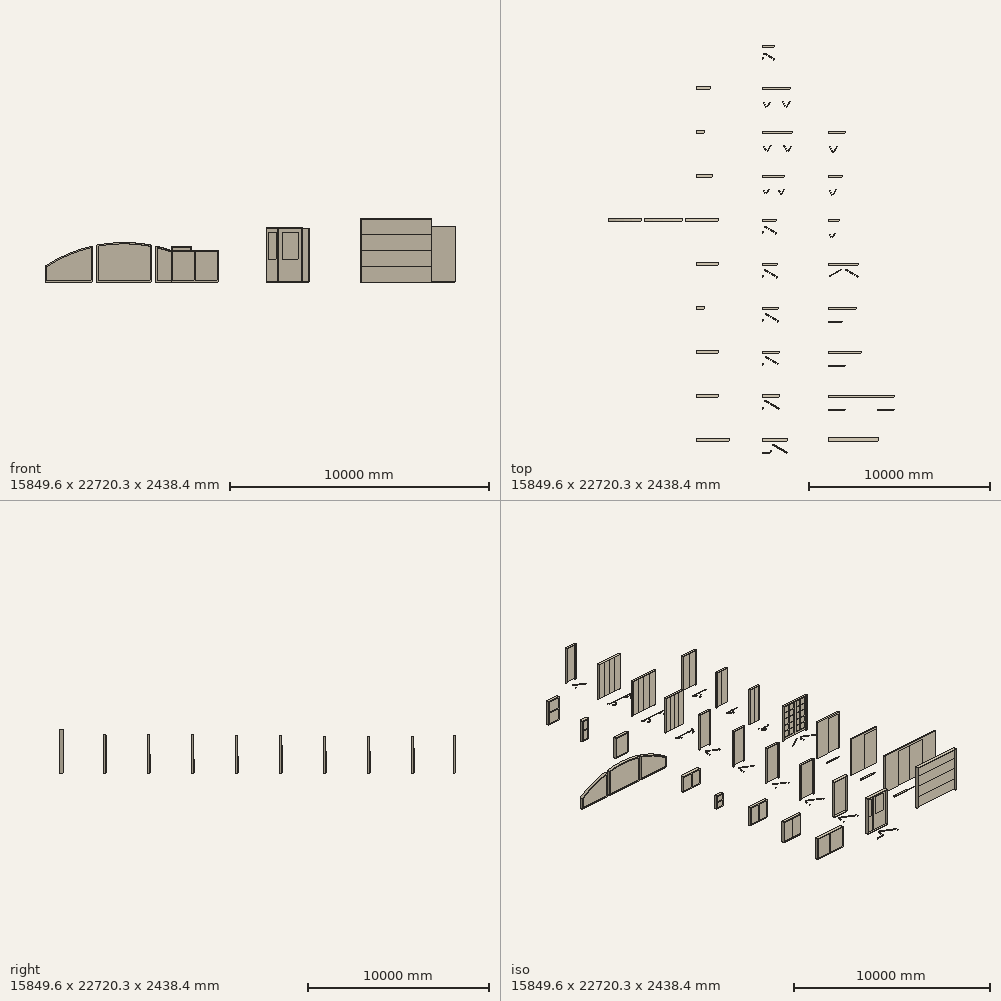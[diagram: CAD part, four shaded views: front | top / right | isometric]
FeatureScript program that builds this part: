
annotation { "Feature Type Name" : "Feature", "Feature Type Description" : "" }
export const myFeature = defineFeature(function(context is Context, id is Id, definition is map)
    precondition{}
    {
        {
            var Q0;
            Q0=qCreatedBy(makeId("Front.planeOp"),FACE);
            var sketch = newSketch(context, id + "F0", { "sketchPlane" : qUnion([Q0])});
            skLineSegment(sketch, "E0.bottom", {"start": v(0, 0) * mm, "end": v(1828.8, 0) * mm});
            skLineSegment(sketch, "E0.top", {"start": v(0, 1219.2) * mm, "end": v(1828.8, 1219.2) * mm});
            skLineSegment(sketch, "E0.left", {"start": v(0, 0) * mm, "end": v(0, 1219.2) * mm});
            skLineSegment(sketch, "E0.right", {"start": v(1828.8, 0) * mm, "end": v(1828.8, 1219.2) * mm});
            skSolve(sketch);
        }
        {
            var Q0;
            Q0=qSketchRegion(id+"F0",true);
            extrude(context, id + "F1", {"entities" : qUnion([Q0]), "oppositeDirection" : true, "depth" : 50.8 * mm});
        }
        {
            var Q0;
            Q0=makeQuery(id+"F1.opExtrude","CAP_FACE",FACE,{"disambiguationData":[OSD([sQuery(id+"F0.wireOp",EDGE,"E0.bottom"),sQuery(id+"F0.wireOp",EDGE,"E0.top"),sQuery(id+"F0.wireOp",EDGE,"E0.left"),sQuery(id+"F0.wireOp",EDGE,"E0.right")])],"isStart":false});
            var sketch = newSketch(context, id + "F2", { "sketchPlane" : qUnion([Q0])});
            skLineSegment(sketch, "E1.bottom", {"start": v(-1778, 1168.4) * mm, "end": v(-939.8, 1168.4) * mm});
            skLineSegment(sketch, "E1.top", {"start": v(-1778, 50.8) * mm, "end": v(-939.8, 50.8) * mm});
            skLineSegment(sketch, "E1.left", {"start": v(-1778, 1168.4) * mm, "end": v(-1778, 50.8) * mm});
            skLineSegment(sketch, "E1.right", {"start": v(-939.8, 1168.4) * mm, "end": v(-939.8, 50.8) * mm});
            skLineSegment(sketch, "E2.bottom", {"start": v(-889, 1168.4) * mm, "end": v(-50.8, 1168.4) * mm});
            skLineSegment(sketch, "E2.top", {"start": v(-889, 50.8) * mm, "end": v(-50.8, 50.8) * mm});
            skLineSegment(sketch, "E2.left", {"start": v(-889, 1168.4) * mm, "end": v(-889, 50.8) * mm});
            skLineSegment(sketch, "E2.right", {"start": v(-50.8, 1168.4) * mm, "end": v(-50.8, 50.8) * mm});
            skSolve(sketch);
        }
        {
            var Q0;
            Q0=qSketchRegion(id+"F2",true);
            extrude(context, id + "F3", {"entities" : qUnion([Q0]), "operationType" : NewBodyOperationType.REMOVE, "oppositeDirection" : true, "depth" : 12.7 * mm});
        }
        {
            var Q0;
            Q0=makeQuery(id+"F1.opExtrude","CAP_FACE",FACE,{"disambiguationData":[OSD([sQuery(id+"F0.wireOp",EDGE,"E0.bottom"),sQuery(id+"F0.wireOp",EDGE,"E0.top"),sQuery(id+"F0.wireOp",EDGE,"E0.left"),sQuery(id+"F0.wireOp",EDGE,"E0.right")])],"isStart":true});
            var sketch = newSketch(context, id + "F4", { "sketchPlane" : qUnion([Q0])});
            skLineSegment(sketch, "E3.0.0", {"start": v(1778, 1168.4) * mm, "end": v(1778, 50.8) * mm});
            skLineSegment(sketch, "E3.0.1", {"start": v(1778, 50.8) * mm, "end": v(939.8, 50.8) * mm});
            skLineSegment(sketch, "E3.0.2", {"start": v(939.8, 50.8) * mm, "end": v(939.8, 1168.4) * mm});
            skLineSegment(sketch, "E3.0.3", {"start": v(939.8, 1168.4) * mm, "end": v(1778, 1168.4) * mm});
            skLineSegment(sketch, "E4.0.0", {"start": v(889, 1168.4) * mm, "end": v(889, 50.8) * mm});
            skLineSegment(sketch, "E4.0.1", {"start": v(889, 50.8) * mm, "end": v(50.8, 50.8) * mm});
            skLineSegment(sketch, "E4.0.2", {"start": v(50.8, 50.8) * mm, "end": v(50.8, 1168.4) * mm});
            skLineSegment(sketch, "E4.0.3", {"start": v(50.8, 1168.4) * mm, "end": v(889, 1168.4) * mm});
            skSolve(sketch);
        }
        {
            var Q0;
            Q0=qSketchRegion(id+"F4",true);
            extrude(context, id + "F5", {"entities" : qUnion([Q0]), "operationType" : NewBodyOperationType.REMOVE, "oppositeDirection" : true, "depth" : 12.7 * mm});
        }
        {
            var Q0;
            Q0=makeQuery(id+"F1.opExtrude","CAP_FACE",FACE,{"disambiguationData":[OSD([sQuery(id+"F0.wireOp",EDGE,"E0.bottom"),sQuery(id+"F0.wireOp",EDGE,"E0.top"),sQuery(id+"F0.wireOp",EDGE,"E0.left"),sQuery(id+"F0.wireOp",EDGE,"E0.right")])],"isStart":false});
            var sketch = newSketch(context, id + "F6", { "sketchPlane" : qUnion([Q0])});
            skLineSegment(sketch, "E5.bottom", {"start": v(-1809.75, 1200.15) * mm, "end": v(-19.05, 1200.15) * mm});
            skLineSegment(sketch, "E5.top", {"start": v(-1809.75, 19.05) * mm, "end": v(-19.05, 19.05) * mm});
            skLineSegment(sketch, "E5.left", {"start": v(-1809.75, 1200.15) * mm, "end": v(-1809.75, 19.05) * mm});
            skLineSegment(sketch, "E5.right", {"start": v(-19.05, 1200.15) * mm, "end": v(-19.05, 19.05) * mm});
            skSolve(sketch);
        }
        {
            var Q0;
            Q0=makeQuery(id+"F6.imprint","IMPRINT",FACE,{"disambiguationData":[TD([[makeQuery(id+"F6.imprint","IMPRINT",EDGE,{"derivedFrom":sQuery(id+"F6.wireOp",EDGE,"E5.bottom")}),1.0]])]});
            extrude(context, id + "F7", {"entities" : qUnion([Q0]), "operationType" : NewBodyOperationType.ADD, "depth" : 114.3 * mm});
        }
        {
            var Q0;
            Q0=qCreatedBy(makeId("Front.planeOp"),FACE);
            cPlane(context, id + "F8", {"entities" : qUnion([Q0]), "cplaneType" : CPlaneType.OFFSET, "offset" : 2438.4 * mm, "oppositeDirection" : true, "width" : 152.4 * mm, "height" : 152.4 * mm});
        }
        {
            var Q0;
            Q0=qCreatedBy(id+"F8.planeOp",FACE);
            var sketch = newSketch(context, id + "F9", { "sketchPlane" : qUnion([Q0])});
            skLineSegment(sketch, "E6.bottom", {"start": v(0, 0) * mm, "end": v(1219.2, 0) * mm});
            skLineSegment(sketch, "E6.top", {"start": v(0, 1219.2) * mm, "end": v(1219.2, 1219.2) * mm});
            skLineSegment(sketch, "E6.left", {"start": v(0, 0) * mm, "end": v(0, 1219.2) * mm});
            skLineSegment(sketch, "E6.right", {"start": v(1219.2, 0) * mm, "end": v(1219.2, 1219.2) * mm});
            skSolve(sketch);
        }
        {
            var Q0;
            Q0=qSketchRegion(id+"F9",true);
            extrude(context, id + "F10", {"entities" : qUnion([Q0]), "oppositeDirection" : true, "depth" : 50.8 * mm});
        }
        {
            var Q0;
            Q0=makeQuery(id+"F10.opExtrude","CAP_FACE",FACE,{"disambiguationData":[OSD([sQuery(id+"F9.wireOp",EDGE,"E6.bottom"),sQuery(id+"F9.wireOp",EDGE,"E6.top"),sQuery(id+"F9.wireOp",EDGE,"E6.left"),sQuery(id+"F9.wireOp",EDGE,"E6.right")])],"isStart":true});
            var sketch = newSketch(context, id + "F11", { "sketchPlane" : qUnion([Q0])});
            skLineSegment(sketch, "E7.bottom", {"start": v(50.8, 1168.4) * mm, "end": v(584.2, 1168.4) * mm});
            skLineSegment(sketch, "E7.top", {"start": v(50.8, 50.8) * mm, "end": v(584.2, 50.8) * mm});
            skLineSegment(sketch, "E7.left", {"start": v(50.8, 1168.4) * mm, "end": v(50.8, 50.8) * mm});
            skLineSegment(sketch, "E7.right", {"start": v(584.2, 1168.4) * mm, "end": v(584.2, 50.8) * mm});
            skLineSegment(sketch, "E8.bottom", {"start": v(635, 1168.4) * mm, "end": v(1168.4, 1168.4) * mm});
            skLineSegment(sketch, "E8.top", {"start": v(635, 50.8) * mm, "end": v(1168.4, 50.8) * mm});
            skLineSegment(sketch, "E8.left", {"start": v(635, 1168.4) * mm, "end": v(635, 50.8) * mm});
            skLineSegment(sketch, "E8.right", {"start": v(1168.4, 1168.4) * mm, "end": v(1168.4, 50.8) * mm});
            skSolve(sketch);
        }
        {
            var Q0;
            Q0=qSketchRegion(id+"F11",true);
            extrude(context, id + "F12", {"entities" : qUnion([Q0]), "operationType" : NewBodyOperationType.REMOVE, "oppositeDirection" : true, "depth" : 12.7 * mm});
        }
        {
            var Q0;
            Q0=makeQuery(id+"F10.opExtrude","CAP_FACE",FACE,{"disambiguationData":[OSD([sQuery(id+"F9.wireOp",EDGE,"E6.bottom"),sQuery(id+"F9.wireOp",EDGE,"E6.top"),sQuery(id+"F9.wireOp",EDGE,"E6.left"),sQuery(id+"F9.wireOp",EDGE,"E6.right")])],"isStart":false});
            var sketch = newSketch(context, id + "F13", { "sketchPlane" : qUnion([Q0])});
            skLineSegment(sketch, "E9.0.0", {"start": v(-50.8, 1168.4) * mm, "end": v(-50.8, 50.8) * mm});
            skLineSegment(sketch, "E9.0.1", {"start": v(-50.8, 50.8) * mm, "end": v(-584.2, 50.8) * mm});
            skLineSegment(sketch, "E9.0.2", {"start": v(-584.2, 50.8) * mm, "end": v(-584.2, 1168.4) * mm});
            skLineSegment(sketch, "E9.0.3", {"start": v(-584.2, 1168.4) * mm, "end": v(-50.8, 1168.4) * mm});
            skLineSegment(sketch, "E10.0.0", {"start": v(-635, 1168.4) * mm, "end": v(-635, 50.8) * mm});
            skLineSegment(sketch, "E10.0.1", {"start": v(-635, 50.8) * mm, "end": v(-1168.4, 50.8) * mm});
            skLineSegment(sketch, "E10.0.2", {"start": v(-1168.4, 50.8) * mm, "end": v(-1168.4, 1168.4) * mm});
            skLineSegment(sketch, "E10.0.3", {"start": v(-1168.4, 1168.4) * mm, "end": v(-635, 1168.4) * mm});
            skSolve(sketch);
        }
        {
            var Q0;
            Q0=qSketchRegion(id+"F13",true);
            extrude(context, id + "F14", {"entities" : qUnion([Q0]), "operationType" : NewBodyOperationType.REMOVE, "oppositeDirection" : true, "depth" : 12.7 * mm});
        }
        {
            var Q0;
            Q0=makeQuery(id+"F10.opExtrude","CAP_FACE",FACE,{"disambiguationData":[OSD([sQuery(id+"F9.wireOp",EDGE,"E6.bottom"),sQuery(id+"F9.wireOp",EDGE,"E6.top"),sQuery(id+"F9.wireOp",EDGE,"E6.left"),sQuery(id+"F9.wireOp",EDGE,"E6.right")])],"isStart":false});
            var sketch = newSketch(context, id + "F15", { "sketchPlane" : qUnion([Q0])});
            skLineSegment(sketch, "E11.bottom", {"start": v(-1200.15, 1200.15) * mm, "end": v(-19.05, 1200.15) * mm});
            skLineSegment(sketch, "E11.top", {"start": v(-1200.15, 19.05) * mm, "end": v(-19.05, 19.05) * mm});
            skLineSegment(sketch, "E11.left", {"start": v(-1200.15, 1200.15) * mm, "end": v(-1200.15, 19.05) * mm});
            skLineSegment(sketch, "E11.right", {"start": v(-19.05, 1200.15) * mm, "end": v(-19.05, 19.05) * mm});
            skSolve(sketch);
        }
        {
            var Q0;
            Q0=makeQuery(id+"F15.imprint","IMPRINT",FACE,{"disambiguationData":[TD([[makeQuery(id+"F15.imprint","IMPRINT",EDGE,{"derivedFrom":sQuery(id+"F15.wireOp",EDGE,"E11.bottom")}),1.0]])]});
            extrude(context, id + "F16", {"entities" : qUnion([Q0]), "operationType" : NewBodyOperationType.ADD, "depth" : 114.3 * mm});
        }
        {
            var Q0;
            Q0=qCreatedBy(id+"F8.planeOp",FACE);
            cPlane(context, id + "F17", {"entities" : qUnion([Q0]), "cplaneType" : CPlaneType.OFFSET, "offset" : 2438.4 * mm, "oppositeDirection" : true, "width" : 152.4 * mm, "height" : 152.4 * mm});
        }
        {
            var Q0;
            Q0=qCreatedBy(id+"F17.planeOp",FACE);
            var sketch = newSketch(context, id + "F18", { "sketchPlane" : qUnion([Q0])});
            skLineSegment(sketch, "E12.bottom", {"start": v(0, 0) * mm, "end": v(1219.2, 0) * mm});
            skLineSegment(sketch, "E12.top", {"start": v(0, 1066.8) * mm, "end": v(1219.2, 1066.8) * mm});
            skLineSegment(sketch, "E12.left", {"start": v(0, 0) * mm, "end": v(0, 1066.8) * mm});
            skLineSegment(sketch, "E12.right", {"start": v(1219.2, 0) * mm, "end": v(1219.2, 1066.8) * mm});
            skSolve(sketch);
        }
        {
            var Q0;
            Q0=qSketchRegion(id+"F18",true);
            extrude(context, id + "F19", {"entities" : qUnion([Q0]), "oppositeDirection" : true, "depth" : 50.8 * mm});
        }
        {
            var Q0;
            Q0=makeQuery(id+"F19.opExtrude","CAP_FACE",FACE,{"disambiguationData":[OSD([sQuery(id+"F18.wireOp",EDGE,"E12.bottom"),sQuery(id+"F18.wireOp",EDGE,"E12.top"),sQuery(id+"F18.wireOp",EDGE,"E12.left"),sQuery(id+"F18.wireOp",EDGE,"E12.right")])],"isStart":true});
            var sketch = newSketch(context, id + "F20", { "sketchPlane" : qUnion([Q0])});
            skLineSegment(sketch, "E13.bottom", {"start": v(50.8, 1016) * mm, "end": v(584.2, 1016) * mm});
            skLineSegment(sketch, "E13.top", {"start": v(50.8, 50.8) * mm, "end": v(584.2, 50.8) * mm});
            skLineSegment(sketch, "E13.left", {"start": v(50.8, 1016) * mm, "end": v(50.8, 50.8) * mm});
            skLineSegment(sketch, "E13.right", {"start": v(584.2, 1016) * mm, "end": v(584.2, 50.8) * mm});
            skLineSegment(sketch, "E14.bottom", {"start": v(635, 1016) * mm, "end": v(1168.4, 1016) * mm});
            skLineSegment(sketch, "E14.top", {"start": v(635, 50.8) * mm, "end": v(1168.4, 50.8) * mm});
            skLineSegment(sketch, "E14.left", {"start": v(635, 1016) * mm, "end": v(635, 50.8) * mm});
            skLineSegment(sketch, "E14.right", {"start": v(1168.4, 1016) * mm, "end": v(1168.4, 50.8) * mm});
            skSolve(sketch);
        }
        {
            var Q0;
            Q0=qSketchRegion(id+"F20",true);
            extrude(context, id + "F21", {"entities" : qUnion([Q0]), "operationType" : NewBodyOperationType.REMOVE, "oppositeDirection" : true, "depth" : 12.7 * mm});
        }
        {
            var Q0;
            Q0=makeQuery(id+"F19.opExtrude","CAP_FACE",FACE,{"disambiguationData":[OSD([sQuery(id+"F18.wireOp",EDGE,"E12.bottom"),sQuery(id+"F18.wireOp",EDGE,"E12.top"),sQuery(id+"F18.wireOp",EDGE,"E12.left"),sQuery(id+"F18.wireOp",EDGE,"E12.right")])],"isStart":false});
            var sketch = newSketch(context, id + "F22", { "sketchPlane" : qUnion([Q0])});
            skLineSegment(sketch, "E15.0.0", {"start": v(-50.8, 1016) * mm, "end": v(-50.8, 50.8) * mm});
            skLineSegment(sketch, "E15.0.1", {"start": v(-50.8, 50.8) * mm, "end": v(-584.2, 50.8) * mm});
            skLineSegment(sketch, "E15.0.2", {"start": v(-584.2, 50.8) * mm, "end": v(-584.2, 1016) * mm});
            skLineSegment(sketch, "E15.0.3", {"start": v(-584.2, 1016) * mm, "end": v(-50.8, 1016) * mm});
            skLineSegment(sketch, "E16.0.0", {"start": v(-635, 1016) * mm, "end": v(-635, 50.8) * mm});
            skLineSegment(sketch, "E16.0.1", {"start": v(-635, 50.8) * mm, "end": v(-1168.4, 50.8) * mm});
            skLineSegment(sketch, "E16.0.2", {"start": v(-1168.4, 50.8) * mm, "end": v(-1168.4, 1016) * mm});
            skLineSegment(sketch, "E16.0.3", {"start": v(-1168.4, 1016) * mm, "end": v(-635, 1016) * mm});
            skSolve(sketch);
        }
        {
            var Q0;
            Q0=qSketchRegion(id+"F22",true);
            extrude(context, id + "F23", {"entities" : qUnion([Q0]), "operationType" : NewBodyOperationType.REMOVE, "oppositeDirection" : true, "depth" : 12.7 * mm});
        }
        {
            var Q0;
            Q0=makeQuery(id+"F19.opExtrude","CAP_FACE",FACE,{"disambiguationData":[OSD([sQuery(id+"F18.wireOp",EDGE,"E12.bottom"),sQuery(id+"F18.wireOp",EDGE,"E12.top"),sQuery(id+"F18.wireOp",EDGE,"E12.left"),sQuery(id+"F18.wireOp",EDGE,"E12.right")])],"isStart":false});
            var sketch = newSketch(context, id + "F24", { "sketchPlane" : qUnion([Q0])});
            skLineSegment(sketch, "E17.bottom", {"start": v(-1200.15, 1047.75) * mm, "end": v(-19.05, 1047.75) * mm});
            skLineSegment(sketch, "E17.top", {"start": v(-1200.15, 19.05) * mm, "end": v(-19.05, 19.05) * mm});
            skLineSegment(sketch, "E17.left", {"start": v(-1200.15, 1047.75) * mm, "end": v(-1200.15, 19.05) * mm});
            skLineSegment(sketch, "E17.right", {"start": v(-19.05, 1047.75) * mm, "end": v(-19.05, 19.05) * mm});
            skSolve(sketch);
        }
        {
            var Q0;
            Q0=makeQuery(id+"F24.imprint","IMPRINT",FACE,{"disambiguationData":[TD([[makeQuery(id+"F24.imprint","IMPRINT",EDGE,{"derivedFrom":sQuery(id+"F24.wireOp",EDGE,"E17.bottom")}),1.0]])]});
            extrude(context, id + "F25", {"entities" : qUnion([Q0]), "operationType" : NewBodyOperationType.ADD, "depth" : 114.3 * mm});
        }
        {
            var Q0;
            Q0=qCreatedBy(id+"F17.planeOp",FACE);
            cPlane(context, id + "F26", {"entities" : qUnion([Q0]), "cplaneType" : CPlaneType.OFFSET, "offset" : 2438.4 * mm, "oppositeDirection" : true, "width" : 152.4 * mm, "height" : 152.4 * mm});
        }
        {
            var Q0;
            Q0=qCreatedBy(id+"F26.planeOp",FACE);
            var sketch = newSketch(context, id + "F27", { "sketchPlane" : qUnion([Q0])});
            skLineSegment(sketch, "E18.bottom", {"start": v(0, 0) * mm, "end": v(457.2, 0) * mm});
            skLineSegment(sketch, "E18.top", {"start": v(0, 762) * mm, "end": v(457.2, 762) * mm});
            skLineSegment(sketch, "E18.left", {"start": v(0, 0) * mm, "end": v(0, 762) * mm});
            skLineSegment(sketch, "E18.right", {"start": v(457.2, 0) * mm, "end": v(457.2, 762) * mm});
            skSolve(sketch);
        }
        {
            var Q0;
            Q0=qSketchRegion(id+"F27",true);
            extrude(context, id + "F28", {"entities" : qUnion([Q0]), "oppositeDirection" : true, "depth" : 50.8 * mm});
        }
        {
            var Q0;
            Q0=makeQuery(id+"F28.opExtrude","CAP_FACE",FACE,{"disambiguationData":[OSD([sQuery(id+"F27.wireOp",EDGE,"E18.bottom"),sQuery(id+"F27.wireOp",EDGE,"E18.top"),sQuery(id+"F27.wireOp",EDGE,"E18.left"),sQuery(id+"F27.wireOp",EDGE,"E18.right")])],"isStart":true});
            var sketch = newSketch(context, id + "F29", { "sketchPlane" : qUnion([Q0])});
            skLineSegment(sketch, "E19.bottom", {"start": v(50.8, 711.2) * mm, "end": v(406.4, 711.2) * mm});
            skLineSegment(sketch, "E19.top", {"start": v(50.8, 406.4) * mm, "end": v(406.4, 406.4) * mm});
            skLineSegment(sketch, "E19.left", {"start": v(50.8, 711.2) * mm, "end": v(50.8, 406.4) * mm});
            skLineSegment(sketch, "E19.right", {"start": v(406.4, 711.2) * mm, "end": v(406.4, 406.4) * mm});
            skLineSegment(sketch, "E20.bottom", {"start": v(50.8, 355.6) * mm, "end": v(406.4, 355.6) * mm});
            skLineSegment(sketch, "E20.top", {"start": v(50.8, 50.8) * mm, "end": v(406.4, 50.8) * mm});
            skLineSegment(sketch, "E20.left", {"start": v(50.8, 355.6) * mm, "end": v(50.8, 50.8) * mm});
            skLineSegment(sketch, "E20.right", {"start": v(406.4, 355.6) * mm, "end": v(406.4, 50.8) * mm});
            skSolve(sketch);
        }
        {
            var Q0;
            Q0=qSketchRegion(id+"F29",true);
            extrude(context, id + "F30", {"entities" : qUnion([Q0]), "operationType" : NewBodyOperationType.REMOVE, "oppositeDirection" : true, "depth" : 12.7 * mm});
        }
        {
            var Q0;
            Q0=makeQuery(id+"F28.opExtrude","CAP_FACE",FACE,{"disambiguationData":[OSD([sQuery(id+"F27.wireOp",EDGE,"E18.bottom"),sQuery(id+"F27.wireOp",EDGE,"E18.top"),sQuery(id+"F27.wireOp",EDGE,"E18.left"),sQuery(id+"F27.wireOp",EDGE,"E18.right")])],"isStart":false});
            var sketch = newSketch(context, id + "F31", { "sketchPlane" : qUnion([Q0])});
            skLineSegment(sketch, "E21.0.0", {"start": v(-50.8, 711.2) * mm, "end": v(-50.8, 406.4) * mm});
            skLineSegment(sketch, "E21.0.1", {"start": v(-50.8, 406.4) * mm, "end": v(-406.4, 406.4) * mm});
            skLineSegment(sketch, "E21.0.2", {"start": v(-406.4, 406.4) * mm, "end": v(-406.4, 711.2) * mm});
            skLineSegment(sketch, "E21.0.3", {"start": v(-406.4, 711.2) * mm, "end": v(-50.8, 711.2) * mm});
            skLineSegment(sketch, "E22.0.0", {"start": v(-50.8, 355.6) * mm, "end": v(-50.8, 50.8) * mm});
            skLineSegment(sketch, "E22.0.1", {"start": v(-50.8, 50.8) * mm, "end": v(-406.4, 50.8) * mm});
            skLineSegment(sketch, "E22.0.2", {"start": v(-406.4, 50.8) * mm, "end": v(-406.4, 355.6) * mm});
            skLineSegment(sketch, "E22.0.3", {"start": v(-406.4, 355.6) * mm, "end": v(-50.8, 355.6) * mm});
            skSolve(sketch);
        }
        {
            var Q0;
            Q0=qSketchRegion(id+"F31",true);
            extrude(context, id + "F32", {"entities" : qUnion([Q0]), "operationType" : NewBodyOperationType.REMOVE, "oppositeDirection" : true, "depth" : 12.7 * mm});
        }
        {
            var Q0;
            Q0=makeQuery(id+"F28.opExtrude","CAP_FACE",FACE,{"disambiguationData":[OSD([sQuery(id+"F27.wireOp",EDGE,"E18.bottom"),sQuery(id+"F27.wireOp",EDGE,"E18.top"),sQuery(id+"F27.wireOp",EDGE,"E18.left"),sQuery(id+"F27.wireOp",EDGE,"E18.right")])],"isStart":false});
            var sketch = newSketch(context, id + "F33", { "sketchPlane" : qUnion([Q0])});
            skLineSegment(sketch, "E23.bottom", {"start": v(-438.15, 742.95) * mm, "end": v(-19.05, 742.95) * mm});
            skLineSegment(sketch, "E23.top", {"start": v(-438.15, 19.05) * mm, "end": v(-19.05, 19.05) * mm});
            skLineSegment(sketch, "E23.left", {"start": v(-438.15, 742.95) * mm, "end": v(-438.15, 19.05) * mm});
            skLineSegment(sketch, "E23.right", {"start": v(-19.05, 742.95) * mm, "end": v(-19.05, 19.05) * mm});
            skSolve(sketch);
        }
        {
            var Q0;
            Q0=makeQuery(id+"F33.imprint","IMPRINT",FACE,{"disambiguationData":[TD([[makeQuery(id+"F33.imprint","IMPRINT",EDGE,{"derivedFrom":sQuery(id+"F33.wireOp",EDGE,"E23.bottom")}),1.0]])]});
            extrude(context, id + "F34", {"entities" : qUnion([Q0]), "operationType" : NewBodyOperationType.ADD, "depth" : 114.3 * mm});
        }
        {
            var Q0;
            Q0=qCreatedBy(makeId("Front.planeOp"),FACE);
            var sketch = newSketch(context, id + "F35", { "sketchPlane" : qUnion([Q0])});
            skLineSegment(sketch, "E24.bottom", {"start": v(3657.6, 0) * mm, "end": v(5064.13, 0) * mm});
            skLineSegment(sketch, "E24.top", {"start": v(3657.6, 2095.5) * mm, "end": v(5064.13, 2095.5) * mm});
            skLineSegment(sketch, "E24.left", {"start": v(3657.6, 0) * mm, "end": v(3657.6, 2095.5) * mm});
            skLineSegment(sketch, "E24.right", {"start": v(5064.13, 0) * mm, "end": v(5064.13, 2095.5) * mm});
            skSolve(sketch);
        }
        {
            var Q0;
            Q0=qSketchRegion(id+"F35",true);
            extrude(context, id + "F36", {"entities" : qUnion([Q0]), "oppositeDirection" : true, "depth" : 165.1 * mm});
        }
        {
            var Q0;
            Q0=makeQuery(id+"F36.opExtrude","CAP_FACE",FACE,{"disambiguationData":[OSD([sQuery(id+"F35.wireOp",EDGE,"E24.bottom"),sQuery(id+"F35.wireOp",EDGE,"E24.top"),sQuery(id+"F35.wireOp",EDGE,"E24.left"),sQuery(id+"F35.wireOp",EDGE,"E24.right")])],"isStart":true});
            var sketch = newSketch(context, id + "F37", { "sketchPlane" : qUnion([Q0])});
            skLineSegment(sketch, "E25.bottom", {"start": v(3683, 2057.4) * mm, "end": v(5038.73, 2057.4) * mm});
            skLineSegment(sketch, "E25.top", {"start": v(3683, 25.4) * mm, "end": v(5038.73, 25.4) * mm});
            skLineSegment(sketch, "E25.left", {"start": v(3683, 2057.4) * mm, "end": v(3683, 25.4) * mm});
            skLineSegment(sketch, "E25.right", {"start": v(5038.73, 2057.4) * mm, "end": v(5038.73, 25.4) * mm});
            skSolve(sketch);
        }
        {
            var Q0;
            Q0=qSketchRegion(id+"F37",true);
            extrude(context, id + "F38", {"entities" : qUnion([Q0]), "operationType" : NewBodyOperationType.REMOVE, "oppositeDirection" : true, "depth" : 120.65 * mm});
        }
        {
            var Q0;
            Q0=makeQuery(id+"F38.boolean.opBoolean","COPY",FACE,{"derivedFrom":makeQuery(id+"F38.opExtrude","CAP_FACE",FACE,{"disambiguationData":[OSD([sQuery(id+"F37.wireOp",EDGE,"E25.bottom"),sQuery(id+"F37.wireOp",EDGE,"E25.top"),sQuery(id+"F37.wireOp",EDGE,"E25.left"),sQuery(id+"F37.wireOp",EDGE,"E25.right")])],"isStart":false})});
            var sketch = newSketch(context, id + "F39", { "sketchPlane" : qUnion([Q0])});
            skLineSegment(sketch, "E26.bottom", {"start": v(4086.23, 2057.4) * mm, "end": v(4124.33, 2057.4) * mm});
            skLineSegment(sketch, "E26.top", {"start": v(4086.23, 25.4) * mm, "end": v(4124.33, 25.4) * mm});
            skLineSegment(sketch, "E26.left", {"start": v(4086.23, 2057.4) * mm, "end": v(4086.23, 25.4) * mm});
            skLineSegment(sketch, "E26.right", {"start": v(4124.33, 2057.4) * mm, "end": v(4124.33, 25.4) * mm});
            skSolve(sketch);
        }
        {
            var Q0;
            Q0=qSketchRegion(id+"F39",true);
            extrude(context, id + "F40", {"entities" : qUnion([Q0]), "operationType" : NewBodyOperationType.ADD, "depth" : 19.05 * mm});
        }
        {
            var Q0;
            Q0=makeQuery(id+"F36.opExtrude","CAP_FACE",FACE,{"disambiguationData":[OSD([sQuery(id+"F35.wireOp",EDGE,"E24.bottom"),sQuery(id+"F35.wireOp",EDGE,"E24.top"),sQuery(id+"F35.wireOp",EDGE,"E24.left"),sQuery(id+"F35.wireOp",EDGE,"E24.right")])],"isStart":false});
            var sketch = newSketch(context, id + "F41", { "sketchPlane" : qUnion([Q0])});
            skLineSegment(sketch, "E27.0.0", {"start": v(-4086.23, 25.4) * mm, "end": v(-4086.23, 2057.4) * mm});
            skLineSegment(sketch, "E27.0.1", {"start": v(-4086.23, 2057.4) * mm, "end": v(-3683, 2057.4) * mm});
            skLineSegment(sketch, "E27.0.2", {"start": v(-3683, 2057.4) * mm, "end": v(-3683, 25.4) * mm});
            skLineSegment(sketch, "E27.0.3", {"start": v(-3683, 25.4) * mm, "end": v(-4086.23, 25.4) * mm});
            skLineSegment(sketch, "E28.0.0", {"start": v(-5038.73, 2057.4) * mm, "end": v(-4124.33, 2057.4) * mm});
            skLineSegment(sketch, "E28.0.1", {"start": v(-4124.33, 2057.4) * mm, "end": v(-4124.33, 25.4) * mm});
            skLineSegment(sketch, "E28.0.2", {"start": v(-4124.33, 25.4) * mm, "end": v(-5038.73, 25.4) * mm});
            skLineSegment(sketch, "E28.0.3", {"start": v(-5038.73, 25.4) * mm, "end": v(-5038.73, 2057.4) * mm});
            skSolve(sketch);
        }
        {
            var Q0;
            Q0=qSketchRegion(id+"F41",true);
            extrude(context, id + "F42", {"entities" : qUnion([Q0]), "operationType" : NewBodyOperationType.REMOVE, "oppositeDirection" : true, "depth" : 1.59 * mm});
        }
        {
            var Q0;
            {var subQ0=sQuery(id+"F37.wireOp",EDGE,"E25.bottom");var subQ1=sQuery(id+"F37.wireOp",EDGE,"E25.top");var subQ2=sQuery(id+"F37.wireOp",EDGE,"E25.right");Q0=makeQuery(id+"F40.boolean.opBoolean","SPLIT",FACE,{"disambiguationData":[TD([makeQuery(id+"F38.boolean.opBoolean","COPY",FACE,{"derivedFrom":makeQuery(id+"F38.opExtrude","SWEPT_FACE",FACE,{"disambiguationData":[OSD([subQ2])]})})])],"derivedFrom":makeQuery(id+"F38.boolean.opBoolean","COPY",FACE,{"derivedFrom":makeQuery(id+"F38.opExtrude","CAP_FACE",FACE,{"disambiguationData":[OSD([subQ0,subQ1,sQuery(id+"F37.wireOp",EDGE,"E25.left"),subQ2])],"isStart":false})})});}
            var sketch = newSketch(context, id + "F43", { "sketchPlane" : qUnion([Q0])});
            skLineSegment(sketch, "E29.bottom", {"start": v(4276.73, 1905) * mm, "end": v(4886.32, 1905) * mm});
            skLineSegment(sketch, "E29.top", {"start": v(4276.73, 889) * mm, "end": v(4886.32, 889) * mm});
            skLineSegment(sketch, "E29.left", {"start": v(4276.73, 1905) * mm, "end": v(4276.73, 889) * mm});
            skLineSegment(sketch, "E29.right", {"start": v(4886.32, 1905) * mm, "end": v(4886.32, 889) * mm});
            skLineSegment(sketch, "E30.bottom", {"start": v(3733.8, 1905) * mm, "end": v(4035.43, 1905) * mm});
            skLineSegment(sketch, "E30.top", {"start": v(3733.8, 889) * mm, "end": v(4035.43, 889) * mm});
            skLineSegment(sketch, "E30.left", {"start": v(3733.8, 1905) * mm, "end": v(3733.8, 889) * mm});
            skLineSegment(sketch, "E30.right", {"start": v(4035.43, 1905) * mm, "end": v(4035.43, 889) * mm});
            skSolve(sketch);
        }
        {
            var Q0;
            Q0=qSketchRegion(id+"F43",true);
            extrude(context, id + "F44", {"entities" : qUnion([Q0]), "operationType" : NewBodyOperationType.REMOVE, "oppositeDirection" : true, "depth" : 12.7 * mm});
        }
        {
            var Q0;
            Q0=makeQuery(id+"F42.boolean.opBoolean","COPY",FACE,{"derivedFrom":makeQuery(id+"F42.opExtrude","CAP_FACE",FACE,{"disambiguationData":[OSD([sQuery(id+"F41.wireOp",EDGE,"E28.0.0"),sQuery(id+"F41.wireOp",EDGE,"E28.0.1"),sQuery(id+"F41.wireOp",EDGE,"E28.0.2"),sQuery(id+"F41.wireOp",EDGE,"E28.0.3")])],"isStart":false})});
            var sketch = newSketch(context, id + "F45", { "sketchPlane" : qUnion([Q0])});
            skLineSegment(sketch, "E31.0.0", {"start": v(-3733.8, 1905) * mm, "end": v(-3733.8, 889) * mm});
            skLineSegment(sketch, "E31.0.1", {"start": v(-3733.8, 889) * mm, "end": v(-4035.43, 889) * mm});
            skLineSegment(sketch, "E31.0.2", {"start": v(-4035.43, 889) * mm, "end": v(-4035.43, 1905) * mm});
            skLineSegment(sketch, "E31.0.3", {"start": v(-4035.43, 1905) * mm, "end": v(-3733.8, 1905) * mm});
            skLineSegment(sketch, "E32.0.0", {"start": v(-4276.73, 1905) * mm, "end": v(-4276.73, 889) * mm});
            skLineSegment(sketch, "E32.0.1", {"start": v(-4276.73, 889) * mm, "end": v(-4886.32, 889) * mm});
            skLineSegment(sketch, "E32.0.2", {"start": v(-4886.32, 889) * mm, "end": v(-4886.32, 1905) * mm});
            skLineSegment(sketch, "E32.0.3", {"start": v(-4886.32, 1905) * mm, "end": v(-4276.73, 1905) * mm});
            skSolve(sketch);
        }
        {
            var Q0;
            Q0=qSketchRegion(id+"F45",true);
            extrude(context, id + "F46", {"entities" : qUnion([Q0]), "operationType" : NewBodyOperationType.REMOVE, "oppositeDirection" : true, "depth" : 12.7 * mm});
        }
        {
            var Q0;
            Q0=qCreatedBy(makeId("Top.planeOp"),FACE);
            var sketch = newSketch(context, id + "F47", { "sketchPlane" : qUnion([Q0])});
            skLineSegment(sketch, "E33", {"start": v(3657.6, -609.6) * mm, "end": v(3657.6, -774.7) * mm});
            skLineSegment(sketch, "E34", {"start": v(3657.6, -774.7) * mm, "end": v(3683, -774.7) * mm});
            skLineSegment(sketch, "E35", {"start": v(3683, -774.7) * mm, "end": v(3683, -654.05) * mm});
            skLineSegment(sketch, "E36", {"start": v(3683, -654.05) * mm, "end": v(4086.23, -654.05) * mm});
            skLineSegment(sketch, "E37", {"start": v(4086.23, -654.05) * mm, "end": v(4086.23, -673.1) * mm});
            skLineSegment(sketch, "E38", {"start": v(4086.23, -673.1) * mm, "end": v(4124.33, -673.1) * mm});
            skLineSegment(sketch, "E39", {"start": v(4124.33, -673.1) * mm, "end": v(4124.33, -654.05) * mm});
            skLineSegment(sketch, "E40", {"start": v(4124.33, -654.05) * mm, "end": v(4127.5, -654.05) * mm});
            skLineSegment(sketch, "E41", {"start": v(5038.73, -654.05) * mm, "end": v(5038.73, -774.7) * mm});
            skLineSegment(sketch, "E42", {"start": v(5038.73, -774.7) * mm, "end": v(5064.13, -774.7) * mm});
            skLineSegment(sketch, "E43", {"start": v(5064.13, -774.7) * mm, "end": v(5064.13, -609.6) * mm});
            skLineSegment(sketch, "E44", {"start": v(5064.13, -609.6) * mm, "end": v(5038.73, -609.6) * mm});
            skLineSegment(sketch, "E45", {"start": v(5038.73, -609.6) * mm, "end": v(4246.83, -152.4) * mm});
            skLineSegment(sketch, "E46", {"start": v(4246.83, -152.4) * mm, "end": v(4224.6, -190.9) * mm});
            skLineSegment(sketch, "E47", {"start": v(4224.6, -190.9) * mm, "end": v(4225.54, -191.44) * mm});
            skLineSegment(sketch, "E48", {"start": v(5016.5, -648.1) * mm, "end": v(5038.7, -609.64) * mm});
            skArc(sketch, "E49", {"start": v(4225.54, -191.44) * mm, "mid": v(4149.99, -394.48) * mm, "end": v(4124.33, -609.6) * mm});
            skArc(sketch, "E50.0", {"start": v(4228.3, -193.02) * mm, "mid": v(4153.06, -395.3) * mm, "end": v(4127.5, -609.6) * mm});
            skLineSegment(sketch, "E51.trimOffspring", {"start": v(4124.33, -609.6) * mm, "end": v(3657.6, -609.6) * mm});
            skLineSegment(sketch, "E52.trimOffspring", {"start": v(4228.3, -193.02) * mm, "end": v(5016.5, -648.1) * mm});
            skLineSegment(sketch, "E53", {"start": v(4127.5, -609.6) * mm, "end": v(4127.5, -654.05) * mm});
            skLineSegment(sketch, "E54", {"start": v(5038.7, -654.05) * mm, "end": v(5038.7, -609.64) * mm});
            skLineSegment(sketch, "E55.trimOffspring", {"start": v(5038.7, -654.05) * mm, "end": v(5038.73, -654.05) * mm});
            skSolve(sketch);
        }
        {
            var Q0;
            Q0=qSketchRegion(id+"F47",true);
            extrude(context, id + "F48", {"entities" : qUnion([Q0]), "depth" : 25.4 * mm});
        }
        {
            var Q0;
            Q0=qCreatedBy(id+"F8.planeOp",FACE);
            var sketch = newSketch(context, id + "F49", { "sketchPlane" : qUnion([Q0])});
            skLineSegment(sketch, "E56.bottom", {"start": v(3657.6, 0) * mm, "end": v(4622.8, 0) * mm});
            skLineSegment(sketch, "E56.top", {"start": v(3657.6, 2095.5) * mm, "end": v(4622.8, 2095.5) * mm});
            skLineSegment(sketch, "E56.left", {"start": v(3657.6, 0) * mm, "end": v(3657.6, 2095.5) * mm});
            skLineSegment(sketch, "E56.right", {"start": v(4622.8, 0) * mm, "end": v(4622.8, 2095.5) * mm});
            skSolve(sketch);
        }
        {
            var Q0;
            Q0=qSketchRegion(id+"F49",true);
            extrude(context, id + "F50", {"entities" : qUnion([Q0]), "oppositeDirection" : true, "depth" : 165.1 * mm});
        }
        {
            var Q0;
            Q0=makeQuery(id+"F50.opExtrude","CAP_FACE",FACE,{"disambiguationData":[OSD([sQuery(id+"F49.wireOp",EDGE,"E56.bottom"),sQuery(id+"F49.wireOp",EDGE,"E56.top"),sQuery(id+"F49.wireOp",EDGE,"E56.left"),sQuery(id+"F49.wireOp",EDGE,"E56.right")])],"isStart":true});
            var sketch = newSketch(context, id + "F51", { "sketchPlane" : qUnion([Q0])});
            skLineSegment(sketch, "E57.bottom", {"start": v(3683, 2057.4) * mm, "end": v(4597.4, 2057.4) * mm});
            skLineSegment(sketch, "E57.top", {"start": v(3683, 25.4) * mm, "end": v(4597.4, 25.4) * mm});
            skLineSegment(sketch, "E57.left", {"start": v(3683, 2057.4) * mm, "end": v(3683, 25.4) * mm});
            skLineSegment(sketch, "E57.right", {"start": v(4597.4, 2057.4) * mm, "end": v(4597.4, 25.4) * mm});
            skSolve(sketch);
        }
        {
            var Q0;
            Q0=qSketchRegion(id+"F51",true);
            extrude(context, id + "F52", {"entities" : qUnion([Q0]), "operationType" : NewBodyOperationType.REMOVE, "oppositeDirection" : true, "depth" : 120.65 * mm});
        }
        {
            var Q0;
            Q0=makeQuery(id+"F50.opExtrude","CAP_FACE",FACE,{"disambiguationData":[OSD([sQuery(id+"F49.wireOp",EDGE,"E56.bottom"),sQuery(id+"F49.wireOp",EDGE,"E56.top"),sQuery(id+"F49.wireOp",EDGE,"E56.left"),sQuery(id+"F49.wireOp",EDGE,"E56.right")])],"isStart":false});
            var sketch = newSketch(context, id + "F53", { "sketchPlane" : qUnion([Q0])});
            skLineSegment(sketch, "E58.0.0", {"start": v(-3683, 2057.4) * mm, "end": v(-3683, 25.4) * mm});
            skLineSegment(sketch, "E58.0.1", {"start": v(-3683, 25.4) * mm, "end": v(-4597.4, 25.4) * mm});
            skLineSegment(sketch, "E58.0.2", {"start": v(-4597.4, 25.4) * mm, "end": v(-4597.4, 2057.4) * mm});
            skLineSegment(sketch, "E58.0.3", {"start": v(-4597.4, 2057.4) * mm, "end": v(-3683, 2057.4) * mm});
            skSolve(sketch);
        }
        {
            var Q0;
            Q0=qSketchRegion(id+"F53",true);
            extrude(context, id + "F54", {"entities" : qUnion([Q0]), "operationType" : NewBodyOperationType.REMOVE, "oppositeDirection" : true, "depth" : 1.59 * mm});
        }
        {
            var Q0;
            Q0=makeQuery(id+"F50.opExtrude","SWEPT_FACE",FACE,{"disambiguationData":[OSD([sQuery(id+"F49.wireOp",EDGE,"E56.bottom")])]});
            var sketch = newSketch(context, id + "F55", { "sketchPlane" : qUnion([Q0])});
            skLineSegment(sketch, "E59", {"start": v(3657.6, -1828.8) * mm, "end": v(3657.6, -1663.7) * mm});
            skLineSegment(sketch, "E60", {"start": v(3657.6, -1663.7) * mm, "end": v(3683, -1663.7) * mm});
            skLineSegment(sketch, "E61", {"start": v(3683, -1663.7) * mm, "end": v(3683, -1784.35) * mm});
            skLineSegment(sketch, "E62", {"start": v(3683, -1784.35) * mm, "end": v(3686.18, -1784.35) * mm});
            skLineSegment(sketch, "E63", {"start": v(4597.4, -1784.35) * mm, "end": v(4597.4, -1663.7) * mm});
            skLineSegment(sketch, "E64", {"start": v(4597.4, -1663.7) * mm, "end": v(4622.8, -1663.7) * mm});
            skLineSegment(sketch, "E65", {"start": v(4622.8, -1663.7) * mm, "end": v(4622.8, -1828.8) * mm});
            skLineSegment(sketch, "E66", {"start": v(4622.8, -1828.8) * mm, "end": v(4597.4, -1828.8) * mm});
            skLineSegment(sketch, "E67", {"start": v(4597.4, -1828.8) * mm, "end": v(3805.5, -2286) * mm});
            skLineSegment(sketch, "E68", {"start": v(3805.5, -2286) * mm, "end": v(3783.28, -2247.5) * mm});
            skLineSegment(sketch, "E69", {"start": v(3783.28, -2247.5) * mm, "end": v(3784.22, -2246.96) * mm});
            skLineSegment(sketch, "E70", {"start": v(4575.18, -1790.3) * mm, "end": v(4597.37, -1828.76) * mm});
            skArc(sketch, "E71", {"start": v(3784.22, -2246.96) * mm, "mid": v(3708.66, -2043.92) * mm, "end": v(3683, -1828.8) * mm});
            skArc(sketch, "E72.0", {"start": v(3786.97, -2245.38) * mm, "mid": v(3711.73, -2043.1) * mm, "end": v(3686.18, -1828.8) * mm});
            skLineSegment(sketch, "E73", {"start": v(4597.37, -1784.35) * mm, "end": v(4597.37, -1828.76) * mm});
            skLineSegment(sketch, "E74", {"start": v(3686.18, -1828.8) * mm, "end": v(3686.18, -1784.35) * mm});
            skLineSegment(sketch, "E75.trimOffspring", {"start": v(4597.37, -1784.35) * mm, "end": v(4597.4, -1784.35) * mm});
            skLineSegment(sketch, "E76.trimOffspring", {"start": v(3683, -1828.8) * mm, "end": v(3657.6, -1828.8) * mm});
            skLineSegment(sketch, "E77.trimOffspring", {"start": v(3786.97, -2245.38) * mm, "end": v(4575.18, -1790.3) * mm});
            skSolve(sketch);
        }
        {
            var Q0;
            Q0=qSketchRegion(id+"F55",true);
            extrude(context, id + "F56", {"entities" : qUnion([Q0]), "oppositeDirection" : true, "depth" : 25.4 * mm});
        }
        {
            var Q0;
            Q0=qCreatedBy(id+"F17.planeOp",FACE);
            var sketch = newSketch(context, id + "F57", { "sketchPlane" : qUnion([Q0])});
            skLineSegment(sketch, "E78", {"start": v(3657.6, 0) * mm, "end": v(3657.6, 2095.5) * mm});
            skLineSegment(sketch, "E79", {"start": v(3657.6, 2095.5) * mm, "end": v(4622.8, 2095.5) * mm});
            skLineSegment(sketch, "E80", {"start": v(4622.8, 2095.5) * mm, "end": v(4622.8, 0) * mm});
            skLineSegment(sketch, "E81", {"start": v(4622.8, 0) * mm, "end": v(4597.4, 0) * mm});
            skLineSegment(sketch, "E82", {"start": v(4597.4, 0) * mm, "end": v(4597.4, 38.1) * mm});
            skLineSegment(sketch, "E83", {"start": v(4597.4, 38.1) * mm, "end": v(3683, 38.1) * mm});
            skLineSegment(sketch, "E84", {"start": v(3683, 38.1) * mm, "end": v(3683, 0) * mm});
            skLineSegment(sketch, "E85", {"start": v(3683, 0) * mm, "end": v(3657.6, 0) * mm});
            skSolve(sketch);
        }
        {
            var Q0;
            Q0=qSketchRegion(id+"F57",true);
            extrude(context, id + "F58", {"entities" : qUnion([Q0]), "oppositeDirection" : true, "depth" : 114.3 * mm});
        }
        {
            var Q0;
            Q0=makeQuery(id+"F58.opExtrude","CAP_FACE",FACE,{"disambiguationData":[OSD([sQuery(id+"F57.wireOp",EDGE,"E78"),sQuery(id+"F57.wireOp",EDGE,"E79"),sQuery(id+"F57.wireOp",EDGE,"E80"),sQuery(id+"F57.wireOp",EDGE,"E81"),sQuery(id+"F57.wireOp",EDGE,"E82"),sQuery(id+"F57.wireOp",EDGE,"E83"),sQuery(id+"F57.wireOp",EDGE,"E84"),sQuery(id+"F57.wireOp",EDGE,"E85")])],"isStart":true});
            var sketch = newSketch(context, id + "F59", { "sketchPlane" : qUnion([Q0])});
            skLineSegment(sketch, "E86.bottom", {"start": v(3683, 38.1) * mm, "end": v(4597.4, 38.1) * mm});
            skLineSegment(sketch, "E86.top", {"start": v(3683, 2070.1) * mm, "end": v(4597.4, 2070.1) * mm});
            skLineSegment(sketch, "E86.left", {"start": v(3683, 38.1) * mm, "end": v(3683, 2070.1) * mm});
            skLineSegment(sketch, "E86.right", {"start": v(4597.4, 38.1) * mm, "end": v(4597.4, 2070.1) * mm});
            skSolve(sketch);
        }
        {
            var Q0;
            Q0=qSketchRegion(id+"F59",true);
            extrude(context, id + "F60", {"entities" : qUnion([Q0]), "operationType" : NewBodyOperationType.REMOVE, "oppositeDirection" : true, "depth" : 79.38 * mm});
        }
        {
            var Q0;
            Q0=makeQuery(id+"F58.opExtrude","CAP_FACE",FACE,{"disambiguationData":[OSD([sQuery(id+"F57.wireOp",EDGE,"E78"),sQuery(id+"F57.wireOp",EDGE,"E79"),sQuery(id+"F57.wireOp",EDGE,"E80"),sQuery(id+"F57.wireOp",EDGE,"E81"),sQuery(id+"F57.wireOp",EDGE,"E82"),sQuery(id+"F57.wireOp",EDGE,"E83"),sQuery(id+"F57.wireOp",EDGE,"E84"),sQuery(id+"F57.wireOp",EDGE,"E85")])],"isStart":false});
            var sketch = newSketch(context, id + "F61", { "sketchPlane" : qUnion([Q0])});
            skLineSegment(sketch, "E87.0.0", {"start": v(-3683, 38.1) * mm, "end": v(-4597.4, 38.1) * mm});
            skLineSegment(sketch, "E87.0.1", {"start": v(-4597.4, 38.1) * mm, "end": v(-4597.4, 2070.1) * mm});
            skLineSegment(sketch, "E87.0.2", {"start": v(-4597.4, 2070.1) * mm, "end": v(-3683, 2070.1) * mm});
            skLineSegment(sketch, "E87.0.3", {"start": v(-3683, 2070.1) * mm, "end": v(-3683, 38.1) * mm});
            skSolve(sketch);
        }
        {
            var Q0;
            Q0=qSketchRegion(id+"F61",true);
            extrude(context, id + "F62", {"entities" : qUnion([Q0]), "operationType" : NewBodyOperationType.REMOVE, "oppositeDirection" : true, "depth" : 1.59 * mm});
        }
        {
            var Q0;
            Q0=makeQuery(id+"F58.opExtrude","SWEPT_FACE",FACE,{"disambiguationData":[OSD([sQuery(id+"F57.wireOp",EDGE,"E85")])]});
            var sketch = newSketch(context, id + "F63", { "sketchPlane" : qUnion([Q0])});
            skLineSegment(sketch, "E88", {"start": v(3657.6, -4267.2) * mm, "end": v(3657.6, -4152.9) * mm});
            skLineSegment(sketch, "E89", {"start": v(3657.6, -4152.9) * mm, "end": v(3683, -4152.9) * mm});
            skLineSegment(sketch, "E90", {"start": v(3683, -4152.9) * mm, "end": v(3683, -4232.27) * mm});
            skLineSegment(sketch, "E91", {"start": v(3683, -4232.27) * mm, "end": v(3686.18, -4232.27) * mm});
            skLineSegment(sketch, "E92", {"start": v(4597.4, -4232.27) * mm, "end": v(4597.4, -4152.9) * mm});
            skLineSegment(sketch, "E93", {"start": v(4597.4, -4152.9) * mm, "end": v(4622.8, -4152.9) * mm});
            skLineSegment(sketch, "E94", {"start": v(4622.8, -4152.9) * mm, "end": v(4622.8, -4267.2) * mm});
            skLineSegment(sketch, "E95", {"start": v(4622.8, -4267.2) * mm, "end": v(4597.4, -4267.2) * mm});
            skLineSegment(sketch, "E96", {"start": v(4597.4, -4267.2) * mm, "end": v(3805.5, -4724.4) * mm});
            skLineSegment(sketch, "E97", {"start": v(3805.5, -4724.4) * mm, "end": v(3788.04, -4694.15) * mm});
            skLineSegment(sketch, "E98", {"start": v(3788.04, -4694.15) * mm, "end": v(3788.62, -4693.82) * mm});
            skLineSegment(sketch, "E99", {"start": v(4579.94, -4236.95) * mm, "end": v(4597.37, -4267.16) * mm});
            skArc(sketch, "E100", {"start": v(3788.62, -4693.82) * mm, "mid": v(3709.8, -4486.95) * mm, "end": v(3683, -4267.2) * mm});
            skArc(sketch, "E101.0", {"start": v(3791.37, -4692.23) * mm, "mid": v(3712.87, -4486.13) * mm, "end": v(3686.18, -4267.2) * mm});
            skLineSegment(sketch, "E102", {"start": v(3686.18, -4267.2) * mm, "end": v(3686.18, -4232.27) * mm});
            skLineSegment(sketch, "E103.trimOffspring", {"start": v(3683, -4267.2) * mm, "end": v(3657.6, -4267.2) * mm});
            skLineSegment(sketch, "E104.trimOffspring", {"start": v(3791.37, -4692.23) * mm, "end": v(4579.94, -4236.95) * mm});
            skLineSegment(sketch, "E105", {"start": v(4597.37, -4232.27) * mm, "end": v(4597.37, -4267.16) * mm});
            skLineSegment(sketch, "E106.trimOffspring", {"start": v(4597.37, -4232.27) * mm, "end": v(4597.4, -4232.27) * mm});
            skSolve(sketch);
        }
        {
            var Q0;
            Q0=qSketchRegion(id+"F63",true);
            extrude(context, id + "F64", {"entities" : qUnion([Q0]), "oppositeDirection" : true, "depth" : 25.4 * mm});
        }
        {
            var Q0;
            Q0=qCreatedBy(id+"F26.planeOp",FACE);
            var sketch = newSketch(context, id + "F65", { "sketchPlane" : qUnion([Q0])});
            skLineSegment(sketch, "E107", {"start": v(3657.6, 0) * mm, "end": v(3657.6, 2095.5) * mm});
            skLineSegment(sketch, "E108", {"start": v(3657.6, 2095.5) * mm, "end": v(4521.2, 2095.5) * mm});
            skLineSegment(sketch, "E109", {"start": v(4521.2, 2095.5) * mm, "end": v(4521.2, 0) * mm});
            skLineSegment(sketch, "E110", {"start": v(4521.2, 0) * mm, "end": v(4495.8, 0) * mm});
            skLineSegment(sketch, "E111", {"start": v(4495.8, 0) * mm, "end": v(4495.8, 38.1) * mm});
            skLineSegment(sketch, "E112", {"start": v(4495.8, 38.1) * mm, "end": v(3683, 38.1) * mm});
            skLineSegment(sketch, "E113", {"start": v(3683, 38.1) * mm, "end": v(3683, 0) * mm});
            skLineSegment(sketch, "E114", {"start": v(3683, 0) * mm, "end": v(3657.6, 0) * mm});
            skSolve(sketch);
        }
        {
            var Q0;
            Q0=qSketchRegion(id+"F65",true);
            extrude(context, id + "F66", {"entities" : qUnion([Q0]), "oppositeDirection" : true, "depth" : 114.3 * mm});
        }
        {
            var Q0;
            Q0=makeQuery(id+"F66.opExtrude","CAP_FACE",FACE,{"disambiguationData":[OSD([sQuery(id+"F65.wireOp",EDGE,"E107"),sQuery(id+"F65.wireOp",EDGE,"E108"),sQuery(id+"F65.wireOp",EDGE,"E109"),sQuery(id+"F65.wireOp",EDGE,"E110"),sQuery(id+"F65.wireOp",EDGE,"E111"),sQuery(id+"F65.wireOp",EDGE,"E112"),sQuery(id+"F65.wireOp",EDGE,"E113"),sQuery(id+"F65.wireOp",EDGE,"E114")])],"isStart":true});
            var sketch = newSketch(context, id + "F67", { "sketchPlane" : qUnion([Q0])});
            skLineSegment(sketch, "E115.bottom", {"start": v(3683, 38.1) * mm, "end": v(4495.8, 38.1) * mm});
            skLineSegment(sketch, "E115.top", {"start": v(3683, 2070.1) * mm, "end": v(4495.8, 2070.1) * mm});
            skLineSegment(sketch, "E115.left", {"start": v(3683, 38.1) * mm, "end": v(3683, 2070.1) * mm});
            skLineSegment(sketch, "E115.right", {"start": v(4495.8, 38.1) * mm, "end": v(4495.8, 2070.1) * mm});
            skSolve(sketch);
        }
        {
            var Q0;
            Q0=qSketchRegion(id+"F67",true);
            extrude(context, id + "F68", {"entities" : qUnion([Q0]), "operationType" : NewBodyOperationType.REMOVE, "oppositeDirection" : true, "depth" : 79.38 * mm});
        }
        {
            var Q0;
            Q0=makeQuery(id+"F66.opExtrude","CAP_FACE",FACE,{"disambiguationData":[OSD([sQuery(id+"F65.wireOp",EDGE,"E107"),sQuery(id+"F65.wireOp",EDGE,"E108"),sQuery(id+"F65.wireOp",EDGE,"E109"),sQuery(id+"F65.wireOp",EDGE,"E110"),sQuery(id+"F65.wireOp",EDGE,"E111"),sQuery(id+"F65.wireOp",EDGE,"E112"),sQuery(id+"F65.wireOp",EDGE,"E113"),sQuery(id+"F65.wireOp",EDGE,"E114")])],"isStart":false});
            var sketch = newSketch(context, id + "F69", { "sketchPlane" : qUnion([Q0])});
            skLineSegment(sketch, "E116.0.0", {"start": v(-3683, 38.1) * mm, "end": v(-4495.8, 38.1) * mm});
            skLineSegment(sketch, "E116.0.1", {"start": v(-4495.8, 38.1) * mm, "end": v(-4495.8, 2070.1) * mm});
            skLineSegment(sketch, "E116.0.2", {"start": v(-4495.8, 2070.1) * mm, "end": v(-3683, 2070.1) * mm});
            skLineSegment(sketch, "E116.0.3", {"start": v(-3683, 2070.1) * mm, "end": v(-3683, 38.1) * mm});
            skSolve(sketch);
        }
        {
            var Q0;
            Q0=qSketchRegion(id+"F69",true);
            extrude(context, id + "F70", {"entities" : qUnion([Q0]), "operationType" : NewBodyOperationType.REMOVE, "oppositeDirection" : true, "depth" : 1.59 * mm});
        }
        {
            var Q0;
            Q0=makeQuery(id+"F66.opExtrude","SWEPT_FACE",FACE,{"disambiguationData":[OSD([sQuery(id+"F65.wireOp",EDGE,"E114")])]});
            var sketch = newSketch(context, id + "F71", { "sketchPlane" : qUnion([Q0])});
            skLineSegment(sketch, "E117", {"start": v(3657.6, -6705.6) * mm, "end": v(3657.6, -6591.3) * mm});
            skLineSegment(sketch, "E118", {"start": v(3657.6, -6591.3) * mm, "end": v(3683, -6591.3) * mm});
            skLineSegment(sketch, "E119", {"start": v(3683, -6591.3) * mm, "end": v(3683, -6670.68) * mm});
            skLineSegment(sketch, "E120", {"start": v(3683, -6670.68) * mm, "end": v(3686.18, -6670.68) * mm});
            skLineSegment(sketch, "E121", {"start": v(4495.8, -6670.68) * mm, "end": v(4495.8, -6591.3) * mm});
            skLineSegment(sketch, "E122", {"start": v(4495.8, -6591.3) * mm, "end": v(4521.2, -6591.3) * mm});
            skLineSegment(sketch, "E123", {"start": v(4521.2, -6591.3) * mm, "end": v(4521.2, -6705.6) * mm});
            skLineSegment(sketch, "E124", {"start": v(4521.2, -6705.6) * mm, "end": v(4495.8, -6705.6) * mm});
            skLineSegment(sketch, "E125", {"start": v(4495.8, -6705.6) * mm, "end": v(3791.9, -7112) * mm});
            skLineSegment(sketch, "E126", {"start": v(3791.9, -7112) * mm, "end": v(3774.43, -7081.75) * mm});
            skLineSegment(sketch, "E127", {"start": v(3774.43, -7081.75) * mm, "end": v(3775.08, -7081.38) * mm});
            skLineSegment(sketch, "E128", {"start": v(4478.34, -6675.35) * mm, "end": v(4495.8, -6705.6) * mm});
            skArc(sketch, "E129", {"start": v(3775.08, -7081.38) * mm, "mid": v(3706.36, -6899.05) * mm, "end": v(3683, -6705.6) * mm});
            skArc(sketch, "E130.0", {"start": v(3777.83, -7079.79) * mm, "mid": v(3709.42, -6898.23) * mm, "end": v(3686.18, -6705.6) * mm});
            skLineSegment(sketch, "E131.trimOffspring", {"start": v(3683, -6705.6) * mm, "end": v(3657.6, -6705.6) * mm});
            skLineSegment(sketch, "E132.trimOffspring", {"start": v(3777.83, -7079.79) * mm, "end": v(4478.34, -6675.35) * mm});
            skLineSegment(sketch, "E133", {"start": v(3686.18, -6705.6) * mm, "end": v(3686.18, -6670.68) * mm});
            skLineSegment(sketch, "E134", {"start": v(4495.77, -6670.68) * mm, "end": v(4495.77, -6705.56) * mm});
            skLineSegment(sketch, "E135.trimOffspring", {"start": v(4495.77, -6670.68) * mm, "end": v(4495.8, -6670.68) * mm});
            skSolve(sketch);
        }
        {
            var Q0;
            Q0=qSketchRegion(id+"F71",true);
            extrude(context, id + "F72", {"entities" : qUnion([Q0]), "oppositeDirection" : true, "depth" : 25.4 * mm});
        }
        {
            var Q0;
            Q0=qCreatedBy(id+"F26.planeOp",FACE);
            cPlane(context, id + "F73", {"entities" : qUnion([Q0]), "cplaneType" : CPlaneType.OFFSET, "offset" : 2438.4 * mm, "oppositeDirection" : true, "width" : 152.4 * mm, "height" : 152.4 * mm});
        }
        {
            var Q0;
            Q0=qCreatedBy(id+"F73.planeOp",FACE);
            cPlane(context, id + "F74", {"entities" : qUnion([Q0]), "cplaneType" : CPlaneType.OFFSET, "offset" : 2438.4 * mm, "oppositeDirection" : true, "width" : 152.4 * mm, "height" : 152.4 * mm});
        }
        {
            var Q0;
            Q0=qCreatedBy(id+"F73.planeOp",FACE);
            var sketch = newSketch(context, id + "F75", { "sketchPlane" : qUnion([Q0])});
            skLineSegment(sketch, "E136", {"start": v(3657.6, 0) * mm, "end": v(3657.6, 2095.5) * mm});
            skLineSegment(sketch, "E137", {"start": v(3657.6, 2095.5) * mm, "end": v(4470.4, 2095.5) * mm});
            skLineSegment(sketch, "E138", {"start": v(4470.4, 2095.5) * mm, "end": v(4470.4, 0) * mm});
            skLineSegment(sketch, "E139", {"start": v(4470.4, 0) * mm, "end": v(4445, 0) * mm});
            skLineSegment(sketch, "E140", {"start": v(4445, 0) * mm, "end": v(4445, 38.1) * mm});
            skLineSegment(sketch, "E141", {"start": v(4445, 38.1) * mm, "end": v(3683, 38.1) * mm});
            skLineSegment(sketch, "E142", {"start": v(3683, 38.1) * mm, "end": v(3683, 0) * mm});
            skLineSegment(sketch, "E143", {"start": v(3683, 0) * mm, "end": v(3657.6, 0) * mm});
            skSolve(sketch);
        }
        {
            var Q0;
            Q0=qSketchRegion(id+"F75",true);
            extrude(context, id + "F76", {"entities" : qUnion([Q0]), "oppositeDirection" : true, "depth" : 114.3 * mm});
        }
        {
            var Q0;
            Q0=makeQuery(id+"F76.opExtrude","CAP_FACE",FACE,{"disambiguationData":[OSD([sQuery(id+"F75.wireOp",EDGE,"E136"),sQuery(id+"F75.wireOp",EDGE,"E137"),sQuery(id+"F75.wireOp",EDGE,"E138"),sQuery(id+"F75.wireOp",EDGE,"E139"),sQuery(id+"F75.wireOp",EDGE,"E140"),sQuery(id+"F75.wireOp",EDGE,"E141"),sQuery(id+"F75.wireOp",EDGE,"E142"),sQuery(id+"F75.wireOp",EDGE,"E143")])],"isStart":true});
            var sketch = newSketch(context, id + "F77", { "sketchPlane" : qUnion([Q0])});
            skLineSegment(sketch, "E144.bottom", {"start": v(3683, 38.1) * mm, "end": v(4445, 38.1) * mm});
            skLineSegment(sketch, "E144.top", {"start": v(3683, 2070.1) * mm, "end": v(4445, 2070.1) * mm});
            skLineSegment(sketch, "E144.left", {"start": v(3683, 38.1) * mm, "end": v(3683, 2070.1) * mm});
            skLineSegment(sketch, "E144.right", {"start": v(4445, 38.1) * mm, "end": v(4445, 2070.1) * mm});
            skSolve(sketch);
        }
        {
            var Q0;
            Q0=qSketchRegion(id+"F77",true);
            extrude(context, id + "F78", {"entities" : qUnion([Q0]), "operationType" : NewBodyOperationType.REMOVE, "oppositeDirection" : true, "depth" : 79.38 * mm});
        }
        {
            var Q0;
            Q0=makeQuery(id+"F76.opExtrude","CAP_FACE",FACE,{"disambiguationData":[OSD([sQuery(id+"F75.wireOp",EDGE,"E136"),sQuery(id+"F75.wireOp",EDGE,"E137"),sQuery(id+"F75.wireOp",EDGE,"E138"),sQuery(id+"F75.wireOp",EDGE,"E139"),sQuery(id+"F75.wireOp",EDGE,"E140"),sQuery(id+"F75.wireOp",EDGE,"E141"),sQuery(id+"F75.wireOp",EDGE,"E142"),sQuery(id+"F75.wireOp",EDGE,"E143")])],"isStart":false});
            var sketch = newSketch(context, id + "F79", { "sketchPlane" : qUnion([Q0])});
            skLineSegment(sketch, "E145.0.0", {"start": v(-3683, 38.1) * mm, "end": v(-4445, 38.1) * mm});
            skLineSegment(sketch, "E145.0.1", {"start": v(-4445, 38.1) * mm, "end": v(-4445, 2070.1) * mm});
            skLineSegment(sketch, "E145.0.2", {"start": v(-4445, 2070.1) * mm, "end": v(-3683, 2070.1) * mm});
            skLineSegment(sketch, "E145.0.3", {"start": v(-3683, 2070.1) * mm, "end": v(-3683, 38.1) * mm});
            skSolve(sketch);
        }
        {
            var Q0;
            Q0=qSketchRegion(id+"F79",true);
            extrude(context, id + "F80", {"entities" : qUnion([Q0]), "operationType" : NewBodyOperationType.REMOVE, "oppositeDirection" : true, "depth" : 1.59 * mm});
        }
        {
            var Q0;
            Q0=makeQuery(id+"F76.opExtrude","SWEPT_FACE",FACE,{"disambiguationData":[OSD([sQuery(id+"F75.wireOp",EDGE,"E143")])]});
            var sketch = newSketch(context, id + "F81", { "sketchPlane" : qUnion([Q0])});
            skLineSegment(sketch, "E146", {"start": v(3657.6, -9029.7) * mm, "end": v(3657.6, -9144) * mm});
            skLineSegment(sketch, "E147", {"start": v(3657.6, -9144) * mm, "end": v(3683, -9144) * mm});
            skLineSegment(sketch, "E148", {"start": v(4470.4, -9144) * mm, "end": v(4470.4, -9029.7) * mm});
            skLineSegment(sketch, "E149", {"start": v(4470.4, -9029.7) * mm, "end": v(4445, -9029.7) * mm});
            skLineSegment(sketch, "E150", {"start": v(4445, -9029.7) * mm, "end": v(4445, -9109.08) * mm});
            skLineSegment(sketch, "E151", {"start": v(4445, -9109.08) * mm, "end": v(4444.97, -9109.08) * mm});
            skLineSegment(sketch, "E152", {"start": v(3683, -9109.08) * mm, "end": v(3683, -9029.7) * mm});
            skLineSegment(sketch, "E153", {"start": v(3683, -9029.7) * mm, "end": v(3657.6, -9029.7) * mm});
            skLineSegment(sketch, "E154", {"start": v(4445, -9144) * mm, "end": v(3785.09, -9525) * mm});
            skLineSegment(sketch, "E155", {"start": v(3785.09, -9525) * mm, "end": v(3767.63, -9494.75) * mm});
            skLineSegment(sketch, "E156", {"start": v(3767.63, -9494.75) * mm, "end": v(3768.32, -9494.35) * mm});
            skLineSegment(sketch, "E157", {"start": v(4427.54, -9113.75) * mm, "end": v(4444.97, -9143.96) * mm});
            skArc(sketch, "E158", {"start": v(3768.32, -9494.35) * mm, "mid": v(3704.64, -9324.3) * mm, "end": v(3683, -9144) * mm});
            skArc(sketch, "E159.0", {"start": v(3771.07, -9492.76) * mm, "mid": v(3707.7, -9323.47) * mm, "end": v(3686.18, -9144) * mm});
            skLineSegment(sketch, "E160.trimOffspring", {"start": v(4445, -9144) * mm, "end": v(4470.4, -9144) * mm});
            skLineSegment(sketch, "E161", {"start": v(3686.18, -9144) * mm, "end": v(3686.18, -9109.08) * mm});
            skLineSegment(sketch, "E162.trimOffspring", {"start": v(3771.07, -9492.76) * mm, "end": v(4427.54, -9113.75) * mm});
            skLineSegment(sketch, "E163", {"start": v(4444.97, -9109.08) * mm, "end": v(4444.97, -9143.96) * mm});
            skLineSegment(sketch, "E164.trimOffspring", {"start": v(3686.18, -9109.08) * mm, "end": v(3683, -9109.08) * mm});
            skSolve(sketch);
        }
        {
            var Q0;
            Q0=qSketchRegion(id+"F81",true);
            extrude(context, id + "F82", {"entities" : qUnion([Q0]), "oppositeDirection" : true, "depth" : 25.4 * mm});
        }
        {
            var Q0;
            Q0=qCreatedBy(id+"F74.planeOp",FACE);
            var sketch = newSketch(context, id + "F83", { "sketchPlane" : qUnion([Q0])});
            skLineSegment(sketch, "E165", {"start": v(3657.6, 0) * mm, "end": v(3657.6, 2095.5) * mm});
            skLineSegment(sketch, "E166", {"start": v(3657.6, 2095.5) * mm, "end": v(4419.6, 2095.5) * mm});
            skLineSegment(sketch, "E167", {"start": v(4419.6, 2095.5) * mm, "end": v(4419.6, 0) * mm});
            skLineSegment(sketch, "E168", {"start": v(4419.6, 0) * mm, "end": v(4394.2, 0) * mm});
            skLineSegment(sketch, "E169", {"start": v(4394.2, 0) * mm, "end": v(4394.2, 38.1) * mm});
            skLineSegment(sketch, "E170", {"start": v(4394.2, 38.1) * mm, "end": v(3683, 38.1) * mm});
            skLineSegment(sketch, "E171", {"start": v(3683, 38.1) * mm, "end": v(3683, 0) * mm});
            skLineSegment(sketch, "E172", {"start": v(3683, 0) * mm, "end": v(3657.6, 0) * mm});
            skSolve(sketch);
        }
        {
            var Q0;
            Q0=qSketchRegion(id+"F83",true);
            extrude(context, id + "F84", {"entities" : qUnion([Q0]), "oppositeDirection" : true, "depth" : 114.3 * mm});
        }
        {
            var Q0;
            Q0=makeQuery(id+"F84.opExtrude","CAP_FACE",FACE,{"disambiguationData":[OSD([sQuery(id+"F83.wireOp",EDGE,"E165"),sQuery(id+"F83.wireOp",EDGE,"E166"),sQuery(id+"F83.wireOp",EDGE,"E167"),sQuery(id+"F83.wireOp",EDGE,"E168"),sQuery(id+"F83.wireOp",EDGE,"E169"),sQuery(id+"F83.wireOp",EDGE,"E170"),sQuery(id+"F83.wireOp",EDGE,"E171"),sQuery(id+"F83.wireOp",EDGE,"E172")])],"isStart":true});
            var sketch = newSketch(context, id + "F85", { "sketchPlane" : qUnion([Q0])});
            skLineSegment(sketch, "E173.bottom", {"start": v(3683, 38.1) * mm, "end": v(4394.2, 38.1) * mm});
            skLineSegment(sketch, "E173.top", {"start": v(3683, 2070.1) * mm, "end": v(4394.2, 2070.1) * mm});
            skLineSegment(sketch, "E173.left", {"start": v(3683, 38.1) * mm, "end": v(3683, 2070.1) * mm});
            skLineSegment(sketch, "E173.right", {"start": v(4394.2, 38.1) * mm, "end": v(4394.2, 2070.1) * mm});
            skSolve(sketch);
        }
        {
            var Q0;
            Q0=qSketchRegion(id+"F85",true);
            extrude(context, id + "F86", {"entities" : qUnion([Q0]), "operationType" : NewBodyOperationType.REMOVE, "oppositeDirection" : true, "depth" : 79.38 * mm});
        }
        {
            var Q0;
            Q0=makeQuery(id+"F84.opExtrude","CAP_FACE",FACE,{"disambiguationData":[OSD([sQuery(id+"F83.wireOp",EDGE,"E165"),sQuery(id+"F83.wireOp",EDGE,"E166"),sQuery(id+"F83.wireOp",EDGE,"E167"),sQuery(id+"F83.wireOp",EDGE,"E168"),sQuery(id+"F83.wireOp",EDGE,"E169"),sQuery(id+"F83.wireOp",EDGE,"E170"),sQuery(id+"F83.wireOp",EDGE,"E171"),sQuery(id+"F83.wireOp",EDGE,"E172")])],"isStart":false});
            var sketch = newSketch(context, id + "F87", { "sketchPlane" : qUnion([Q0])});
            skLineSegment(sketch, "E174.0.0", {"start": v(-3683, 38.1) * mm, "end": v(-4394.2, 38.1) * mm});
            skLineSegment(sketch, "E174.0.1", {"start": v(-4394.2, 38.1) * mm, "end": v(-4394.2, 2070.1) * mm});
            skLineSegment(sketch, "E174.0.2", {"start": v(-4394.2, 2070.1) * mm, "end": v(-3683, 2070.1) * mm});
            skLineSegment(sketch, "E174.0.3", {"start": v(-3683, 2070.1) * mm, "end": v(-3683, 38.1) * mm});
            skSolve(sketch);
        }
        {
            var Q0;
            Q0=qSketchRegion(id+"F87",true);
            extrude(context, id + "F88", {"entities" : qUnion([Q0]), "operationType" : NewBodyOperationType.REMOVE, "oppositeDirection" : true, "depth" : 1.59 * mm});
        }
        {
            var Q0;
            Q0=makeQuery(id+"F84.opExtrude","SWEPT_FACE",FACE,{"disambiguationData":[OSD([sQuery(id+"F83.wireOp",EDGE,"E172")])]});
            var sketch = newSketch(context, id + "F89", { "sketchPlane" : qUnion([Q0])});
            skLineSegment(sketch, "E175", {"start": v(3657.6, -11468.1) * mm, "end": v(3657.6, -11582.4) * mm});
            skLineSegment(sketch, "E176", {"start": v(3657.6, -11582.4) * mm, "end": v(3683, -11582.4) * mm});
            skLineSegment(sketch, "E177", {"start": v(4419.6, -11582.4) * mm, "end": v(4419.6, -11468.1) * mm});
            skLineSegment(sketch, "E178", {"start": v(4419.6, -11468.1) * mm, "end": v(4394.2, -11468.1) * mm});
            skLineSegment(sketch, "E179", {"start": v(4394.2, -11468.1) * mm, "end": v(4394.2, -11547.48) * mm});
            skLineSegment(sketch, "E180", {"start": v(4394.2, -11547.48) * mm, "end": v(4394.17, -11547.48) * mm});
            skLineSegment(sketch, "E181", {"start": v(3683, -11547.48) * mm, "end": v(3683, -11468.1) * mm});
            skLineSegment(sketch, "E182", {"start": v(3683, -11468.1) * mm, "end": v(3657.6, -11468.1) * mm});
            skLineSegment(sketch, "E183", {"start": v(4394.2, -11582.4) * mm, "end": v(3778.28, -11938) * mm});
            skLineSegment(sketch, "E184", {"start": v(3778.28, -11938) * mm, "end": v(3760.82, -11907.75) * mm});
            skLineSegment(sketch, "E185", {"start": v(3760.82, -11907.75) * mm, "end": v(4376.74, -11552.15) * mm});
            skLineSegment(sketch, "E186", {"start": v(4376.74, -11552.15) * mm, "end": v(4394.17, -11582.36) * mm});
            skArc(sketch, "E187", {"start": v(3761.56, -11907.33) * mm, "mid": v(3702.92, -11749.54) * mm, "end": v(3683, -11582.4) * mm});
            skArc(sketch, "E188.0", {"start": v(3764.32, -11905.74) * mm, "mid": v(3705.99, -11748.72) * mm, "end": v(3686.18, -11582.4) * mm});
            skLineSegment(sketch, "E189", {"start": v(3686.18, -11582.4) * mm, "end": v(3686.18, -11547.48) * mm});
            skLineSegment(sketch, "E190", {"start": v(4394.17, -11547.48) * mm, "end": v(4394.17, -11582.36) * mm});
            skLineSegment(sketch, "E191.trimOffspring", {"start": v(4394.2, -11582.4) * mm, "end": v(4419.6, -11582.4) * mm});
            skLineSegment(sketch, "E192.trimOffspring", {"start": v(3686.18, -11547.48) * mm, "end": v(3683, -11547.48) * mm});
            skSolve(sketch);
        }
        {
            var Q0;
            Q0=qSketchRegion(id+"F89",true);
            extrude(context, id + "F90", {"entities" : qUnion([Q0]), "oppositeDirection" : true, "depth" : 25.4 * mm});
        }
        {
            var Q0;
            Q0=qCreatedBy(id+"F74.planeOp",FACE);
            cPlane(context, id + "F91", {"entities" : qUnion([Q0]), "cplaneType" : CPlaneType.OFFSET, "offset" : 2438.4 * mm, "oppositeDirection" : true, "width" : 152.4 * mm, "height" : 152.4 * mm});
        }
        {
            var Q0;
            Q0=qCreatedBy(id+"F91.planeOp",FACE);
            var sketch = newSketch(context, id + "F92", { "sketchPlane" : qUnion([Q0])});
            skLineSegment(sketch, "E193", {"start": v(3657.6, 0) * mm, "end": v(3657.6, 2076.45) * mm});
            skLineSegment(sketch, "E194", {"start": v(3657.6, 2076.45) * mm, "end": v(4902.2, 2076.45) * mm});
            skLineSegment(sketch, "E195", {"start": v(4902.2, 2076.45) * mm, "end": v(4902.2, 0) * mm});
            skLineSegment(sketch, "E196", {"start": v(4902.2, 0) * mm, "end": v(4889.5, 0) * mm});
            skLineSegment(sketch, "E197", {"start": v(4889.5, 0) * mm, "end": v(4889.5, 31.75) * mm});
            skLineSegment(sketch, "E198", {"start": v(4889.5, 31.75) * mm, "end": v(3670.3, 31.75) * mm});
            skLineSegment(sketch, "E199", {"start": v(3670.3, 31.75) * mm, "end": v(3670.3, 0) * mm});
            skLineSegment(sketch, "E200", {"start": v(3670.3, 0) * mm, "end": v(3657.6, 0) * mm});
            skSolve(sketch);
        }
        {
            var Q0;
            Q0=qSketchRegion(id+"F92",true);
            extrude(context, id + "F93", {"entities" : qUnion([Q0]), "oppositeDirection" : true, "depth" : 114.3 * mm});
        }
        {
            var Q0;
            Q0=makeQuery(id+"F93.opExtrude","CAP_FACE",FACE,{"disambiguationData":[OSD([sQuery(id+"F92.wireOp",EDGE,"E193"),sQuery(id+"F92.wireOp",EDGE,"E194"),sQuery(id+"F92.wireOp",EDGE,"E195"),sQuery(id+"F92.wireOp",EDGE,"E196"),sQuery(id+"F92.wireOp",EDGE,"E197"),sQuery(id+"F92.wireOp",EDGE,"E198"),sQuery(id+"F92.wireOp",EDGE,"E199"),sQuery(id+"F92.wireOp",EDGE,"E200")])],"isStart":true});
            var sketch = newSketch(context, id + "F94", { "sketchPlane" : qUnion([Q0])});
            skLineSegment(sketch, "E201.bottom", {"start": v(3670.3, 31.75) * mm, "end": v(4889.5, 31.75) * mm});
            skLineSegment(sketch, "E201.top", {"start": v(3670.3, 2063.75) * mm, "end": v(4889.5, 2063.75) * mm});
            skLineSegment(sketch, "E201.left", {"start": v(3670.3, 31.75) * mm, "end": v(3670.3, 2063.75) * mm});
            skLineSegment(sketch, "E201.right", {"start": v(4889.5, 31.75) * mm, "end": v(4889.5, 2063.75) * mm});
            skSolve(sketch);
        }
        {
            var Q0;
            Q0=qSketchRegion(id+"F94",true);
            extrude(context, id + "F95", {"entities" : qUnion([Q0]), "operationType" : NewBodyOperationType.REMOVE, "oppositeDirection" : true, "depth" : 25.4 * mm});
        }
        {
            var Q0;
            Q0=makeQuery(id+"F93.opExtrude","CAP_FACE",FACE,{"disambiguationData":[OSD([sQuery(id+"F92.wireOp",EDGE,"E193"),sQuery(id+"F92.wireOp",EDGE,"E194"),sQuery(id+"F92.wireOp",EDGE,"E195"),sQuery(id+"F92.wireOp",EDGE,"E196"),sQuery(id+"F92.wireOp",EDGE,"E197"),sQuery(id+"F92.wireOp",EDGE,"E198"),sQuery(id+"F92.wireOp",EDGE,"E199"),sQuery(id+"F92.wireOp",EDGE,"E200")])],"isStart":false});
            var sketch = newSketch(context, id + "F96", { "sketchPlane" : qUnion([Q0])});
            skLineSegment(sketch, "E202.0.0", {"start": v(-3670.3, 31.75) * mm, "end": v(-4889.5, 31.75) * mm});
            skLineSegment(sketch, "E202.0.1", {"start": v(-4889.5, 31.75) * mm, "end": v(-4889.5, 2063.75) * mm});
            skLineSegment(sketch, "E202.0.2", {"start": v(-4889.5, 2063.75) * mm, "end": v(-3670.3, 2063.75) * mm});
            skLineSegment(sketch, "E202.0.3", {"start": v(-3670.3, 2063.75) * mm, "end": v(-3670.3, 31.75) * mm});
            skSolve(sketch);
        }
        {
            var Q0;
            Q0=qSketchRegion(id+"F96",true);
            extrude(context, id + "F97", {"entities" : qUnion([Q0]), "operationType" : NewBodyOperationType.REMOVE, "oppositeDirection" : true, "depth" : 57.15 * mm});
        }
        {
            var Q0;
            Q0=makeQuery(id+"F95.boolean.opBoolean","COPY",FACE,{"derivedFrom":makeQuery(id+"F95.opExtrude","CAP_FACE",FACE,{"disambiguationData":[OSD([sQuery(id+"F94.wireOp",EDGE,"E201.bottom"),sQuery(id+"F94.wireOp",EDGE,"E201.top"),sQuery(id+"F94.wireOp",EDGE,"E201.left"),sQuery(id+"F94.wireOp",EDGE,"E201.right")])],"isStart":false})});
            var sketch = newSketch(context, id + "F98", { "sketchPlane" : qUnion([Q0])});
            skLineSegment(sketch, "E203.bottom", {"start": v(3975.08, 31.75) * mm, "end": v(3975.1, 31.75) * mm});
            skLineSegment(sketch, "E203.top", {"start": v(3975.08, 2063.75) * mm, "end": v(3975.1, 2063.75) * mm});
            skLineSegment(sketch, "E203.left", {"start": v(3975.08, 31.75) * mm, "end": v(3975.08, 2063.75) * mm});
            skLineSegment(sketch, "E203.right", {"start": v(3975.1, 31.75) * mm, "end": v(3975.1, 2063.75) * mm});
            skLineSegment(sketch, "E204.bottom", {"start": v(4279.89, 31.75) * mm, "end": v(4279.91, 31.75) * mm});
            skLineSegment(sketch, "E204.top", {"start": v(4279.89, 2063.75) * mm, "end": v(4279.91, 2063.75) * mm});
            skLineSegment(sketch, "E204.left", {"start": v(4279.89, 31.75) * mm, "end": v(4279.89, 2063.75) * mm});
            skLineSegment(sketch, "E204.right", {"start": v(4279.91, 31.75) * mm, "end": v(4279.91, 2063.75) * mm});
            skLineSegment(sketch, "E205.bottom", {"start": v(4584.7, 31.75) * mm, "end": v(4584.72, 31.75) * mm});
            skLineSegment(sketch, "E205.top", {"start": v(4584.7, 2063.75) * mm, "end": v(4584.72, 2063.75) * mm});
            skLineSegment(sketch, "E205.left", {"start": v(4584.7, 31.75) * mm, "end": v(4584.7, 2063.75) * mm});
            skLineSegment(sketch, "E205.right", {"start": v(4584.72, 31.75) * mm, "end": v(4584.72, 2063.75) * mm});
            skLineSegment(sketch, "E206", {"start": v(3975.08, 1047.75) * mm, "end": v(3670.3, 1047.75) * mm, "construction": true});
            skLineSegment(sketch, "E207", {"start": v(3975.1, 1047.75) * mm, "end": v(4279.89, 1047.75) * mm, "construction": true});
            skLineSegment(sketch, "E208", {"start": v(4279.91, 1047.75) * mm, "end": v(4584.7, 1047.75) * mm, "construction": true});
            skLineSegment(sketch, "E209", {"start": v(4584.72, 1047.75) * mm, "end": v(4889.5, 1047.75) * mm, "construction": true});
            skSolve(sketch);
        }
        {
            var Q0;
            Q0=qSketchRegion(id+"F98",true);
            extrude(context, id + "F99", {"entities" : qUnion([Q0]), "operationType" : NewBodyOperationType.REMOVE, "oppositeDirection" : true, "depth" : 38.1 * mm});
        }
        {
            var Q0;
            Q0=makeQuery(id+"F93.opExtrude","SWEPT_FACE",FACE,{"disambiguationData":[OSD([sQuery(id+"F92.wireOp",EDGE,"E200")])]});
            var sketch = newSketch(context, id + "F100", { "sketchPlane" : qUnion([Q0])});
            skLineSegment(sketch, "E210", {"start": v(3657.6, -13906.5) * mm, "end": v(3657.6, -14020.8) * mm});
            skLineSegment(sketch, "E211", {"start": v(3657.6, -14020.8) * mm, "end": v(3670.3, -14020.8) * mm});
            skLineSegment(sketch, "E212", {"start": v(3670.3, -14020.8) * mm, "end": v(3670.3, -13963.65) * mm});
            skLineSegment(sketch, "E213", {"start": v(3670.3, -13963.65) * mm, "end": v(4889.5, -13963.65) * mm, "construction": true});
            skLineSegment(sketch, "E214", {"start": v(4889.5, -13963.65) * mm, "end": v(4889.5, -14020.8) * mm});
            skLineSegment(sketch, "E215", {"start": v(4889.5, -14020.8) * mm, "end": v(4902.2, -14020.8) * mm});
            skLineSegment(sketch, "E216", {"start": v(4902.2, -14020.8) * mm, "end": v(4902.2, -13906.5) * mm});
            skLineSegment(sketch, "E217", {"start": v(4902.2, -13906.5) * mm, "end": v(4889.5, -13906.5) * mm});
            skLineSegment(sketch, "E218", {"start": v(4889.5, -13906.5) * mm, "end": v(4889.5, -13931.9) * mm});
            skLineSegment(sketch, "E219", {"start": v(4889.5, -13931.9) * mm, "end": v(4870.63, -13931.9) * mm});
            skLineSegment(sketch, "E220", {"start": v(3670.3, -13931.9) * mm, "end": v(3670.3, -13906.5) * mm});
            skLineSegment(sketch, "E221", {"start": v(3670.3, -13906.5) * mm, "end": v(3657.6, -13906.5) * mm});
            skLineSegment(sketch, "E222", {"start": v(3670.3, -13963.65) * mm, "end": v(3670.3, -13931.93) * mm});
            skLineSegment(sketch, "E223", {"start": v(4889.5, -13963.65) * mm, "end": v(4889.5, -13931.93) * mm});
            skLineSegment(sketch, "E224", {"start": v(4889.5, -13947.77) * mm, "end": v(3670.3, -13947.77) * mm, "construction": true});
            skLineSegment(sketch, "E225", {"start": v(3676.65, -13953.59) * mm, "end": v(3704.15, -13969.46) * mm});
            skLineSegment(sketch, "E226", {"start": v(3704.15, -13969.46) * mm, "end": v(3725.82, -13931.93) * mm});
            skLineSegment(sketch, "E227", {"start": v(3855.17, -13704.7) * mm, "end": v(3829.05, -13689.62) * mm});
            skLineSegment(sketch, "E228", {"start": v(3829.05, -13689.62) * mm, "end": v(3689.17, -13931.9) * mm});
            skLineSegment(sketch, "E229", {"start": v(3857.34, -13706.87) * mm, "end": v(3987.26, -13931.9) * mm});
            skLineSegment(sketch, "E230", {"start": v(4008.95, -13969.46) * mm, "end": v(4036.44, -13953.59) * mm});
            skLineSegment(sketch, "E231", {"start": v(4036.44, -13953.59) * mm, "end": v(4023.94, -13931.93) * mm});
            skLineSegment(sketch, "E232", {"start": v(3884.04, -13689.62) * mm, "end": v(3857.92, -13704.7) * mm});
            skLineSegment(sketch, "E233", {"start": v(3690.4, -13961.52) * mm, "end": v(3698.34, -13947.77) * mm, "construction": true});
            skLineSegment(sketch, "E234", {"start": v(4022.7, -13961.52) * mm, "end": v(4014.76, -13947.77) * mm, "construction": true});
            skArc(sketch, "E235", {"start": v(3855.75, -13706.87) * mm, "mid": v(3856.55, -13707.08) * mm, "end": v(3857.34, -13706.87) * mm});
            skLineSegment(sketch, "E236", {"start": v(3670.3, -13931.93) * mm, "end": v(3689.16, -13931.93) * mm});
            skLineSegment(sketch, "E237.trimOffspring", {"start": v(3689.16, -13931.93) * mm, "end": v(3676.65, -13953.59) * mm});
            skLineSegment(sketch, "E238.trimOffspring", {"start": v(3725.82, -13931.93) * mm, "end": v(3987.28, -13931.93) * mm});
            skLineSegment(sketch, "E239.trimOffspring", {"start": v(3689.17, -13931.9) * mm, "end": v(3670.3, -13931.9) * mm});
            skLineSegment(sketch, "E240.trimOffspring", {"start": v(3725.83, -13931.9) * mm, "end": v(3855.75, -13706.87) * mm});
            skLineSegment(sketch, "E241.trimOffspring", {"start": v(4023.92, -13931.9) * mm, "end": v(3884.04, -13689.62) * mm});
            skLineSegment(sketch, "E242.trimOffspring", {"start": v(4023.94, -13931.93) * mm, "end": v(4535.86, -13931.93) * mm});
            skLineSegment(sketch, "E243.trimOffspring", {"start": v(3987.28, -13931.93) * mm, "end": v(4008.95, -13969.46) * mm});
            skLineSegment(sketch, "E244.trimOffspring", {"start": v(3987.26, -13931.9) * mm, "end": v(3725.83, -13931.9) * mm});
            skLineSegment(sketch, "E245", {"start": v(4855.65, -13969.46) * mm, "end": v(4883.15, -13953.59) * mm});
            skLineSegment(sketch, "E246", {"start": v(4883.15, -13953.59) * mm, "end": v(4870.64, -13931.93) * mm});
            skLineSegment(sketch, "E247", {"start": v(4730.75, -13689.62) * mm, "end": v(4704.63, -13704.7) * mm});
            skLineSegment(sketch, "E248", {"start": v(4704.05, -13706.87) * mm, "end": v(4833.97, -13931.9) * mm});
            skLineSegment(sketch, "E249", {"start": v(4702.46, -13706.87) * mm, "end": v(4572.54, -13931.9) * mm});
            skLineSegment(sketch, "E250", {"start": v(4550.85, -13969.46) * mm, "end": v(4523.36, -13953.59) * mm});
            skLineSegment(sketch, "E251", {"start": v(4523.36, -13953.59) * mm, "end": v(4535.86, -13931.93) * mm});
            skLineSegment(sketch, "E252", {"start": v(4675.76, -13689.62) * mm, "end": v(4701.88, -13704.7) * mm});
            skLineSegment(sketch, "E253.trimOffspring", {"start": v(4535.88, -13931.9) * mm, "end": v(4675.76, -13689.62) * mm});
            skLineSegment(sketch, "E254.trimOffspring", {"start": v(4572.52, -13931.93) * mm, "end": v(4833.98, -13931.93) * mm});
            skLineSegment(sketch, "E255.trimOffspring", {"start": v(4535.88, -13931.9) * mm, "end": v(4023.92, -13931.9) * mm});
            skLineSegment(sketch, "E256.trimOffspring", {"start": v(4572.52, -13931.93) * mm, "end": v(4550.85, -13969.46) * mm});
            skLineSegment(sketch, "E257.trimOffspring", {"start": v(4833.98, -13931.93) * mm, "end": v(4855.65, -13969.46) * mm});
            skLineSegment(sketch, "E258.trimOffspring", {"start": v(4870.64, -13931.93) * mm, "end": v(4889.5, -13931.93) * mm});
            skLineSegment(sketch, "E259.trimOffspring", {"start": v(4833.97, -13931.9) * mm, "end": v(4572.54, -13931.9) * mm});
            skLineSegment(sketch, "E260.trimOffspring", {"start": v(4870.63, -13931.9) * mm, "end": v(4730.75, -13689.62) * mm});
            skArc(sketch, "E261", {"start": v(4702.46, -13706.87) * mm, "mid": v(4703.25, -13707.08) * mm, "end": v(4704.05, -13706.87) * mm});
            skArc(sketch, "E262.trimOffspring", {"start": v(4704.63, -13704.7) * mm, "mid": v(4703.25, -13703.9) * mm, "end": v(4701.88, -13704.7) * mm});
            skArc(sketch, "E263.trimOffspring", {"start": v(3857.92, -13704.7) * mm, "mid": v(3856.55, -13703.9) * mm, "end": v(3855.17, -13704.7) * mm});
            skSolve(sketch);
        }
        {
            var Q0;
            Q0=makeQuery(id+"F100.imprint","IMPRINT",FACE,{"disambiguationData":[TD([[makeQuery(id+"F100.imprint","IMPRINT",EDGE,{"derivedFrom":sQuery(id+"F100.wireOp",EDGE,"E210")}),1.0]])]});
            extrude(context, id + "F101", {"entities" : qUnion([Q0]), "oppositeDirection" : true, "depth" : 25.4 * mm});
        }
        {
            var Q0;
            Q0=qCreatedBy(makeId("Front.planeOp"),FACE);
            var sketch = newSketch(context, id + "F102", { "sketchPlane" : qUnion([Q0])});
            skLineSegment(sketch, "E264.bottom", {"start": v(7315.2, 0) * mm, "end": v(10058.4, 0) * mm});
            skLineSegment(sketch, "E264.top", {"start": v(7315.2, 2438.4) * mm, "end": v(10058.4, 2438.4) * mm});
            skLineSegment(sketch, "E264.left", {"start": v(7315.2, 0) * mm, "end": v(7315.2, 2438.4) * mm});
            skLineSegment(sketch, "E264.right", {"start": v(10058.4, 0) * mm, "end": v(10058.4, 2438.4) * mm});
            skSolve(sketch);
        }
        {
            var Q0;
            Q0=qSketchRegion(id+"F102",true);
            extrude(context, id + "F103", {"entities" : qUnion([Q0]), "oppositeDirection" : true, "depth" : 203.2 * mm});
        }
        {
            var Q0;
            Q0=makeQuery(id+"F103.opExtrude","CAP_FACE",FACE,{"disambiguationData":[OSD([sQuery(id+"F102.wireOp",EDGE,"E264.bottom"),sQuery(id+"F102.wireOp",EDGE,"E264.top"),sQuery(id+"F102.wireOp",EDGE,"E264.left"),sQuery(id+"F102.wireOp",EDGE,"E264.right")])],"isStart":true});
            var sketch = newSketch(context, id + "F104", { "sketchPlane" : qUnion([Q0])});
            skLineSegment(sketch, "E265.bottom", {"start": v(7327.9, 0) * mm, "end": v(10045.7, 0) * mm});
            skLineSegment(sketch, "E265.top", {"start": v(7327.9, 2425.7) * mm, "end": v(10045.7, 2425.7) * mm});
            skLineSegment(sketch, "E265.left", {"start": v(7327.9, 0) * mm, "end": v(7327.9, 2425.7) * mm});
            skLineSegment(sketch, "E265.right", {"start": v(10045.7, 0) * mm, "end": v(10045.7, 2425.7) * mm});
            skSolve(sketch);
        }
        {
            var Q0;
            Q0=qSketchRegion(id+"F104",true);
            extrude(context, id + "F105", {"entities" : qUnion([Q0]), "operationType" : NewBodyOperationType.REMOVE, "oppositeDirection" : true, "depth" : 165.1 * mm});
        }
        {
            var Q0;
            Q0=makeQuery(id+"F103.opExtrude","CAP_FACE",FACE,{"disambiguationData":[OSD([sQuery(id+"F102.wireOp",EDGE,"E264.bottom"),sQuery(id+"F102.wireOp",EDGE,"E264.top"),sQuery(id+"F102.wireOp",EDGE,"E264.left"),sQuery(id+"F102.wireOp",EDGE,"E264.right")])],"isStart":false});
            var sketch = newSketch(context, id + "F106", { "sketchPlane" : qUnion([Q0])});
            skLineSegment(sketch, "E266.0.0", {"start": v(-7327.9, 0) * mm, "end": v(-10045.7, 0) * mm});
            skLineSegment(sketch, "E266.0.1", {"start": v(-10045.7, 0) * mm, "end": v(-10045.7, 2425.7) * mm});
            skLineSegment(sketch, "E266.0.2", {"start": v(-10045.7, 2425.7) * mm, "end": v(-7327.9, 2425.7) * mm});
            skLineSegment(sketch, "E266.0.3", {"start": v(-7327.9, 2425.7) * mm, "end": v(-7327.9, 0) * mm});
            skSolve(sketch);
        }
        {
            var Q0;
            Q0=qSketchRegion(id+"F106",true);
            extrude(context, id + "F107", {"entities" : qUnion([Q0]), "operationType" : NewBodyOperationType.REMOVE, "oppositeDirection" : true, "depth" : 6.35 * mm});
        }
        {
            var Q0;
            Q0=makeQuery(id+"F105.boolean.opBoolean","COPY",FACE,{"derivedFrom":makeQuery(id+"F105.opExtrude","CAP_FACE",FACE,{"disambiguationData":[OSD([sQuery(id+"F104.wireOp",EDGE,"E265.bottom"),sQuery(id+"F104.wireOp",EDGE,"E265.top"),sQuery(id+"F104.wireOp",EDGE,"E265.left"),sQuery(id+"F104.wireOp",EDGE,"E265.right")])],"isStart":false})});
            var sketch = newSketch(context, id + "F108", { "sketchPlane" : qUnion([Q0])});
            skLineSegment(sketch, "E267.bottom", {"start": v(7327.9, 606.43) * mm, "end": v(10045.7, 606.43) * mm});
            skLineSegment(sketch, "E267.top", {"start": v(7327.9, 606.4) * mm, "end": v(10045.7, 606.4) * mm});
            skLineSegment(sketch, "E267.left", {"start": v(7327.9, 606.43) * mm, "end": v(7327.9, 606.4) * mm});
            skLineSegment(sketch, "E267.right", {"start": v(10045.7, 606.43) * mm, "end": v(10045.7, 606.4) * mm});
            skLineSegment(sketch, "E268.bottom", {"start": v(7327.9, 1212.84) * mm, "end": v(10045.7, 1212.84) * mm});
            skLineSegment(sketch, "E268.top", {"start": v(7327.9, 1212.86) * mm, "end": v(10045.7, 1212.86) * mm});
            skLineSegment(sketch, "E268.left", {"start": v(7327.9, 1212.84) * mm, "end": v(7327.9, 1212.86) * mm});
            skLineSegment(sketch, "E268.right", {"start": v(10045.7, 1212.84) * mm, "end": v(10045.7, 1212.86) * mm});
            skLineSegment(sketch, "E269.bottom", {"start": v(7327.9, 1819.27) * mm, "end": v(10045.7, 1819.27) * mm});
            skLineSegment(sketch, "E269.top", {"start": v(7327.9, 1819.3) * mm, "end": v(10045.7, 1819.3) * mm});
            skLineSegment(sketch, "E269.left", {"start": v(7327.9, 1819.27) * mm, "end": v(7327.9, 1819.3) * mm});
            skLineSegment(sketch, "E269.right", {"start": v(10045.7, 1819.27) * mm, "end": v(10045.7, 1819.3) * mm});
            skLineSegment(sketch, "E270", {"start": v(8686.8, 1819.3) * mm, "end": v(8686.8, 2425.7) * mm, "construction": true});
            skLineSegment(sketch, "E271", {"start": v(8686.8, 1819.27) * mm, "end": v(8686.8, 1212.86) * mm, "construction": true});
            skLineSegment(sketch, "E272", {"start": v(8686.8, 1212.84) * mm, "end": v(8686.8, 606.43) * mm, "construction": true});
            skLineSegment(sketch, "E273", {"start": v(8686.8, 606.4) * mm, "end": v(8686.8, 0) * mm, "construction": true});
            skSolve(sketch);
        }
        {
            var Q0;
            Q0=qSketchRegion(id+"F108",true);
            extrude(context, id + "F109", {"entities" : qUnion([Q0]), "operationType" : NewBodyOperationType.REMOVE, "oppositeDirection" : true, "depth" : 50.8 * mm});
        }
        {
            var Q0;
            Q0=qCreatedBy(id+"F8.planeOp",FACE);
            var sketch = newSketch(context, id + "F110", { "sketchPlane" : qUnion([Q0])});
            skLineSegment(sketch, "E274", {"start": v(7315.2, 0) * mm, "end": v(7315.2, 2146.3) * mm});
            skLineSegment(sketch, "E275", {"start": v(7315.2, 2146.3) * mm, "end": v(10972.8, 2146.3) * mm});
            skLineSegment(sketch, "E276", {"start": v(10972.8, 2146.3) * mm, "end": v(10972.8, 0) * mm});
            skLineSegment(sketch, "E277", {"start": v(10972.8, 0) * mm, "end": v(7315.2, 0) * mm});
            skSolve(sketch);
        }
        {
            var Q0;
            Q0=qSketchRegion(id+"F110",true);
            extrude(context, id + "F111", {"entities" : qUnion([Q0]), "oppositeDirection" : true, "depth" : 88.9 * mm, "offsetDistance" : 25.4 * mm});
        }
        {
            var Q0;
            Q0=makeQuery(id+"F111.opExtrude","CAP_FACE",FACE,{"disambiguationData":[OSD([sQuery(id+"F110.wireOp",EDGE,"E274"),sQuery(id+"F110.wireOp",EDGE,"E275"),sQuery(id+"F110.wireOp",EDGE,"E276"),sQuery(id+"F110.wireOp",EDGE,"E277")])],"isStart":true});
            var sketch = newSketch(context, id + "F112", { "sketchPlane" : qUnion([Q0])});
            skLineSegment(sketch, "E278", {"start": v(9144, 0) * mm, "end": v(9144, 2146.3) * mm, "construction": true});
            skLineSegment(sketch, "E279.bottom", {"start": v(8255, 0) * mm, "end": v(10033, 0) * mm});
            skLineSegment(sketch, "E279.top", {"start": v(8255, 2032) * mm, "end": v(10033, 2032) * mm});
            skLineSegment(sketch, "E279.left", {"start": v(8255, 0) * mm, "end": v(8255, 2032) * mm});
            skLineSegment(sketch, "E279.right", {"start": v(10033, 0) * mm, "end": v(10033, 2032) * mm});
            skSolve(sketch);
        }
        {
            var Q0;
            Q0=qSketchRegion(id+"F112",true);
            extrude(context, id + "F113", {"entities" : qUnion([Q0]), "operationType" : NewBodyOperationType.REMOVE, "oppositeDirection" : true, "depth" : 26.99 * mm, "offsetDistance" : 25.4 * mm});
        }
        {
            var Q0;
            Q0=makeQuery(id+"F111.opExtrude","CAP_FACE",FACE,{"disambiguationData":[OSD([sQuery(id+"F110.wireOp",EDGE,"E274"),sQuery(id+"F110.wireOp",EDGE,"E275"),sQuery(id+"F110.wireOp",EDGE,"E276"),sQuery(id+"F110.wireOp",EDGE,"E277")])],"isStart":false});
            var sketch = newSketch(context, id + "F114", { "sketchPlane" : qUnion([Q0])});
            skLineSegment(sketch, "E280.0.0", {"start": v(-8255, 0) * mm, "end": v(-10033, 0) * mm});
            skLineSegment(sketch, "E280.0.1", {"start": v(-10033, 0) * mm, "end": v(-10033, 2032) * mm});
            skLineSegment(sketch, "E280.0.2", {"start": v(-10033, 2032) * mm, "end": v(-8255, 2032) * mm});
            skLineSegment(sketch, "E280.0.3", {"start": v(-8255, 2032) * mm, "end": v(-8255, 0) * mm});
            skSolve(sketch);
        }
        {
            var Q0;
            Q0=qSketchRegion(id+"F114",true);
            extrude(context, id + "F115", {"entities" : qUnion([Q0]), "operationType" : NewBodyOperationType.REMOVE, "oppositeDirection" : true, "depth" : 26.99 * mm, "offsetDistance" : 25.4 * mm});
        }
        {
            var Q0;
            Q0=makeQuery(id+"F113.boolean.opBoolean","COPY",FACE,{"derivedFrom":makeQuery(id+"F113.opExtrude","CAP_FACE",FACE,{"disambiguationData":[OSD([sQuery(id+"F112.wireOp",EDGE,"E279.bottom"),sQuery(id+"F112.wireOp",EDGE,"E279.top"),sQuery(id+"F112.wireOp",EDGE,"E279.left"),sQuery(id+"F112.wireOp",EDGE,"E279.right")])],"isStart":false})});
            var sketch = newSketch(context, id + "F116", { "sketchPlane" : qUnion([Q0])});
            skLineSegment(sketch, "E281", {"start": v(9144, 0) * mm, "end": v(9144, 2032) * mm, "construction": true});
            skLineSegment(sketch, "E282.bottom", {"start": v(9143.99, 2032) * mm, "end": v(9144.01, 2032) * mm});
            skLineSegment(sketch, "E282.top", {"start": v(9143.99, 0) * mm, "end": v(9144.01, 0) * mm});
            skLineSegment(sketch, "E282.left", {"start": v(9143.99, 2032) * mm, "end": v(9143.99, 0) * mm});
            skLineSegment(sketch, "E282.right", {"start": v(9144.01, 2032) * mm, "end": v(9144.01, 0) * mm});
            skSolve(sketch);
        }
        {
            var Q0;
            Q0=qSketchRegion(id+"F116",true);
            extrude(context, id + "F117", {"entities" : qUnion([Q0]), "operationType" : NewBodyOperationType.REMOVE, "oppositeDirection" : true, "depth" : 50.8 * mm});
        }
        {
            var Q0;
            {var subQ1=sQuery(id+"F110.wireOp",EDGE,"E277");var subQ4=sQuery(id+"F110.wireOp",EDGE,"E274");Q0=makeQuery(id+"F117.boolean.opBoolean","SPLIT",FACE,{"disambiguationData":[TD([makeQuery(id+"F111.opExtrude","SWEPT_FACE",FACE,{"disambiguationData":[OSD([subQ4])]})])],"derivedFrom":makeQuery(id+"F111.opExtrude","SWEPT_FACE",FACE,{"disambiguationData":[OSD([subQ1])]})});}
            var sketch = newSketch(context, id + "F118", { "sketchPlane" : qUnion([Q0])});
            skLineSegment(sketch, "E283", {"start": v(7315.2, -1828.8) * mm, "end": v(7315.2, -1739.9) * mm});
            skLineSegment(sketch, "E284", {"start": v(7315.2, -1739.9) * mm, "end": v(8255, -1739.9) * mm});
            skLineSegment(sketch, "E285", {"start": v(8255, -1739.9) * mm, "end": v(8255, -1758.95) * mm});
            skLineSegment(sketch, "E286", {"start": v(8255, -1758.95) * mm, "end": v(7340.6, -1758.95) * mm});
            skLineSegment(sketch, "E287", {"start": v(7340.6, -1758.95) * mm, "end": v(7340.6, -1784.34) * mm});
            skLineSegment(sketch, "E288", {"start": v(7340.6, -1784.34) * mm, "end": v(7467.6, -1784.34) * mm});
            skLineSegment(sketch, "E289", {"start": v(7467.6, -1784.34) * mm, "end": v(7467.6, -1766.89) * mm});
            skLineSegment(sketch, "E290", {"start": v(7467.6, -1766.89) * mm, "end": v(8382, -1766.89) * mm});
            skLineSegment(sketch, "E291", {"start": v(8382, -1766.89) * mm, "end": v(8382, -1784.34) * mm});
            skLineSegment(sketch, "E292", {"start": v(8382, -1784.34) * mm, "end": v(9906, -1784.34) * mm});
            skLineSegment(sketch, "E293", {"start": v(9906, -1784.34) * mm, "end": v(9906, -1766.89) * mm});
            skLineSegment(sketch, "E294", {"start": v(9906, -1766.89) * mm, "end": v(10820.4, -1766.89) * mm});
            skLineSegment(sketch, "E295", {"start": v(10820.4, -1766.89) * mm, "end": v(10820.4, -1784.34) * mm});
            skLineSegment(sketch, "E296", {"start": v(10820.4, -1784.34) * mm, "end": v(10947.4, -1784.34) * mm});
            skLineSegment(sketch, "E297", {"start": v(10947.4, -1784.34) * mm, "end": v(10947.4, -1758.95) * mm});
            skLineSegment(sketch, "E298", {"start": v(10947.4, -1758.95) * mm, "end": v(10033, -1758.95) * mm});
            skLineSegment(sketch, "E299", {"start": v(10033, -1758.95) * mm, "end": v(10033, -1739.9) * mm});
            skLineSegment(sketch, "E300", {"start": v(10033, -1739.9) * mm, "end": v(10972.8, -1739.9) * mm});
            skLineSegment(sketch, "E301", {"start": v(10972.8, -1739.9) * mm, "end": v(10972.8, -1828.8) * mm});
            skLineSegment(sketch, "E302", {"start": v(10972.8, -1828.8) * mm, "end": v(10033, -1828.8) * mm});
            skLineSegment(sketch, "E303", {"start": v(10033, -1828.8) * mm, "end": v(10033, -1809.75) * mm});
            skLineSegment(sketch, "E304", {"start": v(10033, -1809.75) * mm, "end": v(10947.4, -1809.75) * mm});
            skLineSegment(sketch, "E305", {"start": v(10947.4, -1809.75) * mm, "end": v(10947.4, -1784.36) * mm});
            skLineSegment(sketch, "E306", {"start": v(10947.4, -1784.36) * mm, "end": v(10820.4, -1784.36) * mm});
            skLineSegment(sketch, "E307", {"start": v(10820.4, -1784.36) * mm, "end": v(10820.4, -1801.81) * mm});
            skLineSegment(sketch, "E308", {"start": v(10820.4, -1801.81) * mm, "end": v(9906, -1801.81) * mm});
            skLineSegment(sketch, "E309", {"start": v(9906, -1801.81) * mm, "end": v(9906, -1784.36) * mm});
            skLineSegment(sketch, "E310", {"start": v(9906, -1784.36) * mm, "end": v(8382, -1784.36) * mm});
            skLineSegment(sketch, "E311", {"start": v(8382, -1784.36) * mm, "end": v(8382, -1801.81) * mm});
            skLineSegment(sketch, "E312", {"start": v(8382, -1801.81) * mm, "end": v(7467.6, -1801.81) * mm});
            skLineSegment(sketch, "E313", {"start": v(7467.6, -1801.81) * mm, "end": v(7467.6, -1784.36) * mm});
            skLineSegment(sketch, "E314", {"start": v(7467.6, -1784.36) * mm, "end": v(7340.6, -1784.36) * mm});
            skLineSegment(sketch, "E315", {"start": v(7340.6, -1784.36) * mm, "end": v(7340.6, -1809.75) * mm});
            skLineSegment(sketch, "E316", {"start": v(7340.6, -1809.75) * mm, "end": v(8255, -1809.75) * mm});
            skLineSegment(sketch, "E317", {"start": v(8255, -1809.75) * mm, "end": v(8255, -1828.8) * mm});
            skLineSegment(sketch, "E318", {"start": v(8255, -1828.8) * mm, "end": v(7315.2, -1828.8) * mm});
            skSolve(sketch);
        }
        {
            var Q0;
            Q0=qSketchRegion(id+"F118",true);
            extrude(context, id + "F119", {"entities" : qUnion([Q0]), "oppositeDirection" : true, "depth" : 25.4 * mm});
        }
        {
            var Q0;
            Q0=qCreatedBy(id+"F73.planeOp",FACE);
            var sketch = newSketch(context, id + "F120", { "sketchPlane" : qUnion([Q0])});
            skLineSegment(sketch, "E319.bottom", {"start": v(1219.2, 0) * mm, "end": v(0, 0) * mm});
            skLineSegment(sketch, "E319.top", {"start": v(1219.2, 914.4) * mm, "end": v(0, 914.4) * mm});
            skLineSegment(sketch, "E319.left", {"start": v(1219.2, 0) * mm, "end": v(1219.2, 914.4) * mm});
            skLineSegment(sketch, "E319.right", {"start": v(0, 0) * mm, "end": v(0, 914.4) * mm});
            skSolve(sketch);
        }
        {
            var Q0;
            Q0 = qSketchRegion(id + "F120", true);
            extrude(context, id + "F121", {"entities" : qUnion([Q0]), "oppositeDirection" : true, "depth" : 165.1 * mm, "offsetDistance" : 25.4 * mm});
        }
        {
            var Q0;
            Q0=makeQuery(id+"F121.opExtrude","CAP_FACE",FACE,{"disambiguationData":[OSD([sQuery(id+"F120.wireOp",EDGE,"E319.bottom"),sQuery(id+"F120.wireOp",EDGE,"E319.top"),sQuery(id+"F120.wireOp",EDGE,"E319.left"),sQuery(id+"F120.wireOp",EDGE,"E319.right")])],"isStart":false});
            var sketch = newSketch(context, id + "F122", { "sketchPlane" : qUnion([Q0])});
            skLineSegment(sketch, "E320.bottom", {"start": v(-1200.15, 895.35) * mm, "end": v(-19.05, 895.35) * mm});
            skLineSegment(sketch, "E320.top", {"start": v(-1200.15, 19.05) * mm, "end": v(-19.05, 19.05) * mm});
            skLineSegment(sketch, "E320.left", {"start": v(-1200.15, 895.35) * mm, "end": v(-1200.15, 19.05) * mm});
            skLineSegment(sketch, "E320.right", {"start": v(-19.05, 895.35) * mm, "end": v(-19.05, 19.05) * mm});
            skSolve(sketch);
        }
        {
            var Q0;
            Q0 = qSketchRegion(id + "F122", true);
            extrude(context, id + "F123", {"entities" : qUnion([Q0]), "operationType" : NewBodyOperationType.REMOVE, "oppositeDirection" : true, "depth" : 114.3 * mm, "offsetDistance" : 25.4 * mm});
        }
        {
            var Q0;
            Q0=makeQuery(id+"F121.opExtrude","CAP_FACE",FACE,{"disambiguationData":[OSD([sQuery(id+"F120.wireOp",EDGE,"E319.bottom"),sQuery(id+"F120.wireOp",EDGE,"E319.top"),sQuery(id+"F120.wireOp",EDGE,"E319.left"),sQuery(id+"F120.wireOp",EDGE,"E319.right")])],"isStart":true});
            var sketch = newSketch(context, id + "F124", { "sketchPlane" : qUnion([Q0])});
            skLineSegment(sketch, "E321.bottom", {"start": v(50.8, 50.8) * mm, "end": v(584.2, 50.8) * mm});
            skLineSegment(sketch, "E321.top", {"start": v(50.8, 863.6) * mm, "end": v(584.2, 863.6) * mm});
            skLineSegment(sketch, "E321.left", {"start": v(50.8, 50.8) * mm, "end": v(50.8, 863.6) * mm});
            skLineSegment(sketch, "E321.right", {"start": v(584.2, 50.8) * mm, "end": v(584.2, 863.6) * mm});
            skLineSegment(sketch, "E322.bottom", {"start": v(635, 50.8) * mm, "end": v(1168.4, 50.8) * mm});
            skLineSegment(sketch, "E322.top", {"start": v(635, 863.6) * mm, "end": v(1168.4, 863.6) * mm});
            skLineSegment(sketch, "E322.left", {"start": v(635, 50.8) * mm, "end": v(635, 863.6) * mm});
            skLineSegment(sketch, "E322.right", {"start": v(1168.4, 50.8) * mm, "end": v(1168.4, 863.6) * mm});
            skSolve(sketch);
        }
        {
            var Q0;
            Q0 = qSketchRegion(id + "F124", true);
            extrude(context, id + "F125", {"entities" : qUnion([Q0]), "operationType" : NewBodyOperationType.REMOVE, "oppositeDirection" : true, "depth" : 12.7 * mm, "offsetDistance" : 25.4 * mm});
        }
        {
            var Q0;
            Q0=makeQuery(id+"F123.boolean.opBoolean","COPY",FACE,{"derivedFrom":makeQuery(id+"F123.opExtrude","CAP_FACE",FACE,{"disambiguationData":[OSD([sQuery(id+"F122.wireOp",EDGE,"E320.bottom"),sQuery(id+"F122.wireOp",EDGE,"E320.top"),sQuery(id+"F122.wireOp",EDGE,"E320.left"),sQuery(id+"F122.wireOp",EDGE,"E320.right")])],"isStart":false})});
            var sketch = newSketch(context, id + "F126", { "sketchPlane" : qUnion([Q0])});
            skLineSegment(sketch, "E323.0", {"start": v(-635, 50.8) * mm, "end": v(-1168.4, 50.8) * mm});
            skLineSegment(sketch, "E324.0", {"start": v(-1168.4, 50.8) * mm, "end": v(-1168.4, 863.6) * mm});
            skLineSegment(sketch, "E325.0", {"start": v(-635, 863.6) * mm, "end": v(-1168.4, 863.6) * mm});
            skLineSegment(sketch, "E326.0", {"start": v(-50.8, 50.8) * mm, "end": v(-584.2, 50.8) * mm});
            skLineSegment(sketch, "E327.0", {"start": v(-584.2, 50.8) * mm, "end": v(-584.2, 863.6) * mm});
            skLineSegment(sketch, "E328.0", {"start": v(-635, 50.8) * mm, "end": v(-635, 863.6) * mm});
            skLineSegment(sketch, "E329.0", {"start": v(-50.8, 863.6) * mm, "end": v(-584.2, 863.6) * mm});
            skLineSegment(sketch, "E330.0", {"start": v(-50.8, 50.8) * mm, "end": v(-50.8, 863.6) * mm});
            skSolve(sketch);
        }
        {
            var Q0;
            Q0 = qSketchRegion(id + "F126", true);
            extrude(context, id + "F127", {"entities" : qUnion([Q0]), "operationType" : NewBodyOperationType.REMOVE, "oppositeDirection" : true, "depth" : 12.7 * mm, "offsetDistance" : 25.4 * mm});
        }
        {
            var Q0;
            Q0=qCreatedBy(id+"F74.planeOp",FACE);
            var sketch = newSketch(context, id + "F128", { "sketchPlane" : qUnion([Q0])});
            skLineSegment(sketch, "E331", {"start": v(1219.2, 0) * mm, "end": v(-609.6, 0) * mm});
            skLineSegment(sketch, "E332", {"start": v(-4876.8, 0) * mm, "end": v(-4876.8, 609.6) * mm});
            skLineSegment(sketch, "E333", {"start": v(1219.2, 0) * mm, "end": v(1219.2, 609.6) * mm});
            skLineSegment(sketch, "E334", {"start": v(-609.6, 0) * mm, "end": v(-609.6, 1393.65) * mm});
            skLineSegment(sketch, "E335", {"start": v(-762, 0) * mm, "end": v(-762, 1426) * mm});
            skLineSegment(sketch, "E336", {"start": v(-2895.6, 0) * mm, "end": v(-2895.6, 1426) * mm});
            skLineSegment(sketch, "E337", {"start": v(-3048, 0) * mm, "end": v(-3048, 1393.65) * mm});
            skArc(sketch, "E338", {"start": v(1219.2, 609.6) * mm, "mid": v(340.52, 1084.93) * mm, "end": v(-609.6, 1393.65) * mm});
            skArc(sketch, "E339.trimOffspring", {"start": v(-3048, 1393.65) * mm, "mid": v(-3998.12, 1084.93) * mm, "end": v(-4876.8, 609.6) * mm});
            skLineSegment(sketch, "E340.trimOffspring", {"start": v(-3048, 0) * mm, "end": v(-4876.8, 0) * mm});
            skArc(sketch, "E341.trimOffspring", {"start": v(-762, 1426) * mm, "mid": v(-1828.8, 1530.35) * mm, "end": v(-2895.6, 1426) * mm});
            skLineSegment(sketch, "E342.trimOffspring", {"start": v(-762, 0) * mm, "end": v(-2895.6, 0) * mm});
            skSolve(sketch);
        }
        {
            var Q0;
            Q0 = qSketchRegion(id + "F128", true);
            extrude(context, id + "F129", {"entities" : qUnion([Q0]), "oppositeDirection" : true, "depth" : 165.1 * mm, "offsetDistance" : 25.4 * mm});
        }
        {
            var Q0;
            Q0=makeQuery(id+"F129.opExtrude","CAP_FACE",FACE,{"disambiguationData":[OSD([sQuery(id+"F128.wireOp",EDGE,"E331"),sQuery(id+"F128.wireOp",EDGE,"E333"),sQuery(id+"F128.wireOp",EDGE,"E334"),sQuery(id+"F128.wireOp",EDGE,"E338")])],"isStart":true});
            var sketch = newSketch(context, id + "F130", { "sketchPlane" : qUnion([Q0])});
            skLineSegment(sketch, "E343.0", {"start": v(-609.6, 0) * mm, "end": v(-609.6, 1393.65) * mm, "construction": true});
            skArc(sketch, "E344.0", {"start": v(1219.2, 609.6) * mm, "mid": v(340.52, 1084.93) * mm, "end": v(-609.6, 1393.65) * mm, "construction": true});
            skLineSegment(sketch, "E345.0", {"start": v(1219.2, 0) * mm, "end": v(1219.2, 609.6) * mm, "construction": true});
            skLineSegment(sketch, "E346.0", {"start": v(1219.2, 0) * mm, "end": v(-609.6, 0) * mm, "construction": true});
            skLineSegment(sketch, "E347.0", {"start": v(-558.8, 50.8) * mm, "end": v(-558.8, 1329.64) * mm});
            skLineSegment(sketch, "E347.1", {"start": v(1168.4, 50.8) * mm, "end": v(-558.8, 50.8) * mm});
            skLineSegment(sketch, "E347.2", {"start": v(1168.4, 50.8) * mm, "end": v(1168.4, 582.29) * mm});
            skArc(sketch, "E347.3", {"start": v(1168.4, 582.29) * mm, "mid": v(337.28, 1031.02) * mm, "end": v(-558.8, 1329.64) * mm});
            skSolve(sketch);
        }
        {
            var Q0;
            Q0=makeQuery(id+"F130.imprint","IMPRINT",FACE,{"disambiguationData":[TD([[makeQuery(id+"F130.imprint","IMPRINT",EDGE,{"derivedFrom":sQuery(id+"F130.wireOp",EDGE,"E347.0")}),-1.0]])]});
            extrude(context, id + "F131", {"entities" : qUnion([Q0]), "operationType" : NewBodyOperationType.REMOVE, "oppositeDirection" : true, "depth" : 12.7 * mm, "offsetDistance" : 25.4 * mm});
        }
        {
            var Q0;
            Q0=makeQuery(id+"F129.opExtrude","CAP_FACE",FACE,{"disambiguationData":[OSD([sQuery(id+"F128.wireOp",EDGE,"E335"),sQuery(id+"F128.wireOp",EDGE,"E336"),sQuery(id+"F128.wireOp",EDGE,"E341.trimOffspring"),sQuery(id+"F128.wireOp",EDGE,"E342.trimOffspring")])],"isStart":true});
            var sketch = newSketch(context, id + "F132", { "sketchPlane" : qUnion([Q0])});
            skArc(sketch, "E348.0", {"start": v(-762, 1426) * mm, "mid": v(-1828.8, 1530.35) * mm, "end": v(-2895.6, 1426) * mm, "construction": true});
            skLineSegment(sketch, "E349.0", {"start": v(-2895.6, 0) * mm, "end": v(-2895.6, 1426) * mm, "construction": true});
            skLineSegment(sketch, "E350.0", {"start": v(-762, 0) * mm, "end": v(-2895.6, 0) * mm, "construction": true});
            skLineSegment(sketch, "E351.0", {"start": v(-762, 0) * mm, "end": v(-762, 1426) * mm, "construction": true});
            skArc(sketch, "E352.0", {"start": v(-812.8, 1384.1) * mm, "mid": v(-1828.8, 1479.55) * mm, "end": v(-2844.8, 1384.1) * mm});
            skLineSegment(sketch, "E352.1", {"start": v(-812.8, 50.8) * mm, "end": v(-812.8, 1384.1) * mm});
            skLineSegment(sketch, "E352.2", {"start": v(-812.8, 50.8) * mm, "end": v(-2844.8, 50.8) * mm});
            skLineSegment(sketch, "E352.3", {"start": v(-2844.8, 50.8) * mm, "end": v(-2844.8, 1384.1) * mm});
            skSolve(sketch);
        }
        {
            var Q0;
            Q0=makeQuery(id+"F132.imprint","IMPRINT",FACE,{"disambiguationData":[TD([[makeQuery(id+"F132.imprint","IMPRINT",EDGE,{"derivedFrom":sQuery(id+"F132.wireOp",EDGE,"E352.0")}),1.0]])]});
            extrude(context, id + "F133", {"entities" : qUnion([Q0]), "operationType" : NewBodyOperationType.REMOVE, "oppositeDirection" : true, "depth" : 12.7 * mm, "offsetDistance" : 25.4 * mm});
        }
        {
            var Q0;
            Q0=makeQuery(id+"F129.opExtrude","CAP_FACE",FACE,{"disambiguationData":[OSD([sQuery(id+"F128.wireOp",EDGE,"E332"),sQuery(id+"F128.wireOp",EDGE,"E337"),sQuery(id+"F128.wireOp",EDGE,"E339.trimOffspring"),sQuery(id+"F128.wireOp",EDGE,"E340.trimOffspring")])],"isStart":true});
            var sketch = newSketch(context, id + "F134", { "sketchPlane" : qUnion([Q0])});
            skArc(sketch, "E353.0", {"start": v(-3098.8, 1329.64) * mm, "mid": v(-3994.88, 1031.02) * mm, "end": v(-4826, 582.29) * mm});
            skLineSegment(sketch, "E353.1", {"start": v(-3098.8, 50.8) * mm, "end": v(-3098.8, 1329.64) * mm});
            skLineSegment(sketch, "E353.2", {"start": v(-3098.8, 50.8) * mm, "end": v(-4826, 50.8) * mm});
            skLineSegment(sketch, "E353.3", {"start": v(-4826, 50.8) * mm, "end": v(-4826, 582.29) * mm});
            skSolve(sketch);
        }
        {
            var Q0;
            Q0 = qSketchRegion(id + "F134", true);
            extrude(context, id + "F135", {"entities" : qUnion([Q0]), "operationType" : NewBodyOperationType.REMOVE, "oppositeDirection" : true, "depth" : 12.7 * mm, "offsetDistance" : 25.4 * mm});
        }
        {
            var Q0;
            Q0=makeQuery(id+"F129.opExtrude","CAP_FACE",FACE,{"disambiguationData":[OSD([sQuery(id+"F128.wireOp",EDGE,"E331"),sQuery(id+"F128.wireOp",EDGE,"E333"),sQuery(id+"F128.wireOp",EDGE,"E334"),sQuery(id+"F128.wireOp",EDGE,"E338")])],"isStart":false});
            var sketch = newSketch(context, id + "F136", { "sketchPlane" : qUnion([Q0])});
            skArc(sketch, "E354.0", {"start": v(-1200.15, 599.38) * mm, "mid": v(-339.29, 1064.73) * mm, "end": v(590.55, 1369.74) * mm});
            skLineSegment(sketch, "E354.1", {"start": v(-1200.15, 19.05) * mm, "end": v(-1200.15, 599.38) * mm});
            skLineSegment(sketch, "E354.2", {"start": v(-1200.15, 19.05) * mm, "end": v(590.55, 19.05) * mm});
            skLineSegment(sketch, "E354.3", {"start": v(590.55, 19.05) * mm, "end": v(590.55, 1369.74) * mm});
            skSolve(sketch);
        }
        {
            var Q0;
            Q0 = qSketchRegion(id + "F136", true);
            extrude(context, id + "F137", {"entities" : qUnion([Q0]), "operationType" : NewBodyOperationType.REMOVE, "oppositeDirection" : true, "depth" : 114.3 * mm, "offsetDistance" : 25.4 * mm});
        }
        {
            var Q0;
            Q0=makeQuery(id+"F137.boolean.opBoolean","COPY",FACE,{"derivedFrom":makeQuery(id+"F137.opExtrude","CAP_FACE",FACE,{"disambiguationData":[OSD([sQuery(id+"F136.wireOp",EDGE,"E354.0"),sQuery(id+"F136.wireOp",EDGE,"E354.1"),sQuery(id+"F136.wireOp",EDGE,"E354.2"),sQuery(id+"F136.wireOp",EDGE,"E354.3")])],"isStart":false})});
            var sketch = newSketch(context, id + "F138", { "sketchPlane" : qUnion([Q0])});
            skArc(sketch, "E355.0", {"start": v(-1168.4, 582.29) * mm, "mid": v(-337.28, 1031.02) * mm, "end": v(558.8, 1329.64) * mm});
            skLineSegment(sketch, "E355.1", {"start": v(-1168.4, 50.8) * mm, "end": v(-1168.4, 582.29) * mm});
            skLineSegment(sketch, "E355.2", {"start": v(-1168.4, 50.8) * mm, "end": v(558.8, 50.8) * mm});
            skLineSegment(sketch, "E355.3", {"start": v(558.8, 50.8) * mm, "end": v(558.8, 1329.64) * mm});
            skSolve(sketch);
        }
        {
            var Q0;
            Q0 = qSketchRegion(id + "F138", true);
            extrude(context, id + "F139", {"entities" : qUnion([Q0]), "operationType" : NewBodyOperationType.REMOVE, "oppositeDirection" : true, "depth" : 12.7 * mm, "offsetDistance" : 25.4 * mm});
        }
        {
            var Q0;
            Q0=makeQuery(id+"F129.opExtrude","CAP_FACE",FACE,{"disambiguationData":[OSD([sQuery(id+"F128.wireOp",EDGE,"E335"),sQuery(id+"F128.wireOp",EDGE,"E336"),sQuery(id+"F128.wireOp",EDGE,"E341.trimOffspring"),sQuery(id+"F128.wireOp",EDGE,"E342.trimOffspring")])],"isStart":false});
            var sketch = newSketch(context, id + "F140", { "sketchPlane" : qUnion([Q0])});
            skArc(sketch, "E356.0", {"start": v(781.05, 1410.32) * mm, "mid": v(1828.8, 1511.3) * mm, "end": v(2876.55, 1410.32) * mm});
            skLineSegment(sketch, "E356.1", {"start": v(781.05, 19.05) * mm, "end": v(781.05, 1410.32) * mm});
            skLineSegment(sketch, "E356.2", {"start": v(781.05, 19.05) * mm, "end": v(2876.55, 19.05) * mm});
            skLineSegment(sketch, "E356.3", {"start": v(2876.55, 19.05) * mm, "end": v(2876.55, 1410.32) * mm});
            skSolve(sketch);
        }
        {
            var Q0;
            Q0 = qSketchRegion(id + "F140", true);
            extrude(context, id + "F141", {"entities" : qUnion([Q0]), "operationType" : NewBodyOperationType.REMOVE, "oppositeDirection" : true, "depth" : 114.3 * mm, "offsetDistance" : 25.4 * mm});
        }
        {
            var Q0;
            Q0=makeQuery(id+"F141.boolean.opBoolean","COPY",FACE,{"derivedFrom":makeQuery(id+"F141.opExtrude","CAP_FACE",FACE,{"disambiguationData":[OSD([sQuery(id+"F140.wireOp",EDGE,"E356.0"),sQuery(id+"F140.wireOp",EDGE,"E356.1"),sQuery(id+"F140.wireOp",EDGE,"E356.2"),sQuery(id+"F140.wireOp",EDGE,"E356.3")])],"isStart":false})});
            var sketch = newSketch(context, id + "F142", { "sketchPlane" : qUnion([Q0])});
            skArc(sketch, "E357.0", {"start": v(812.8, 1384.1) * mm, "mid": v(1828.8, 1479.55) * mm, "end": v(2844.8, 1384.1) * mm});
            skLineSegment(sketch, "E357.1", {"start": v(812.8, 50.8) * mm, "end": v(812.8, 1384.1) * mm});
            skLineSegment(sketch, "E357.2", {"start": v(812.8, 50.8) * mm, "end": v(2844.8, 50.8) * mm});
            skLineSegment(sketch, "E357.3", {"start": v(2844.8, 50.8) * mm, "end": v(2844.8, 1384.1) * mm});
            skSolve(sketch);
        }
        {
            var Q0;
            Q0 = qSketchRegion(id + "F142", true);
            extrude(context, id + "F143", {"entities" : qUnion([Q0]), "operationType" : NewBodyOperationType.REMOVE, "oppositeDirection" : true, "depth" : 12.7 * mm, "offsetDistance" : 25.4 * mm});
        }
        {
            var Q0;
            Q0=makeQuery(id+"F129.opExtrude","CAP_FACE",FACE,{"disambiguationData":[OSD([sQuery(id+"F128.wireOp",EDGE,"E332"),sQuery(id+"F128.wireOp",EDGE,"E337"),sQuery(id+"F128.wireOp",EDGE,"E339.trimOffspring"),sQuery(id+"F128.wireOp",EDGE,"E340.trimOffspring")])],"isStart":false});
            var sketch = newSketch(context, id + "F144", { "sketchPlane" : qUnion([Q0])});
            skArc(sketch, "E358.0", {"start": v(3067.05, 1369.74) * mm, "mid": v(3996.89, 1064.73) * mm, "end": v(4857.75, 599.38) * mm});
            skLineSegment(sketch, "E358.1", {"start": v(3067.05, 19.05) * mm, "end": v(3067.05, 1369.74) * mm});
            skLineSegment(sketch, "E358.2", {"start": v(3067.05, 19.05) * mm, "end": v(4857.75, 19.05) * mm});
            skLineSegment(sketch, "E358.3", {"start": v(4857.75, 19.05) * mm, "end": v(4857.75, 599.38) * mm});
            skSolve(sketch);
        }
        {
            var Q0;
            Q0 = qSketchRegion(id + "F144", true);
            extrude(context, id + "F145", {"entities" : qUnion([Q0]), "operationType" : NewBodyOperationType.REMOVE, "oppositeDirection" : true, "depth" : 114.3 * mm, "offsetDistance" : 25.4 * mm});
        }
        {
            var Q0;
            Q0=makeQuery(id+"F145.boolean.opBoolean","COPY",FACE,{"derivedFrom":makeQuery(id+"F145.opExtrude","CAP_FACE",FACE,{"disambiguationData":[OSD([sQuery(id+"F144.wireOp",EDGE,"E358.0"),sQuery(id+"F144.wireOp",EDGE,"E358.1"),sQuery(id+"F144.wireOp",EDGE,"E358.2"),sQuery(id+"F144.wireOp",EDGE,"E358.3")])],"isStart":false})});
            var sketch = newSketch(context, id + "F146", { "sketchPlane" : qUnion([Q0])});
            skArc(sketch, "E359.0", {"start": v(3098.8, 1329.64) * mm, "mid": v(3994.88, 1031.02) * mm, "end": v(4826, 582.29) * mm});
            skLineSegment(sketch, "E359.1", {"start": v(3098.8, 50.8) * mm, "end": v(3098.8, 1329.64) * mm});
            skLineSegment(sketch, "E359.2", {"start": v(3098.8, 50.8) * mm, "end": v(4826, 50.8) * mm});
            skLineSegment(sketch, "E359.3", {"start": v(4826, 50.8) * mm, "end": v(4826, 582.29) * mm});
            skSolve(sketch);
        }
        {
            var Q0;
            Q0 = qSketchRegion(id + "F146", true);
            extrude(context, id + "F147", {"entities" : qUnion([Q0]), "operationType" : NewBodyOperationType.REMOVE, "oppositeDirection" : true, "depth" : 12.7 * mm, "offsetDistance" : 25.4 * mm});
        }
        {
            var Q0;
            Q0=qCreatedBy(id+"F17.planeOp",FACE);
            var sketch = newSketch(context, id + "F148", { "sketchPlane" : qUnion([Q0])});
            skLineSegment(sketch, "E360.bottom", {"start": v(7315.2, 0) * mm, "end": v(9169.4, 0) * mm});
            skLineSegment(sketch, "E360.top", {"start": v(7315.2, 2133.6) * mm, "end": v(9169.4, 2133.6) * mm});
            skLineSegment(sketch, "E360.left", {"start": v(7315.2, 0) * mm, "end": v(7315.2, 2133.6) * mm});
            skLineSegment(sketch, "E360.right", {"start": v(9169.4, 0) * mm, "end": v(9169.4, 2133.6) * mm});
            skSolve(sketch);
        }
        {
            var Q0;
            Q0 = qSketchRegion(id + "F148", true);
            extrude(context, id + "F149", {"entities" : qUnion([Q0]), "oppositeDirection" : true, "depth" : 88.9 * mm, "offsetDistance" : 25.4 * mm});
        }
        {
            var Q0;
            Q0=makeQuery(id+"F149.opExtrude","CAP_FACE",FACE,{"disambiguationData":[OSD([sQuery(id+"F148.wireOp",EDGE,"E360.bottom"),sQuery(id+"F148.wireOp",EDGE,"E360.top"),sQuery(id+"F148.wireOp",EDGE,"E360.left"),sQuery(id+"F148.wireOp",EDGE,"E360.right")])],"isStart":true});
            var sketch = newSketch(context, id + "F150", { "sketchPlane" : qUnion([Q0])});
            skLineSegment(sketch, "E361.bottom", {"start": v(8255, 0) * mm, "end": v(9150.35, 0) * mm});
            skLineSegment(sketch, "E361.top", {"start": v(8255, 2032) * mm, "end": v(9150.35, 2032) * mm});
            skLineSegment(sketch, "E361.left", {"start": v(8255, 0) * mm, "end": v(8255, 2032) * mm});
            skLineSegment(sketch, "E361.right", {"start": v(9150.35, 0) * mm, "end": v(9150.35, 2032) * mm});
            skSolve(sketch);
        }
        {
            var Q0;
            Q0 = qSketchRegion(id + "F150", true);
            extrude(context, id + "F151", {"entities" : qUnion([Q0]), "operationType" : NewBodyOperationType.REMOVE, "oppositeDirection" : true, "depth" : 26.99 * mm, "offsetDistance" : 25.4 * mm});
        }
        {
            var Q0;
            Q0=makeQuery(id+"F149.opExtrude","CAP_FACE",FACE,{"disambiguationData":[OSD([sQuery(id+"F148.wireOp",EDGE,"E360.bottom"),sQuery(id+"F148.wireOp",EDGE,"E360.top"),sQuery(id+"F148.wireOp",EDGE,"E360.left"),sQuery(id+"F148.wireOp",EDGE,"E360.right")])],"isStart":false});
            var sketch = newSketch(context, id + "F152", { "sketchPlane" : qUnion([Q0])});
            skLineSegment(sketch, "E362.0.0", {"start": v(-8255, 0) * mm, "end": v(-9150.35, 0) * mm});
            skLineSegment(sketch, "E362.0.1", {"start": v(-9150.35, 0) * mm, "end": v(-9150.35, 2032) * mm});
            skLineSegment(sketch, "E362.0.2", {"start": v(-9150.35, 2032) * mm, "end": v(-8255, 2032) * mm});
            skLineSegment(sketch, "E362.0.3", {"start": v(-8255, 2032) * mm, "end": v(-8255, 0) * mm});
            skSolve(sketch);
        }
        {
            var Q0;
            Q0 = qSketchRegion(id + "F152", true);
            extrude(context, id + "F153", {"entities" : qUnion([Q0]), "operationType" : NewBodyOperationType.REMOVE, "oppositeDirection" : true, "depth" : 26.99 * mm, "offsetDistance" : 25.4 * mm});
        }
        {
            var Q0;
            Q0=qCreatedBy(makeId("Top.planeOp"),FACE);
            var sketch = newSketch(context, id + "F154", { "sketchPlane" : qUnion([Q0])});
            skLineSegment(sketch, "E363.bottom", {"start": v(7315.2, 4267.2) * mm, "end": v(8255, 4267.2) * mm});
            skLineSegment(sketch, "E363.top", {"start": v(7315.2, 4178.3) * mm, "end": v(8255, 4178.3) * mm});
            skLineSegment(sketch, "E363.left", {"start": v(7315.2, 4267.2) * mm, "end": v(7315.2, 4178.3) * mm});
            skLineSegment(sketch, "E363.right", {"start": v(8255, 4267.2) * mm, "end": v(8255, 4248.15) * mm});
            skLineSegment(sketch, "E364.bottom", {"start": v(7340.6, 4248.15) * mm, "end": v(8255, 4248.15) * mm});
            skLineSegment(sketch, "E364.top", {"start": v(7340.6, 4197.35) * mm, "end": v(8255, 4197.35) * mm});
            skLineSegment(sketch, "E364.left", {"start": v(7340.6, 4248.15) * mm, "end": v(7340.6, 4222.76) * mm});
            skLineSegment(sketch, "E365.bottom", {"start": v(7467.6, 4240.21) * mm, "end": v(8382, 4240.21) * mm});
            skLineSegment(sketch, "E365.top", {"start": v(7467.6, 4205.29) * mm, "end": v(8382, 4205.29) * mm});
            skLineSegment(sketch, "E365.left", {"start": v(7467.6, 4240.21) * mm, "end": v(7467.6, 4222.76) * mm});
            skLineSegment(sketch, "E365.right", {"start": v(8382, 4240.21) * mm, "end": v(8382, 4205.29) * mm});
            skLineSegment(sketch, "E366.trimOffspring", {"start": v(8255, 4197.35) * mm, "end": v(8255, 4178.3) * mm});
            skLineSegment(sketch, "E367", {"start": v(7340.6, 4222.76) * mm, "end": v(7467.6, 4222.76) * mm});
            skLineSegment(sketch, "E368", {"start": v(7340.6, 4222.74) * mm, "end": v(7467.6, 4222.74) * mm});
            skLineSegment(sketch, "E369.trimOffspring", {"start": v(7340.6, 4222.74) * mm, "end": v(7340.6, 4197.35) * mm});
            skLineSegment(sketch, "E370.trimOffspring", {"start": v(7467.6, 4222.74) * mm, "end": v(7467.6, 4205.29) * mm});
            skSolve(sketch);
        }
        {
            var Q0;
            Q0 = qSketchRegion(id + "F154", true);
            extrude(context, id + "F155", {"entities" : qUnion([Q0]), "depth" : 25.4 * mm, "offsetDistance" : 25.4 * mm});
        }
        {
            var Q0;
            Q0=qCreatedBy(id+"F26.planeOp",FACE);
            var sketch = newSketch(context, id + "F156", { "sketchPlane" : qUnion([Q0])});
            skLineSegment(sketch, "E371.bottom", {"start": v(7315.2, 0) * mm, "end": v(8864.6, 0) * mm});
            skLineSegment(sketch, "E371.top", {"start": v(7315.2, 2146.3) * mm, "end": v(8864.6, 2146.3) * mm});
            skLineSegment(sketch, "E371.left", {"start": v(7315.2, 0) * mm, "end": v(7315.2, 2146.3) * mm});
            skLineSegment(sketch, "E371.right", {"start": v(8864.6, 0) * mm, "end": v(8864.6, 2146.3) * mm});
            skSolve(sketch);
        }
        {
            var Q0;
            Q0 = qSketchRegion(id + "F156", true);
            extrude(context, id + "F157", {"entities" : qUnion([Q0]), "oppositeDirection" : true, "depth" : 88.9 * mm, "offsetDistance" : 25.4 * mm});
        }
        {
            var Q0;
            Q0=makeQuery(id+"F157.opExtrude","CAP_FACE",FACE,{"disambiguationData":[OSD([sQuery(id+"F156.wireOp",EDGE,"E371.bottom"),sQuery(id+"F156.wireOp",EDGE,"E371.top"),sQuery(id+"F156.wireOp",EDGE,"E371.left"),sQuery(id+"F156.wireOp",EDGE,"E371.right")])],"isStart":true});
            var sketch = newSketch(context, id + "F158", { "sketchPlane" : qUnion([Q0])});
            skLineSegment(sketch, "E372.bottom", {"start": v(8102.6, 0) * mm, "end": v(8845.55, 0) * mm});
            skLineSegment(sketch, "E372.top", {"start": v(8102.6, 2032) * mm, "end": v(8845.55, 2032) * mm});
            skLineSegment(sketch, "E372.left", {"start": v(8102.6, 0) * mm, "end": v(8102.6, 2032) * mm});
            skLineSegment(sketch, "E372.right", {"start": v(8845.55, 0) * mm, "end": v(8845.55, 2032) * mm});
            skSolve(sketch);
        }
        {
            var Q0;
            Q0 = qSketchRegion(id + "F158", true);
            extrude(context, id + "F159", {"entities" : qUnion([Q0]), "operationType" : NewBodyOperationType.REMOVE, "oppositeDirection" : true, "depth" : 26.99 * mm, "offsetDistance" : 25.4 * mm});
        }
        {
            var Q0;
            Q0=makeQuery(id+"F157.opExtrude","CAP_FACE",FACE,{"disambiguationData":[OSD([sQuery(id+"F156.wireOp",EDGE,"E371.bottom"),sQuery(id+"F156.wireOp",EDGE,"E371.top"),sQuery(id+"F156.wireOp",EDGE,"E371.left"),sQuery(id+"F156.wireOp",EDGE,"E371.right")])],"isStart":false});
            var sketch = newSketch(context, id + "F160", { "sketchPlane" : qUnion([Q0])});
            skLineSegment(sketch, "E373.0.0", {"start": v(-8102.6, 0) * mm, "end": v(-8845.55, 0) * mm});
            skLineSegment(sketch, "E373.0.1", {"start": v(-8845.55, 0) * mm, "end": v(-8845.55, 2032) * mm});
            skLineSegment(sketch, "E373.0.2", {"start": v(-8845.55, 2032) * mm, "end": v(-8102.6, 2032) * mm});
            skLineSegment(sketch, "E373.0.3", {"start": v(-8102.6, 2032) * mm, "end": v(-8102.6, 0) * mm});
            skSolve(sketch);
        }
        {
            var Q0;
            Q0 = qSketchRegion(id + "F160", true);
            extrude(context, id + "F161", {"entities" : qUnion([Q0]), "operationType" : NewBodyOperationType.REMOVE, "oppositeDirection" : true, "depth" : 26.99 * mm, "offsetDistance" : 25.4 * mm});
        }
        {
            var Q0;
            Q0=qCreatedBy(makeId("Top.planeOp"),FACE);
            var sketch = newSketch(context, id + "F162", { "sketchPlane" : qUnion([Q0])});
            skLineSegment(sketch, "E374", {"start": v(7315.2, 6705.6) * mm, "end": v(8096.25, 6705.6) * mm});
            skLineSegment(sketch, "E375", {"start": v(8096.25, 6705.6) * mm, "end": v(8096.25, 6686.55) * mm});
            skLineSegment(sketch, "E376", {"start": v(8096.25, 6686.55) * mm, "end": v(7334.25, 6686.55) * mm});
            skLineSegment(sketch, "E377", {"start": v(7334.25, 6686.55) * mm, "end": v(7334.25, 6661.16) * mm});
            skLineSegment(sketch, "E378", {"start": v(7334.25, 6661.16) * mm, "end": v(7461.25, 6661.16) * mm});
            skLineSegment(sketch, "E379", {"start": v(7461.25, 6661.16) * mm, "end": v(7461.25, 6678.61) * mm});
            skLineSegment(sketch, "E380", {"start": v(7461.25, 6678.61) * mm, "end": v(8223.25, 6678.61) * mm});
            skLineSegment(sketch, "E381", {"start": v(8223.25, 6678.61) * mm, "end": v(8223.25, 6643.69) * mm});
            skLineSegment(sketch, "E382", {"start": v(8223.25, 6643.69) * mm, "end": v(7461.25, 6643.69) * mm});
            skLineSegment(sketch, "E383", {"start": v(7461.25, 6643.69) * mm, "end": v(7461.25, 6661.14) * mm});
            skLineSegment(sketch, "E384", {"start": v(7461.25, 6661.14) * mm, "end": v(7334.25, 6661.14) * mm});
            skLineSegment(sketch, "E385", {"start": v(7334.25, 6661.14) * mm, "end": v(7334.25, 6635.75) * mm});
            skLineSegment(sketch, "E386", {"start": v(7334.25, 6635.75) * mm, "end": v(8096.25, 6635.75) * mm});
            skLineSegment(sketch, "E387", {"start": v(8096.25, 6635.75) * mm, "end": v(8096.25, 6616.7) * mm});
            skLineSegment(sketch, "E388", {"start": v(8096.25, 6616.7) * mm, "end": v(7315.2, 6616.7) * mm});
            skLineSegment(sketch, "E389", {"start": v(7315.2, 6616.7) * mm, "end": v(7315.2, 6705.6) * mm});
            skSolve(sketch);
        }
        {
            var Q0;
            Q0 = qSketchRegion(id + "F162", true);
            extrude(context, id + "F163", {"entities" : qUnion([Q0]), "depth" : 25.4 * mm, "offsetDistance" : 25.4 * mm});
        }
        {
            var Q0;
            Q0=qCreatedBy(id+"F91.planeOp",FACE);
            cPlane(context, id + "F164", {"entities" : qUnion([Q0]), "cplaneType" : CPlaneType.OFFSET, "offset" : 2438.4 * mm, "oppositeDirection" : true, "width" : 152.4 * mm, "height" : 152.4 * mm});
        }
        {
            var Q0;
            Q0=qCreatedBy(id+"F164.planeOp",FACE);
            var sketch = newSketch(context, id + "F165", { "sketchPlane" : qUnion([Q0])});
            skLineSegment(sketch, "E390.bottom", {"start": v(3657.6, 0) * mm, "end": v(3676.65, 0) * mm});
            skLineSegment(sketch, "E390.top", {"start": v(3657.6, 2076.45) * mm, "end": v(5321.3, 2076.45) * mm});
            skLineSegment(sketch, "E390.left", {"start": v(3657.6, 0) * mm, "end": v(3657.6, 2076.45) * mm});
            skLineSegment(sketch, "E390.right", {"start": v(5321.3, 0) * mm, "end": v(5321.3, 2076.45) * mm});
            skLineSegment(sketch, "E391", {"start": v(3676.65, 0) * mm, "end": v(3676.65, 25.4) * mm});
            skLineSegment(sketch, "E392", {"start": v(3676.65, 25.4) * mm, "end": v(5302.25, 25.4) * mm});
            skLineSegment(sketch, "E393", {"start": v(5302.25, 25.4) * mm, "end": v(5302.25, 0) * mm});
            skLineSegment(sketch, "E394.trimOffspring", {"start": v(5302.25, 0) * mm, "end": v(5321.3, 0) * mm});
            skSolve(sketch);
        }
        {
            var Q0;
            Q0 = qSketchRegion(id + "F165", true);
            extrude(context, id + "F166", {"entities" : qUnion([Q0]), "oppositeDirection" : true, "depth" : 114.3 * mm, "offsetDistance" : 25.4 * mm});
        }
        {
            var Q0;
            Q0=makeQuery(id+"F166.opExtrude","CAP_FACE",FACE,{"disambiguationData":[OSD([sQuery(id+"F165.wireOp",EDGE,"E390.bottom"),sQuery(id+"F165.wireOp",EDGE,"E390.top"),sQuery(id+"F165.wireOp",EDGE,"E390.left"),sQuery(id+"F165.wireOp",EDGE,"E390.right"),sQuery(id+"F165.wireOp",EDGE,"E391"),sQuery(id+"F165.wireOp",EDGE,"E392"),sQuery(id+"F165.wireOp",EDGE,"E393"),sQuery(id+"F165.wireOp",EDGE,"E394.trimOffspring")])],"isStart":true});
            var sketch = newSketch(context, id + "F167", { "sketchPlane" : qUnion([Q0])});
            skLineSegment(sketch, "E395.bottom", {"start": v(3676.65, 25.4) * mm, "end": v(5302.25, 25.4) * mm});
            skLineSegment(sketch, "E395.top", {"start": v(3676.65, 2057.4) * mm, "end": v(5302.25, 2057.4) * mm});
            skLineSegment(sketch, "E395.left", {"start": v(3676.65, 25.4) * mm, "end": v(3676.65, 2057.4) * mm});
            skLineSegment(sketch, "E395.right", {"start": v(5302.25, 25.4) * mm, "end": v(5302.25, 2057.4) * mm});
            skSolve(sketch);
        }
        {
            var Q0;
            Q0 = qSketchRegion(id + "F167", true);
            extrude(context, id + "F168", {"entities" : qUnion([Q0]), "operationType" : NewBodyOperationType.REMOVE, "oppositeDirection" : true, "depth" : 25.4 * mm, "offsetDistance" : 25.4 * mm});
        }
        {
            var Q0;
            Q0=makeQuery(id+"F166.opExtrude","CAP_FACE",FACE,{"disambiguationData":[OSD([sQuery(id+"F165.wireOp",EDGE,"E390.bottom"),sQuery(id+"F165.wireOp",EDGE,"E390.top"),sQuery(id+"F165.wireOp",EDGE,"E390.left"),sQuery(id+"F165.wireOp",EDGE,"E390.right"),sQuery(id+"F165.wireOp",EDGE,"E391"),sQuery(id+"F165.wireOp",EDGE,"E392"),sQuery(id+"F165.wireOp",EDGE,"E393"),sQuery(id+"F165.wireOp",EDGE,"E394.trimOffspring")])],"isStart":false});
            var sketch = newSketch(context, id + "F169", { "sketchPlane" : qUnion([Q0])});
            skLineSegment(sketch, "E396.0.0", {"start": v(-3676.65, 25.4) * mm, "end": v(-5302.25, 25.4) * mm});
            skLineSegment(sketch, "E396.0.1", {"start": v(-5302.25, 25.4) * mm, "end": v(-5302.25, 2057.4) * mm});
            skLineSegment(sketch, "E396.0.2", {"start": v(-5302.25, 2057.4) * mm, "end": v(-3676.65, 2057.4) * mm});
            skLineSegment(sketch, "E396.0.3", {"start": v(-3676.65, 2057.4) * mm, "end": v(-3676.65, 25.4) * mm});
            skSolve(sketch);
        }
        {
            var Q0;
            Q0 = qSketchRegion(id + "F169", true);
            extrude(context, id + "F170", {"entities" : qUnion([Q0]), "operationType" : NewBodyOperationType.REMOVE, "oppositeDirection" : true, "depth" : 57.15 * mm, "offsetDistance" : 25.4 * mm});
        }
        {
            var Q0;
            Q0=makeQuery(id+"F170.boolean.opBoolean","COPY",FACE,{"derivedFrom":makeQuery(id+"F170.opExtrude","CAP_FACE",FACE,{"disambiguationData":[OSD([sQuery(id+"F169.wireOp",EDGE,"E396.0.0"),sQuery(id+"F169.wireOp",EDGE,"E396.0.1"),sQuery(id+"F169.wireOp",EDGE,"E396.0.2"),sQuery(id+"F169.wireOp",EDGE,"E396.0.3")])],"isStart":false})});
            var sketch = newSketch(context, id + "F171", { "sketchPlane" : qUnion([Q0])});
            skLineSegment(sketch, "E397.bottom", {"start": v(-4895.87, 25.4) * mm, "end": v(-4895.84, 25.4) * mm});
            skLineSegment(sketch, "E397.top", {"start": v(-4895.87, 2057.4) * mm, "end": v(-4895.84, 2057.4) * mm});
            skLineSegment(sketch, "E397.left", {"start": v(-4895.87, 25.4) * mm, "end": v(-4895.87, 2057.4) * mm});
            skLineSegment(sketch, "E397.right", {"start": v(-4895.84, 25.4) * mm, "end": v(-4895.84, 2057.4) * mm});
            skLineSegment(sketch, "E398.bottom", {"start": v(-4489.46, 25.4) * mm, "end": v(-4489.44, 25.4) * mm});
            skLineSegment(sketch, "E398.top", {"start": v(-4489.46, 2057.4) * mm, "end": v(-4489.44, 2057.4) * mm});
            skLineSegment(sketch, "E398.left", {"start": v(-4489.46, 25.4) * mm, "end": v(-4489.46, 2057.4) * mm});
            skLineSegment(sketch, "E398.right", {"start": v(-4489.44, 25.4) * mm, "end": v(-4489.44, 2057.4) * mm});
            skLineSegment(sketch, "E399.bottom", {"start": v(-4083.06, 25.4) * mm, "end": v(-4083.03, 25.4) * mm});
            skLineSegment(sketch, "E399.top", {"start": v(-4083.06, 2057.4) * mm, "end": v(-4083.03, 2057.4) * mm});
            skLineSegment(sketch, "E399.left", {"start": v(-4083.06, 25.4) * mm, "end": v(-4083.06, 2057.4) * mm});
            skLineSegment(sketch, "E399.right", {"start": v(-4083.03, 25.4) * mm, "end": v(-4083.03, 2057.4) * mm});
            skLineSegment(sketch, "E400", {"start": v(-4895.87, 1041.4) * mm, "end": v(-5302.25, 1041.4) * mm, "construction": true});
            skLineSegment(sketch, "E401", {"start": v(-4895.84, 1041.4) * mm, "end": v(-4489.46, 1041.4) * mm, "construction": true});
            skLineSegment(sketch, "E402", {"start": v(-4489.44, 1041.4) * mm, "end": v(-4083.06, 1041.4) * mm, "construction": true});
            skLineSegment(sketch, "E403", {"start": v(-4083.03, 1041.4) * mm, "end": v(-3676.65, 1041.4) * mm, "construction": true});
            skSolve(sketch);
        }
        {
            var Q0;
            Q0 = qSketchRegion(id + "F171", true);
            var Q1;
            Q1=makeQuery(id+"F168.boolean.opBoolean","COPY",FACE,{"derivedFrom":makeQuery(id+"F168.opExtrude","CAP_FACE",FACE,{"disambiguationData":[OSD([sQuery(id+"F167.wireOp",EDGE,"E395.bottom"),sQuery(id+"F167.wireOp",EDGE,"E395.top"),sQuery(id+"F167.wireOp",EDGE,"E395.left"),sQuery(id+"F167.wireOp",EDGE,"E395.right")])],"isStart":false})});
            extrude(context, id + "F172", {"entities" : qUnion([Q0]), "operationType" : NewBodyOperationType.REMOVE, "endBound" : BoundingType.UP_TO_SURFACE, "oppositeDirection" : true, "depth" : 25.4 * mm, "endBoundEntityFace" : qUnion([Q1]), "offsetDistance" : 25.4 * mm});
        }
        {
            var Q0;
            Q0=qCreatedBy(makeId("Top.planeOp"),FACE);
            var sketch = newSketch(context, id + "F173", { "sketchPlane" : qUnion([Q0])});
            skLineSegment(sketch, "E404.bottom", {"start": v(3657.6, 16459.2) * mm, "end": v(3676.65, 16459.2) * mm});
            skLineSegment(sketch, "E404.top", {"start": v(3657.6, 16344.9) * mm, "end": v(3676.65, 16344.9) * mm});
            skLineSegment(sketch, "E404.left", {"start": v(3657.6, 16459.2) * mm, "end": v(3657.6, 16344.9) * mm});
            skLineSegment(sketch, "E404.right", {"start": v(3676.65, 16459.2) * mm, "end": v(3676.65, 16370.33) * mm});
            skLineSegment(sketch, "E405.bottom", {"start": v(5321.3, 16459.2) * mm, "end": v(5302.25, 16459.2) * mm});
            skLineSegment(sketch, "E405.top", {"start": v(5321.3, 16344.9) * mm, "end": v(5302.25, 16344.9) * mm});
            skLineSegment(sketch, "E405.left", {"start": v(5321.3, 16459.2) * mm, "end": v(5321.3, 16344.9) * mm});
            skLineSegment(sketch, "E405.right", {"start": v(5302.25, 16459.2) * mm, "end": v(5302.25, 16370.33) * mm});
            skLineSegment(sketch, "E406", {"start": v(3676.65, 16386.17) * mm, "end": v(5302.25, 16386.17) * mm, "construction": true});
            skLineSegment(sketch, "E407", {"start": v(3704.69, 16386.18) * mm, "end": v(3696.75, 16399.92) * mm, "construction": true});
            skLineSegment(sketch, "E408", {"start": v(3683, 16391.99) * mm, "end": v(3710.5, 16407.86) * mm});
            skLineSegment(sketch, "E409", {"start": v(3710.5, 16407.86) * mm, "end": v(3732.17, 16370.33) * mm});
            skLineSegment(sketch, "E410", {"start": v(3912.32, 16055.11) * mm, "end": v(3886.2, 16040.03) * mm});
            skLineSegment(sketch, "E411", {"start": v(3886.2, 16040.03) * mm, "end": v(3695.52, 16370.3) * mm});
            skLineSegment(sketch, "E412", {"start": v(3914.5, 16057.28) * mm, "end": v(4095.21, 16370.3) * mm});
            skLineSegment(sketch, "E413", {"start": v(4116.9, 16407.86) * mm, "end": v(4144.4, 16391.99) * mm});
            skLineSegment(sketch, "E414", {"start": v(4144.4, 16391.99) * mm, "end": v(4131.89, 16370.33) * mm});
            skLineSegment(sketch, "E415", {"start": v(3941.2, 16040.03) * mm, "end": v(3915.07, 16055.11) * mm});
            skArc(sketch, "E416", {"start": v(3912.32, 16055.11) * mm, "mid": v(3913.7, 16054.32) * mm, "end": v(3915.07, 16055.11) * mm});
            skArc(sketch, "E417.trimOffspring", {"start": v(3914.5, 16057.28) * mm, "mid": v(3913.7, 16057.5) * mm, "end": v(3912.9, 16057.28) * mm});
            skLineSegment(sketch, "E418", {"start": v(4862, 16407.86) * mm, "end": v(4834.5, 16391.99) * mm});
            skLineSegment(sketch, "E419", {"start": v(4834.5, 16391.99) * mm, "end": v(4847.01, 16370.33) * mm});
            skLineSegment(sketch, "E420", {"start": v(5037.7, 16040.03) * mm, "end": v(5063.83, 16055.11) * mm});
            skLineSegment(sketch, "E421", {"start": v(5066.58, 16055.11) * mm, "end": v(5092.7, 16040.03) * mm});
            skLineSegment(sketch, "E422", {"start": v(5092.7, 16040.03) * mm, "end": v(5283.38, 16370.3) * mm});
            skLineSegment(sketch, "E423", {"start": v(5295.9, 16391.99) * mm, "end": v(5268.4, 16407.86) * mm});
            skLineSegment(sketch, "E424", {"start": v(5268.4, 16407.86) * mm, "end": v(5246.73, 16370.33) * mm});
            skLineSegment(sketch, "E425", {"start": v(4862, 16407.86) * mm, "end": v(4883.67, 16370.33) * mm});
            skLineSegment(sketch, "E426", {"start": v(3676.65, 16370.3) * mm, "end": v(3695.52, 16370.3) * mm});
            skLineSegment(sketch, "E427", {"start": v(5302.25, 16370.33) * mm, "end": v(5283.4, 16370.33) * mm});
            skLineSegment(sketch, "E428.trimOffspring", {"start": v(3676.65, 16370.3) * mm, "end": v(3676.65, 16344.9) * mm});
            skLineSegment(sketch, "E429.trimOffspring", {"start": v(3695.5, 16370.33) * mm, "end": v(3683, 16391.99) * mm});
            skLineSegment(sketch, "E430.trimOffspring", {"start": v(3732.18, 16370.3) * mm, "end": v(3912.9, 16057.28) * mm});
            skLineSegment(sketch, "E431.trimOffspring", {"start": v(4131.87, 16370.3) * mm, "end": v(3941.2, 16040.03) * mm});
            skLineSegment(sketch, "E432.trimOffspring", {"start": v(4095.23, 16370.33) * mm, "end": v(4116.9, 16407.86) * mm});
            skLineSegment(sketch, "E433.trimOffspring", {"start": v(4095.23, 16370.33) * mm, "end": v(3732.17, 16370.33) * mm});
            skLineSegment(sketch, "E434.trimOffspring", {"start": v(4131.87, 16370.3) * mm, "end": v(4847.03, 16370.3) * mm});
            skLineSegment(sketch, "E435.trimOffspring", {"start": v(5283.4, 16370.33) * mm, "end": v(5295.9, 16391.99) * mm});
            skLineSegment(sketch, "E436.trimOffspring", {"start": v(5246.72, 16370.3) * mm, "end": v(5066, 16057.28) * mm});
            skLineSegment(sketch, "E437.trimOffspring", {"start": v(5246.73, 16370.33) * mm, "end": v(4883.67, 16370.33) * mm});
            skLineSegment(sketch, "E438.trimOffspring", {"start": v(5283.38, 16370.3) * mm, "end": v(5302.25, 16370.3) * mm});
            skLineSegment(sketch, "E439.trimOffspring", {"start": v(4847.01, 16370.33) * mm, "end": v(4131.89, 16370.33) * mm});
            skLineSegment(sketch, "E440.trimOffspring", {"start": v(4847.03, 16370.3) * mm, "end": v(5037.7, 16040.03) * mm});
            skLineSegment(sketch, "E441.trimOffspring", {"start": v(4883.69, 16370.3) * mm, "end": v(5246.72, 16370.3) * mm});
            skLineSegment(sketch, "E442.trimOffspring", {"start": v(4883.69, 16370.3) * mm, "end": v(5064.4, 16057.28) * mm});
            skLineSegment(sketch, "E443.trimOffspring", {"start": v(5302.25, 16370.3) * mm, "end": v(5302.25, 16344.9) * mm});
            skArc(sketch, "E444", {"start": v(5063.83, 16055.11) * mm, "mid": v(5065.2, 16054.32) * mm, "end": v(5066.58, 16055.11) * mm});
            skArc(sketch, "E445.trimOffspring", {"start": v(5066, 16057.28) * mm, "mid": v(5065.2, 16057.5) * mm, "end": v(5064.4, 16057.28) * mm});
            skLineSegment(sketch, "E446.trimOffspring", {"start": v(3695.5, 16370.33) * mm, "end": v(3676.65, 16370.33) * mm});
            skLineSegment(sketch, "E447.trimOffspring", {"start": v(3732.18, 16370.3) * mm, "end": v(4095.21, 16370.3) * mm});
            skSolve(sketch);
        }
        {
            var Q0;
            Q0=makeQuery(id+"F173.imprint","IMPRINT",FACE,{"disambiguationData":[TD([[makeQuery(id+"F173.imprint","IMPRINT",EDGE,{"derivedFrom":sQuery(id+"F173.wireOp",EDGE,"E404.bottom")}),-1.0]])]});
            extrude(context, id + "F174", {"entities" : qUnion([Q0]), "depth" : 25.4 * mm, "offsetDistance" : 25.4 * mm});
        }
        {
            var Q0;
            Q0=qCreatedBy(id+"F164.planeOp",FACE);
            cPlane(context, id + "F175", {"entities" : qUnion([Q0]), "cplaneType" : CPlaneType.OFFSET, "offset" : 2438.4 * mm, "oppositeDirection" : true, "width" : 152.4 * mm, "height" : 152.4 * mm});
        }
        {
            var Q0;
            Q0=qCreatedBy(id+"F175.planeOp",FACE);
            var sketch = newSketch(context, id + "F176", { "sketchPlane" : qUnion([Q0])});
            skLineSegment(sketch, "E448.bottom", {"start": v(3657.6, 0) * mm, "end": v(3676.65, 0) * mm});
            skLineSegment(sketch, "E448.top", {"start": v(3657.6, 2076.45) * mm, "end": v(5219.7, 2076.45) * mm});
            skLineSegment(sketch, "E448.left", {"start": v(3657.6, 0) * mm, "end": v(3657.6, 2076.45) * mm});
            skLineSegment(sketch, "E448.right", {"start": v(5219.7, 0) * mm, "end": v(5219.7, 2076.45) * mm});
            skLineSegment(sketch, "E449", {"start": v(3676.65, 0) * mm, "end": v(3676.65, 25.4) * mm});
            skLineSegment(sketch, "E450", {"start": v(3676.65, 25.4) * mm, "end": v(5200.65, 25.4) * mm});
            skLineSegment(sketch, "E451", {"start": v(5200.65, 25.4) * mm, "end": v(5200.65, 0) * mm});
            skLineSegment(sketch, "E452.trimOffspring", {"start": v(5200.65, 0) * mm, "end": v(5219.7, 0) * mm});
            skSolve(sketch);
        }
        {
            var Q0;
            Q0 = qSketchRegion(id + "F176", true);
            extrude(context, id + "F177", {"entities" : qUnion([Q0]), "oppositeDirection" : true, "depth" : 114.3 * mm, "offsetDistance" : 25.4 * mm});
        }
        {
            var Q0;
            Q0=makeQuery(id+"F177.opExtrude","CAP_FACE",FACE,{"disambiguationData":[OSD([sQuery(id+"F176.wireOp",EDGE,"E448.bottom"),sQuery(id+"F176.wireOp",EDGE,"E448.top"),sQuery(id+"F176.wireOp",EDGE,"E448.left"),sQuery(id+"F176.wireOp",EDGE,"E448.right"),sQuery(id+"F176.wireOp",EDGE,"E449"),sQuery(id+"F176.wireOp",EDGE,"E450"),sQuery(id+"F176.wireOp",EDGE,"E451"),sQuery(id+"F176.wireOp",EDGE,"E452.trimOffspring")])],"isStart":true});
            var sketch = newSketch(context, id + "F178", { "sketchPlane" : qUnion([Q0])});
            skLineSegment(sketch, "E453.bottom", {"start": v(3676.65, 25.4) * mm, "end": v(5200.65, 25.4) * mm});
            skLineSegment(sketch, "E453.top", {"start": v(3676.65, 2057.4) * mm, "end": v(5200.65, 2057.4) * mm});
            skLineSegment(sketch, "E453.left", {"start": v(3676.65, 25.4) * mm, "end": v(3676.65, 2057.4) * mm});
            skLineSegment(sketch, "E453.right", {"start": v(5200.65, 25.4) * mm, "end": v(5200.65, 2057.4) * mm});
            skSolve(sketch);
        }
        {
            var Q0;
            Q0 = qSketchRegion(id + "F178", true);
            extrude(context, id + "F179", {"entities" : qUnion([Q0]), "operationType" : NewBodyOperationType.REMOVE, "oppositeDirection" : true, "depth" : 25.4 * mm, "offsetDistance" : 25.4 * mm});
        }
        {
            var Q0;
            Q0=makeQuery(id+"F177.opExtrude","CAP_FACE",FACE,{"disambiguationData":[OSD([sQuery(id+"F176.wireOp",EDGE,"E448.bottom"),sQuery(id+"F176.wireOp",EDGE,"E448.top"),sQuery(id+"F176.wireOp",EDGE,"E448.left"),sQuery(id+"F176.wireOp",EDGE,"E448.right"),sQuery(id+"F176.wireOp",EDGE,"E449"),sQuery(id+"F176.wireOp",EDGE,"E450"),sQuery(id+"F176.wireOp",EDGE,"E451"),sQuery(id+"F176.wireOp",EDGE,"E452.trimOffspring")])],"isStart":false});
            var sketch = newSketch(context, id + "F180", { "sketchPlane" : qUnion([Q0])});
            skLineSegment(sketch, "E454.0.0", {"start": v(-3676.65, 25.4) * mm, "end": v(-5200.65, 25.4) * mm});
            skLineSegment(sketch, "E454.0.1", {"start": v(-5200.65, 25.4) * mm, "end": v(-5200.65, 2057.4) * mm});
            skLineSegment(sketch, "E454.0.2", {"start": v(-5200.65, 2057.4) * mm, "end": v(-3676.65, 2057.4) * mm});
            skLineSegment(sketch, "E454.0.3", {"start": v(-3676.65, 2057.4) * mm, "end": v(-3676.65, 25.4) * mm});
            skSolve(sketch);
        }
        {
            var Q0;
            Q0 = qSketchRegion(id + "F180", true);
            extrude(context, id + "F181", {"entities" : qUnion([Q0]), "operationType" : NewBodyOperationType.REMOVE, "oppositeDirection" : true, "depth" : 57.15 * mm, "offsetDistance" : 25.4 * mm});
        }
        {
            var Q0;
            Q0=makeQuery(id+"F181.boolean.opBoolean","COPY",FACE,{"derivedFrom":makeQuery(id+"F181.opExtrude","CAP_FACE",FACE,{"disambiguationData":[OSD([sQuery(id+"F180.wireOp",EDGE,"E454.0.0"),sQuery(id+"F180.wireOp",EDGE,"E454.0.1"),sQuery(id+"F180.wireOp",EDGE,"E454.0.2"),sQuery(id+"F180.wireOp",EDGE,"E454.0.3")])],"isStart":false})});
            var sketch = newSketch(context, id + "F182", { "sketchPlane" : qUnion([Q0])});
            skLineSegment(sketch, "E455.bottom", {"start": v(-4819.67, 25.4) * mm, "end": v(-4819.64, 25.4) * mm});
            skLineSegment(sketch, "E455.top", {"start": v(-4819.67, 2057.4) * mm, "end": v(-4819.64, 2057.4) * mm});
            skLineSegment(sketch, "E455.left", {"start": v(-4819.67, 25.4) * mm, "end": v(-4819.67, 2057.4) * mm});
            skLineSegment(sketch, "E455.right", {"start": v(-4819.64, 25.4) * mm, "end": v(-4819.64, 2057.4) * mm});
            skLineSegment(sketch, "E456.bottom", {"start": v(-4438.66, 25.4) * mm, "end": v(-4438.64, 25.4) * mm});
            skLineSegment(sketch, "E456.top", {"start": v(-4438.66, 2057.4) * mm, "end": v(-4438.64, 2057.4) * mm});
            skLineSegment(sketch, "E456.left", {"start": v(-4438.66, 25.4) * mm, "end": v(-4438.66, 2057.4) * mm});
            skLineSegment(sketch, "E456.right", {"start": v(-4438.64, 25.4) * mm, "end": v(-4438.64, 2057.4) * mm});
            skLineSegment(sketch, "E457.bottom", {"start": v(-4057.66, 25.4) * mm, "end": v(-4057.63, 25.4) * mm});
            skLineSegment(sketch, "E457.top", {"start": v(-4057.66, 2057.4) * mm, "end": v(-4057.63, 2057.4) * mm});
            skLineSegment(sketch, "E457.left", {"start": v(-4057.66, 25.4) * mm, "end": v(-4057.66, 2057.4) * mm});
            skLineSegment(sketch, "E457.right", {"start": v(-4057.63, 25.4) * mm, "end": v(-4057.63, 2057.4) * mm});
            skLineSegment(sketch, "E458", {"start": v(-4819.67, 2057.4) * mm, "end": v(-5200.65, 2057.4) * mm, "construction": true});
            skLineSegment(sketch, "E459", {"start": v(-4819.64, 2057.4) * mm, "end": v(-4438.66, 2057.4) * mm, "construction": true});
            skLineSegment(sketch, "E460", {"start": v(-4438.64, 2057.4) * mm, "end": v(-4057.66, 2057.4) * mm, "construction": true});
            skLineSegment(sketch, "E461", {"start": v(-4057.63, 2057.4) * mm, "end": v(-3676.65, 2057.4) * mm, "construction": true});
            skSolve(sketch);
        }
        {
            var Q0;
            Q0 = qSketchRegion(id + "F182", true);
            var Q1;
            Q1=makeQuery(id+"F179.boolean.opBoolean","COPY",FACE,{"derivedFrom":makeQuery(id+"F179.opExtrude","CAP_FACE",FACE,{"disambiguationData":[OSD([sQuery(id+"F178.wireOp",EDGE,"E453.bottom"),sQuery(id+"F178.wireOp",EDGE,"E453.top"),sQuery(id+"F178.wireOp",EDGE,"E453.left"),sQuery(id+"F178.wireOp",EDGE,"E453.right")])],"isStart":false})});
            extrude(context, id + "F183", {"entities" : qUnion([Q0]), "operationType" : NewBodyOperationType.REMOVE, "endBound" : BoundingType.UP_TO_SURFACE, "oppositeDirection" : true, "depth" : 25.4 * mm, "endBoundEntityFace" : qUnion([Q1]), "offsetDistance" : 25.4 * mm});
        }
        {
            var Q0;
            Q0=qCreatedBy(makeId("Top.planeOp"),FACE);
            var sketch = newSketch(context, id + "F184", { "sketchPlane" : qUnion([Q0])});
            skLineSegment(sketch, "E462.bottom", {"start": v(3657.6, 18897.6) * mm, "end": v(3676.65, 18897.6) * mm});
            skLineSegment(sketch, "E462.top", {"start": v(3657.6, 18783.3) * mm, "end": v(3676.65, 18783.3) * mm});
            skLineSegment(sketch, "E462.left", {"start": v(3657.6, 18897.6) * mm, "end": v(3657.6, 18783.3) * mm});
            skLineSegment(sketch, "E462.right", {"start": v(3676.65, 18897.6) * mm, "end": v(3676.65, 18808.73) * mm});
            skLineSegment(sketch, "E463.bottom", {"start": v(5219.7, 18897.6) * mm, "end": v(5200.65, 18897.6) * mm});
            skLineSegment(sketch, "E463.top", {"start": v(5219.7, 18783.3) * mm, "end": v(5200.65, 18783.3) * mm});
            skLineSegment(sketch, "E463.left", {"start": v(5219.7, 18897.6) * mm, "end": v(5219.7, 18783.3) * mm});
            skLineSegment(sketch, "E463.right", {"start": v(5200.65, 18897.6) * mm, "end": v(5200.65, 18808.73) * mm});
            skLineSegment(sketch, "E464", {"start": v(3683, 18820.86) * mm, "end": v(3690, 18808.73) * mm});
            skLineSegment(sketch, "E465", {"start": v(3873.5, 18490.9) * mm, "end": v(3898.25, 18505.2) * mm});
            skLineSegment(sketch, "E466", {"start": v(3899.4, 18509.53) * mm, "end": v(3726.68, 18808.7) * mm});
            skLineSegment(sketch, "E467", {"start": v(3710.5, 18836.74) * mm, "end": v(3683, 18820.86) * mm});
            skLineSegment(sketch, "E468", {"start": v(3902.58, 18509.53) * mm, "end": v(4075.3, 18808.7) * mm});
            skLineSegment(sketch, "E469", {"start": v(4091.5, 18836.74) * mm, "end": v(4119, 18820.86) * mm});
            skLineSegment(sketch, "E470", {"start": v(4119, 18820.86) * mm, "end": v(4111.99, 18808.73) * mm});
            skLineSegment(sketch, "E471", {"start": v(3928.5, 18490.9) * mm, "end": v(3903.75, 18505.2) * mm});
            skLineSegment(sketch, "E472", {"start": v(4785.8, 18836.74) * mm, "end": v(4801.98, 18808.73) * mm});
            skLineSegment(sketch, "E473", {"start": v(4973.55, 18505.2) * mm, "end": v(4948.8, 18490.9) * mm});
            skLineSegment(sketch, "E474", {"start": v(4948.8, 18490.9) * mm, "end": v(4765.33, 18808.7) * mm});
            skLineSegment(sketch, "E475", {"start": v(4758.3, 18820.86) * mm, "end": v(4785.8, 18836.74) * mm});
            skLineSegment(sketch, "E476", {"start": v(4977.9, 18509.53) * mm, "end": v(5150.62, 18808.7) * mm});
            skLineSegment(sketch, "E477", {"start": v(5166.8, 18836.74) * mm, "end": v(5194.3, 18820.86) * mm});
            skLineSegment(sketch, "E478", {"start": v(5194.3, 18820.86) * mm, "end": v(5187.3, 18808.73) * mm});
            skLineSegment(sketch, "E479", {"start": v(5003.8, 18490.9) * mm, "end": v(4979.05, 18505.2) * mm});
            skLineSegment(sketch, "E480", {"start": v(3676.65, 18808.7) * mm, "end": v(3690.02, 18808.7) * mm});
            skLineSegment(sketch, "E481", {"start": v(3676.65, 18808.73) * mm, "end": v(3690, 18808.73) * mm});
            skLineSegment(sketch, "E482", {"start": v(3676.65, 18815.05) * mm, "end": v(5200.65, 18815.05) * mm, "construction": true});
            skLineSegment(sketch, "E483", {"start": v(3704.69, 18815.05) * mm, "end": v(3696.75, 18828.8) * mm, "construction": true});
            skLineSegment(sketch, "E484.trimOffspring", {"start": v(3676.65, 18808.7) * mm, "end": v(3676.65, 18783.3) * mm});
            skLineSegment(sketch, "E485.trimOffspring", {"start": v(3690.02, 18808.7) * mm, "end": v(3873.5, 18490.9) * mm});
            skLineSegment(sketch, "E486.trimOffspring", {"start": v(3726.67, 18808.73) * mm, "end": v(4075.32, 18808.73) * mm});
            skLineSegment(sketch, "E487.trimOffspring", {"start": v(3726.68, 18808.7) * mm, "end": v(4075.3, 18808.7) * mm});
            skLineSegment(sketch, "E488.trimOffspring", {"start": v(3726.67, 18808.73) * mm, "end": v(3710.5, 18836.74) * mm});
            skLineSegment(sketch, "E489.trimOffspring", {"start": v(4075.32, 18808.73) * mm, "end": v(4091.5, 18836.74) * mm});
            skLineSegment(sketch, "E490.trimOffspring", {"start": v(4111.99, 18808.73) * mm, "end": v(4765.31, 18808.73) * mm});
            skLineSegment(sketch, "E491.trimOffspring", {"start": v(4111.97, 18808.7) * mm, "end": v(4765.33, 18808.7) * mm});
            skLineSegment(sketch, "E492.trimOffspring", {"start": v(4111.97, 18808.7) * mm, "end": v(3928.5, 18490.9) * mm});
            skLineSegment(sketch, "E493.trimOffspring", {"start": v(4765.31, 18808.73) * mm, "end": v(4758.3, 18820.86) * mm});
            skLineSegment(sketch, "E494.trimOffspring", {"start": v(4802, 18808.7) * mm, "end": v(4974.72, 18509.53) * mm});
            skLineSegment(sketch, "E495.trimOffspring", {"start": v(4801.98, 18808.73) * mm, "end": v(5150.63, 18808.73) * mm});
            skLineSegment(sketch, "E496.trimOffspring", {"start": v(4802, 18808.7) * mm, "end": v(5150.62, 18808.7) * mm});
            skLineSegment(sketch, "E497.trimOffspring", {"start": v(5200.65, 18808.7) * mm, "end": v(5200.65, 18783.3) * mm});
            skLineSegment(sketch, "E498.trimOffspring", {"start": v(5187.28, 18808.7) * mm, "end": v(5003.8, 18490.9) * mm});
            skLineSegment(sketch, "E499.trimOffspring", {"start": v(5150.63, 18808.73) * mm, "end": v(5166.8, 18836.74) * mm});
            skLineSegment(sketch, "E500.trimOffspring", {"start": v(5187.3, 18808.73) * mm, "end": v(5200.65, 18808.73) * mm});
            skLineSegment(sketch, "E501.trimOffspring", {"start": v(5187.28, 18808.7) * mm, "end": v(5200.65, 18808.7) * mm});
            skArc(sketch, "E502", {"start": v(3898.25, 18505.2) * mm, "mid": v(3901, 18503.6) * mm, "end": v(3903.75, 18505.2) * mm});
            skArc(sketch, "E503", {"start": v(4973.55, 18505.2) * mm, "mid": v(4976.3, 18503.6) * mm, "end": v(4979.05, 18505.2) * mm});
            skArc(sketch, "E504.trimOffspring", {"start": v(4977.9, 18509.53) * mm, "mid": v(4976.3, 18509.95) * mm, "end": v(4974.72, 18509.53) * mm});
            skArc(sketch, "E505.trimOffspring", {"start": v(3902.58, 18509.53) * mm, "mid": v(3901, 18509.95) * mm, "end": v(3899.4, 18509.53) * mm});
            skSolve(sketch);
        }
        {
            var Q0;
            Q0=makeQuery(id+"F184.imprint","IMPRINT",FACE,{"disambiguationData":[TD([[makeQuery(id+"F184.imprint","IMPRINT",EDGE,{"derivedFrom":sQuery(id+"F184.wireOp",EDGE,"E462.bottom")}),-1.0]])]});
            extrude(context, id + "F185", {"entities" : qUnion([Q0]), "depth" : 25.4 * mm, "offsetDistance" : 25.4 * mm});
        }
        {
            var Q0;
            Q0=qCreatedBy(id+"F91.planeOp",FACE);
            var sketch = newSketch(context, id + "F186", { "sketchPlane" : qUnion([Q0])});
            skLineSegment(sketch, "E506.bottom", {"start": v(0, 0) * mm, "end": v(914.4, 0) * mm});
            skLineSegment(sketch, "E506.top", {"start": v(0, 1219.2) * mm, "end": v(914.4, 1219.2) * mm});
            skLineSegment(sketch, "E506.left", {"start": v(0, 0) * mm, "end": v(0, 1219.2) * mm});
            skLineSegment(sketch, "E506.right", {"start": v(914.4, 0) * mm, "end": v(914.4, 1219.2) * mm});
            skSolve(sketch);
        }
        {
            var Q0;
            Q0 = qSketchRegion(id + "F186", true);
            extrude(context, id + "F187", {"entities" : qUnion([Q0]), "oppositeDirection" : true, "depth" : 165.1 * mm, "offsetDistance" : 25.4 * mm});
        }
        {
            var Q0;
            Q0=makeQuery(id+"F187.opExtrude","CAP_FACE",FACE,{"disambiguationData":[OSD([sQuery(id+"F186.wireOp",EDGE,"E506.bottom"),sQuery(id+"F186.wireOp",EDGE,"E506.top"),sQuery(id+"F186.wireOp",EDGE,"E506.left"),sQuery(id+"F186.wireOp",EDGE,"E506.right")])],"isStart":true});
            var sketch = newSketch(context, id + "F188", { "sketchPlane" : qUnion([Q0])});
            skLineSegment(sketch, "E507.bottom", {"start": v(50.8, 1168.4) * mm, "end": v(863.6, 1168.4) * mm});
            skLineSegment(sketch, "E507.top", {"start": v(50.8, 50.8) * mm, "end": v(863.6, 50.8) * mm});
            skLineSegment(sketch, "E507.left", {"start": v(50.8, 1168.4) * mm, "end": v(50.8, 50.8) * mm});
            skLineSegment(sketch, "E507.right", {"start": v(863.6, 1168.4) * mm, "end": v(863.6, 50.8) * mm});
            skSolve(sketch);
        }
        {
            var Q0;
            Q0 = qSketchRegion(id + "F188", true);
            extrude(context, id + "F189", {"entities" : qUnion([Q0]), "operationType" : NewBodyOperationType.REMOVE, "oppositeDirection" : true, "depth" : 12.7 * mm, "offsetDistance" : 25.4 * mm});
        }
        {
            var Q0;
            Q0=makeQuery(id+"F187.opExtrude","CAP_FACE",FACE,{"disambiguationData":[OSD([sQuery(id+"F186.wireOp",EDGE,"E506.bottom"),sQuery(id+"F186.wireOp",EDGE,"E506.top"),sQuery(id+"F186.wireOp",EDGE,"E506.left"),sQuery(id+"F186.wireOp",EDGE,"E506.right")])],"isStart":false});
            var sketch = newSketch(context, id + "F190", { "sketchPlane" : qUnion([Q0])});
            skLineSegment(sketch, "E508.bottom", {"start": v(-895.35, 1200.15) * mm, "end": v(-19.05, 1200.15) * mm});
            skLineSegment(sketch, "E508.top", {"start": v(-895.35, 19.05) * mm, "end": v(-19.05, 19.05) * mm});
            skLineSegment(sketch, "E508.left", {"start": v(-895.35, 1200.15) * mm, "end": v(-895.35, 19.05) * mm});
            skLineSegment(sketch, "E508.right", {"start": v(-19.05, 1200.15) * mm, "end": v(-19.05, 19.05) * mm});
            skSolve(sketch);
        }
        {
            var Q0;
            Q0 = qSketchRegion(id + "F190", true);
            extrude(context, id + "F191", {"entities" : qUnion([Q0]), "operationType" : NewBodyOperationType.REMOVE, "oppositeDirection" : true, "depth" : 114.3 * mm, "offsetDistance" : 25.4 * mm});
        }
        {
            var Q0;
            Q0=makeQuery(id+"F191.boolean.opBoolean","COPY",FACE,{"derivedFrom":makeQuery(id+"F191.opExtrude","CAP_FACE",FACE,{"disambiguationData":[OSD([sQuery(id+"F190.wireOp",EDGE,"E508.bottom"),sQuery(id+"F190.wireOp",EDGE,"E508.top"),sQuery(id+"F190.wireOp",EDGE,"E508.left"),sQuery(id+"F190.wireOp",EDGE,"E508.right")])],"isStart":false})});
            var sketch = newSketch(context, id + "F192", { "sketchPlane" : qUnion([Q0])});
            skLineSegment(sketch, "E509.0.0", {"start": v(-50.8, 1168.4) * mm, "end": v(-50.8, 50.8) * mm});
            skLineSegment(sketch, "E509.0.1", {"start": v(-50.8, 50.8) * mm, "end": v(-863.6, 50.8) * mm});
            skLineSegment(sketch, "E509.0.2", {"start": v(-863.6, 50.8) * mm, "end": v(-863.6, 1168.4) * mm});
            skLineSegment(sketch, "E509.0.3", {"start": v(-863.6, 1168.4) * mm, "end": v(-50.8, 1168.4) * mm});
            skSolve(sketch);
        }
        {
            var Q0;
            Q0 = qSketchRegion(id + "F192", true);
            extrude(context, id + "F193", {"entities" : qUnion([Q0]), "operationType" : NewBodyOperationType.REMOVE, "oppositeDirection" : true, "depth" : 12.7 * mm, "offsetDistance" : 25.4 * mm});
        }
        {
            var Q0;
            Q0=qCreatedBy(id+"F164.planeOp",FACE);
            var sketch = newSketch(context, id + "F194", { "sketchPlane" : qUnion([Q0])});
            skLineSegment(sketch, "E510.bottom", {"start": v(0, 0) * mm, "end": v(457.2, 0) * mm});
            skLineSegment(sketch, "E510.top", {"start": v(0, 1219.2) * mm, "end": v(457.2, 1219.2) * mm});
            skLineSegment(sketch, "E510.left", {"start": v(0, 0) * mm, "end": v(0, 1219.2) * mm});
            skLineSegment(sketch, "E510.right", {"start": v(457.2, 0) * mm, "end": v(457.2, 1219.2) * mm});
            skSolve(sketch);
        }
        {
            var Q0;
            Q0 = qSketchRegion(id + "F194", true);
            extrude(context, id + "F195", {"entities" : qUnion([Q0]), "oppositeDirection" : true, "depth" : 165.1 * mm, "offsetDistance" : 25.4 * mm});
        }
        {
            var Q0;
            Q0=makeQuery(id+"F195.opExtrude","CAP_FACE",FACE,{"disambiguationData":[OSD([sQuery(id+"F194.wireOp",EDGE,"E510.bottom"),sQuery(id+"F194.wireOp",EDGE,"E510.top"),sQuery(id+"F194.wireOp",EDGE,"E510.left"),sQuery(id+"F194.wireOp",EDGE,"E510.right")])],"isStart":true});
            var sketch = newSketch(context, id + "F196", { "sketchPlane" : qUnion([Q0])});
            skLineSegment(sketch, "E511.bottom", {"start": v(50.8, 1168.4) * mm, "end": v(406.4, 1168.4) * mm});
            skLineSegment(sketch, "E511.top", {"start": v(50.8, 635) * mm, "end": v(406.4, 635) * mm});
            skLineSegment(sketch, "E511.left", {"start": v(50.8, 1168.4) * mm, "end": v(50.8, 635) * mm});
            skLineSegment(sketch, "E511.right", {"start": v(406.4, 1168.4) * mm, "end": v(406.4, 635) * mm});
            skLineSegment(sketch, "E512.bottom", {"start": v(50.8, 584.2) * mm, "end": v(406.4, 584.2) * mm});
            skLineSegment(sketch, "E512.top", {"start": v(50.8, 50.8) * mm, "end": v(406.4, 50.8) * mm});
            skLineSegment(sketch, "E512.left", {"start": v(50.8, 584.2) * mm, "end": v(50.8, 50.8) * mm});
            skLineSegment(sketch, "E512.right", {"start": v(406.4, 584.2) * mm, "end": v(406.4, 50.8) * mm});
            skSolve(sketch);
        }
        {
            var Q0;
            Q0 = qSketchRegion(id + "F196", true);
            extrude(context, id + "F197", {"entities" : qUnion([Q0]), "operationType" : NewBodyOperationType.REMOVE, "oppositeDirection" : true, "depth" : 12.7 * mm, "offsetDistance" : 25.4 * mm});
        }
        {
            var Q0;
            Q0=makeQuery(id+"F195.opExtrude","CAP_FACE",FACE,{"disambiguationData":[OSD([sQuery(id+"F194.wireOp",EDGE,"E510.bottom"),sQuery(id+"F194.wireOp",EDGE,"E510.top"),sQuery(id+"F194.wireOp",EDGE,"E510.left"),sQuery(id+"F194.wireOp",EDGE,"E510.right")])],"isStart":false});
            var sketch = newSketch(context, id + "F198", { "sketchPlane" : qUnion([Q0])});
            skLineSegment(sketch, "E513.bottom", {"start": v(-438.15, 1200.15) * mm, "end": v(-19.05, 1200.15) * mm});
            skLineSegment(sketch, "E513.top", {"start": v(-438.15, 19.05) * mm, "end": v(-19.05, 19.05) * mm});
            skLineSegment(sketch, "E513.left", {"start": v(-438.15, 1200.15) * mm, "end": v(-438.15, 19.05) * mm});
            skLineSegment(sketch, "E513.right", {"start": v(-19.05, 1200.15) * mm, "end": v(-19.05, 19.05) * mm});
            skSolve(sketch);
        }
        {
            var Q0;
            Q0 = qSketchRegion(id + "F198", true);
            extrude(context, id + "F199", {"entities" : qUnion([Q0]), "operationType" : NewBodyOperationType.REMOVE, "oppositeDirection" : true, "depth" : 114.3 * mm, "offsetDistance" : 25.4 * mm});
        }
        {
            var Q0;
            Q0=makeQuery(id+"F199.boolean.opBoolean","COPY",FACE,{"derivedFrom":makeQuery(id+"F199.opExtrude","CAP_FACE",FACE,{"disambiguationData":[OSD([sQuery(id+"F198.wireOp",EDGE,"E513.bottom"),sQuery(id+"F198.wireOp",EDGE,"E513.top"),sQuery(id+"F198.wireOp",EDGE,"E513.left"),sQuery(id+"F198.wireOp",EDGE,"E513.right")])],"isStart":false})});
            var sketch = newSketch(context, id + "F200", { "sketchPlane" : qUnion([Q0])});
            skLineSegment(sketch, "E514.0.0", {"start": v(-50.8, 1168.4) * mm, "end": v(-50.8, 635) * mm});
            skLineSegment(sketch, "E514.0.1", {"start": v(-50.8, 635) * mm, "end": v(-406.4, 635) * mm});
            skLineSegment(sketch, "E514.0.2", {"start": v(-406.4, 635) * mm, "end": v(-406.4, 1168.4) * mm});
            skLineSegment(sketch, "E514.0.3", {"start": v(-406.4, 1168.4) * mm, "end": v(-50.8, 1168.4) * mm});
            skLineSegment(sketch, "E514.1.0", {"start": v(-50.8, 584.2) * mm, "end": v(-50.8, 50.8) * mm});
            skLineSegment(sketch, "E514.1.1", {"start": v(-50.8, 50.8) * mm, "end": v(-406.4, 50.8) * mm});
            skLineSegment(sketch, "E514.1.2", {"start": v(-406.4, 50.8) * mm, "end": v(-406.4, 584.2) * mm});
            skLineSegment(sketch, "E514.1.3", {"start": v(-406.4, 584.2) * mm, "end": v(-50.8, 584.2) * mm});
            skSolve(sketch);
        }
        {
            var Q0;
            Q0 = qSketchRegion(id + "F200", true);
            extrude(context, id + "F201", {"entities" : qUnion([Q0]), "operationType" : NewBodyOperationType.REMOVE, "oppositeDirection" : true, "depth" : 12.7 * mm, "offsetDistance" : 25.4 * mm});
        }
        {
            var Q0;
            Q0=qCreatedBy(id+"F175.planeOp",FACE);
            var sketch = newSketch(context, id + "F202", { "sketchPlane" : qUnion([Q0])});
            skLineSegment(sketch, "E515.bottom", {"start": v(0, 0) * mm, "end": v(762, 0) * mm});
            skLineSegment(sketch, "E515.top", {"start": v(0, 1371.6) * mm, "end": v(762, 1371.6) * mm});
            skLineSegment(sketch, "E515.left", {"start": v(0, 0) * mm, "end": v(0, 1371.6) * mm});
            skLineSegment(sketch, "E515.right", {"start": v(762, 0) * mm, "end": v(762, 1371.6) * mm});
            skSolve(sketch);
        }
        {
            var Q0;
            Q0 = qSketchRegion(id + "F202", true);
            extrude(context, id + "F203", {"entities" : qUnion([Q0]), "oppositeDirection" : true, "depth" : 165.1 * mm, "offsetDistance" : 25.4 * mm});
        }
        {
            var Q0;
            Q0=makeQuery(id+"F203.opExtrude","CAP_FACE",FACE,{"disambiguationData":[OSD([sQuery(id+"F202.wireOp",EDGE,"E515.bottom"),sQuery(id+"F202.wireOp",EDGE,"E515.top"),sQuery(id+"F202.wireOp",EDGE,"E515.left"),sQuery(id+"F202.wireOp",EDGE,"E515.right")])],"isStart":true});
            var sketch = newSketch(context, id + "F204", { "sketchPlane" : qUnion([Q0])});
            skLineSegment(sketch, "E516.bottom", {"start": v(50.8, 1320.8) * mm, "end": v(711.2, 1320.8) * mm});
            skLineSegment(sketch, "E516.top", {"start": v(50.8, 711.2) * mm, "end": v(711.2, 711.2) * mm});
            skLineSegment(sketch, "E516.left", {"start": v(50.8, 1320.8) * mm, "end": v(50.8, 711.2) * mm});
            skLineSegment(sketch, "E516.right", {"start": v(711.2, 1320.8) * mm, "end": v(711.2, 711.2) * mm});
            skLineSegment(sketch, "E517.bottom", {"start": v(50.8, 660.4) * mm, "end": v(711.2, 660.4) * mm});
            skLineSegment(sketch, "E517.top", {"start": v(50.8, 50.8) * mm, "end": v(711.2, 50.8) * mm});
            skLineSegment(sketch, "E517.left", {"start": v(50.8, 660.4) * mm, "end": v(50.8, 50.8) * mm});
            skLineSegment(sketch, "E517.right", {"start": v(711.2, 660.4) * mm, "end": v(711.2, 50.8) * mm});
            skSolve(sketch);
        }
        {
            var Q0;
            Q0 = qSketchRegion(id + "F204", true);
            extrude(context, id + "F205", {"entities" : qUnion([Q0]), "operationType" : NewBodyOperationType.REMOVE, "oppositeDirection" : true, "depth" : 12.7 * mm, "offsetDistance" : 25.4 * mm});
        }
        {
            var Q0;
            Q0=makeQuery(id+"F203.opExtrude","CAP_FACE",FACE,{"disambiguationData":[OSD([sQuery(id+"F202.wireOp",EDGE,"E515.bottom"),sQuery(id+"F202.wireOp",EDGE,"E515.top"),sQuery(id+"F202.wireOp",EDGE,"E515.left"),sQuery(id+"F202.wireOp",EDGE,"E515.right")])],"isStart":false});
            var sketch = newSketch(context, id + "F206", { "sketchPlane" : qUnion([Q0])});
            skLineSegment(sketch, "E518.bottom", {"start": v(-742.95, 1352.55) * mm, "end": v(-19.05, 1352.55) * mm});
            skLineSegment(sketch, "E518.top", {"start": v(-742.95, 19.05) * mm, "end": v(-19.05, 19.05) * mm});
            skLineSegment(sketch, "E518.left", {"start": v(-742.95, 1352.55) * mm, "end": v(-742.95, 19.05) * mm});
            skLineSegment(sketch, "E518.right", {"start": v(-19.05, 1352.55) * mm, "end": v(-19.05, 19.05) * mm});
            skSolve(sketch);
        }
        {
            var Q0;
            Q0 = qSketchRegion(id + "F206", true);
            extrude(context, id + "F207", {"entities" : qUnion([Q0]), "operationType" : NewBodyOperationType.REMOVE, "oppositeDirection" : true, "depth" : 114.3 * mm, "offsetDistance" : 25.4 * mm});
        }
        {
            var Q0;
            Q0=makeQuery(id+"F207.boolean.opBoolean","COPY",FACE,{"derivedFrom":makeQuery(id+"F207.opExtrude","CAP_FACE",FACE,{"disambiguationData":[OSD([sQuery(id+"F206.wireOp",EDGE,"E518.bottom"),sQuery(id+"F206.wireOp",EDGE,"E518.top"),sQuery(id+"F206.wireOp",EDGE,"E518.left"),sQuery(id+"F206.wireOp",EDGE,"E518.right")])],"isStart":false})});
            var sketch = newSketch(context, id + "F208", { "sketchPlane" : qUnion([Q0])});
            skLineSegment(sketch, "E519.0.0", {"start": v(-50.8, 1320.8) * mm, "end": v(-50.8, 711.2) * mm});
            skLineSegment(sketch, "E519.0.1", {"start": v(-50.8, 711.2) * mm, "end": v(-711.2, 711.2) * mm});
            skLineSegment(sketch, "E519.0.2", {"start": v(-711.2, 711.2) * mm, "end": v(-711.2, 1320.8) * mm});
            skLineSegment(sketch, "E519.0.3", {"start": v(-711.2, 1320.8) * mm, "end": v(-50.8, 1320.8) * mm});
            skLineSegment(sketch, "E519.1.0", {"start": v(-50.8, 660.4) * mm, "end": v(-50.8, 50.8) * mm});
            skLineSegment(sketch, "E519.1.1", {"start": v(-50.8, 50.8) * mm, "end": v(-711.2, 50.8) * mm});
            skLineSegment(sketch, "E519.1.2", {"start": v(-711.2, 50.8) * mm, "end": v(-711.2, 660.4) * mm});
            skLineSegment(sketch, "E519.1.3", {"start": v(-711.2, 660.4) * mm, "end": v(-50.8, 660.4) * mm});
            skSolve(sketch);
        }
        {
            var Q0;
            Q0 = qSketchRegion(id + "F208", true);
            extrude(context, id + "F209", {"entities" : qUnion([Q0]), "operationType" : NewBodyOperationType.REMOVE, "oppositeDirection" : true, "depth" : 12.7 * mm, "offsetDistance" : 25.4 * mm});
        }
        {
            var Q0;
            Q0=qCreatedBy(id+"F175.planeOp",FACE);
            cPlane(context, id + "F210", {"entities" : qUnion([Q0]), "cplaneType" : CPlaneType.OFFSET, "offset" : 2438.4 * mm, "oppositeDirection" : true, "width" : 152.4 * mm, "height" : 152.4 * mm});
        }
        {
            var Q0;
            Q0=qCreatedBy(id+"F210.planeOp",FACE);
            var sketch = newSketch(context, id + "F211", { "sketchPlane" : qUnion([Q0])});
            skLineSegment(sketch, "E520", {"start": v(3657.6, 0) * mm, "end": v(3657.6, 2095.5) * mm});
            skLineSegment(sketch, "E521", {"start": v(3657.6, 2095.5) * mm, "end": v(4318, 2095.5) * mm});
            skLineSegment(sketch, "E522", {"start": v(4318, 2095.5) * mm, "end": v(4318, 0) * mm});
            skLineSegment(sketch, "E523", {"start": v(4318, 0) * mm, "end": v(4292.6, 0) * mm});
            skLineSegment(sketch, "E524", {"start": v(4292.6, 0) * mm, "end": v(4292.6, 38.1) * mm});
            skLineSegment(sketch, "E525", {"start": v(4292.6, 38.1) * mm, "end": v(3683, 38.1) * mm});
            skLineSegment(sketch, "E526", {"start": v(3683, 38.1) * mm, "end": v(3683, 0) * mm});
            skLineSegment(sketch, "E527", {"start": v(3683, 0) * mm, "end": v(3657.6, 0) * mm});
            skSolve(sketch);
        }
        {
            var Q0;
            Q0 = qSketchRegion(id + "F211", true);
            extrude(context, id + "F212", {"entities" : qUnion([Q0]), "depth" : 114.3 * mm, "offsetDistance" : 25.4 * mm});
        }
        {
            var Q0;
            Q0=makeQuery(id+"F212.opExtrude","CAP_FACE",FACE,{"disambiguationData":[OSD([sQuery(id+"F211.wireOp",EDGE,"E520"),sQuery(id+"F211.wireOp",EDGE,"E521"),sQuery(id+"F211.wireOp",EDGE,"E522"),sQuery(id+"F211.wireOp",EDGE,"E523"),sQuery(id+"F211.wireOp",EDGE,"E524"),sQuery(id+"F211.wireOp",EDGE,"E525"),sQuery(id+"F211.wireOp",EDGE,"E526"),sQuery(id+"F211.wireOp",EDGE,"E527")])],"isStart":false});
            var sketch = newSketch(context, id + "F213", { "sketchPlane" : qUnion([Q0])});
            skLineSegment(sketch, "E528.bottom", {"start": v(3683, 38.1) * mm, "end": v(4292.6, 38.1) * mm});
            skLineSegment(sketch, "E528.top", {"start": v(3683, 2070.1) * mm, "end": v(4292.6, 2070.1) * mm});
            skLineSegment(sketch, "E528.left", {"start": v(3683, 38.1) * mm, "end": v(3683, 2070.1) * mm});
            skLineSegment(sketch, "E528.right", {"start": v(4292.6, 38.1) * mm, "end": v(4292.6, 2070.1) * mm});
            skSolve(sketch);
        }
        {
            var Q0;
            Q0 = qSketchRegion(id + "F213", true);
            extrude(context, id + "F214", {"entities" : qUnion([Q0]), "operationType" : NewBodyOperationType.REMOVE, "oppositeDirection" : true, "depth" : 79.38 * mm, "offsetDistance" : 25.4 * mm});
        }
        {
            var Q0;
            Q0=makeQuery(id+"F212.opExtrude","CAP_FACE",FACE,{"disambiguationData":[OSD([sQuery(id+"F211.wireOp",EDGE,"E520"),sQuery(id+"F211.wireOp",EDGE,"E521"),sQuery(id+"F211.wireOp",EDGE,"E522"),sQuery(id+"F211.wireOp",EDGE,"E523"),sQuery(id+"F211.wireOp",EDGE,"E524"),sQuery(id+"F211.wireOp",EDGE,"E525"),sQuery(id+"F211.wireOp",EDGE,"E526"),sQuery(id+"F211.wireOp",EDGE,"E527")])],"isStart":true});
            var sketch = newSketch(context, id + "F215", { "sketchPlane" : qUnion([Q0])});
            skLineSegment(sketch, "E529.0.0", {"start": v(-3683, 38.1) * mm, "end": v(-4292.6, 38.1) * mm});
            skLineSegment(sketch, "E529.0.1", {"start": v(-4292.6, 38.1) * mm, "end": v(-4292.6, 2070.1) * mm});
            skLineSegment(sketch, "E529.0.2", {"start": v(-4292.6, 2070.1) * mm, "end": v(-3683, 2070.1) * mm});
            skLineSegment(sketch, "E529.0.3", {"start": v(-3683, 2070.1) * mm, "end": v(-3683, 38.1) * mm});
            skSolve(sketch);
        }
        {
            var Q0;
            Q0 = qSketchRegion(id + "F215", true);
            extrude(context, id + "F216", {"entities" : qUnion([Q0]), "operationType" : NewBodyOperationType.REMOVE, "oppositeDirection" : true, "depth" : 1.59 * mm, "offsetDistance" : 25.4 * mm});
        }
        {
            var Q0;
            Q0=makeQuery(id+"F90.opExtrude","CAP_FACE",FACE,{"disambiguationData":[OSD([sQuery(id+"F89.wireOp",EDGE,"E175"),sQuery(id+"F89.wireOp",EDGE,"E176"),sQuery(id+"F89.wireOp",EDGE,"E177"),sQuery(id+"F89.wireOp",EDGE,"E178"),sQuery(id+"F89.wireOp",EDGE,"E179"),sQuery(id+"F89.wireOp",EDGE,"E180"),sQuery(id+"F89.wireOp",EDGE,"E181"),sQuery(id+"F89.wireOp",EDGE,"E182"),sQuery(id+"F89.wireOp",EDGE,"E183"),sQuery(id+"F89.wireOp",EDGE,"E184"),sQuery(id+"F89.wireOp",EDGE,"E185"),sQuery(id+"F89.wireOp",EDGE,"E186"),sQuery(id+"F89.wireOp",EDGE,"E187"),sQuery(id+"F89.wireOp",EDGE,"E188.0"),sQuery(id+"F89.wireOp",EDGE,"E189"),sQuery(id+"F89.wireOp",EDGE,"E190"),sQuery(id+"F89.wireOp",EDGE,"E191.trimOffspring"),sQuery(id+"F89.wireOp",EDGE,"E192.trimOffspring")])],"isStart":true});
            var sketch = newSketch(context, id + "F217", { "sketchPlane" : qUnion([Q0])});
            skLineSegment(sketch, "E530.bottom", {"start": v(3657.6, -21221.7) * mm, "end": v(3683, -21221.7) * mm});
            skLineSegment(sketch, "E530.top", {"start": v(3657.6, -21107.4) * mm, "end": v(3683, -21107.4) * mm});
            skLineSegment(sketch, "E530.left", {"start": v(3657.6, -21221.7) * mm, "end": v(3657.6, -21107.4) * mm});
            skLineSegment(sketch, "E530.right", {"start": v(3683, -21186.78) * mm, "end": v(3683, -21107.4) * mm});
            skLineSegment(sketch, "E531.bottom", {"start": v(4318, -21221.7) * mm, "end": v(4292.6, -21221.7) * mm});
            skLineSegment(sketch, "E531.top", {"start": v(4318, -21107.4) * mm, "end": v(4292.6, -21107.4) * mm});
            skLineSegment(sketch, "E531.left", {"start": v(4318, -21221.7) * mm, "end": v(4318, -21107.4) * mm});
            skLineSegment(sketch, "E531.right", {"start": v(4292.6, -21221.67) * mm, "end": v(4292.6, -21107.4) * mm});
            skLineSegment(sketch, "E532", {"start": v(4292.6, -21221.7) * mm, "end": v(3764.67, -21526.5) * mm});
            skLineSegment(sketch, "E533", {"start": v(3764.67, -21526.5) * mm, "end": v(3747.2, -21496.24) * mm});
            skLineSegment(sketch, "E534", {"start": v(3749.95, -21494.64) * mm, "end": v(4275.14, -21191.43) * mm});
            skLineSegment(sketch, "E535", {"start": v(4275.14, -21191.43) * mm, "end": v(4292.6, -21221.67) * mm});
            skArc(sketch, "E536", {"start": v(3683, -21221.7) * mm, "mid": v(3699.26, -21362.67) * mm, "end": v(3747.2, -21496.24) * mm});
            skArc(sketch, "E537.0", {"start": v(3686.18, -21221.7) * mm, "mid": v(3702.33, -21361.85) * mm, "end": v(3749.95, -21494.64) * mm});
            skLineSegment(sketch, "E538", {"start": v(3686.18, -21221.7) * mm, "end": v(3686.18, -21186.78) * mm});
            skLineSegment(sketch, "E539", {"start": v(3686.18, -21186.78) * mm, "end": v(3683, -21186.78) * mm});
            skSolve(sketch);
        }
        {
            var Q0;
            Q0 = qSketchRegion(id + "F217", true);
            extrude(context, id + "F218", {"entities" : qUnion([Q0]), "oppositeDirection" : true, "depth" : 25.4 * mm, "offsetDistance" : 25.4 * mm});
        }
        {
            var Q0;
            Q0=qCreatedBy(id+"F73.planeOp",FACE);
            var sketch = newSketch(context, id + "F219", { "sketchPlane" : qUnion([Q0])});
            skLineSegment(sketch, "E540.bottom", {"start": v(7315.2, 0) * mm, "end": v(7340.6, 0) * mm});
            skLineSegment(sketch, "E540.top", {"start": v(7315.2, 2095.5) * mm, "end": v(8991.6, 2095.5) * mm});
            skLineSegment(sketch, "E540.left", {"start": v(7315.2, 0) * mm, "end": v(7315.2, 2095.5) * mm});
            skLineSegment(sketch, "E540.right", {"start": v(8991.6, 0) * mm, "end": v(8991.6, 2095.5) * mm});
            skLineSegment(sketch, "E541", {"start": v(7340.6, 0) * mm, "end": v(7340.6, 38.1) * mm});
            skLineSegment(sketch, "E542", {"start": v(7340.6, 38.1) * mm, "end": v(8151.81, 38.1) * mm});
            skLineSegment(sketch, "E543", {"start": v(8966.2, 38.1) * mm, "end": v(8966.2, 0) * mm});
            skLineSegment(sketch, "E544.trimOffspring", {"start": v(8966.2, 0) * mm, "end": v(8991.6, 0) * mm});
            skLineSegment(sketch, "E545.top", {"start": v(8151.81, 2070.1) * mm, "end": v(8154.99, 2070.1) * mm});
            skLineSegment(sketch, "E545.left", {"start": v(8151.81, 38.1) * mm, "end": v(8151.81, 2070.1) * mm});
            skLineSegment(sketch, "E545.right", {"start": v(8154.99, 38.1) * mm, "end": v(8154.99, 2070.1) * mm});
            skLineSegment(sketch, "E546.trimOffspring", {"start": v(8154.99, 38.1) * mm, "end": v(8966.2, 38.1) * mm});
            skSolve(sketch);
        }
        {
            var Q0;
            Q0 = qSketchRegion(id + "F219", true);
            extrude(context, id + "F220", {"entities" : qUnion([Q0]), "oppositeDirection" : true, "depth" : 114.3 * mm, "offsetDistance" : 25.4 * mm});
        }
        {
            var Q0;
            Q0=makeQuery(id+"F220.opExtrude","CAP_FACE",FACE,{"disambiguationData":[OSD([sQuery(id+"F219.wireOp",EDGE,"E540.bottom"),sQuery(id+"F219.wireOp",EDGE,"E540.top"),sQuery(id+"F219.wireOp",EDGE,"E540.left"),sQuery(id+"F219.wireOp",EDGE,"E540.right"),sQuery(id+"F219.wireOp",EDGE,"E541"),sQuery(id+"F219.wireOp",EDGE,"E542"),sQuery(id+"F219.wireOp",EDGE,"E543"),sQuery(id+"F219.wireOp",EDGE,"E544.trimOffspring"),sQuery(id+"F219.wireOp",EDGE,"E545.top"),sQuery(id+"F219.wireOp",EDGE,"E545.left"),sQuery(id+"F219.wireOp",EDGE,"E545.right"),sQuery(id+"F219.wireOp",EDGE,"E546.trimOffspring")])],"isStart":true});
            var sketch = newSketch(context, id + "F221", { "sketchPlane" : qUnion([Q0])});
            skLineSegment(sketch, "E547.bottom", {"start": v(8151.81, 38.1) * mm, "end": v(7340.6, 38.1) * mm});
            skLineSegment(sketch, "E547.top", {"start": v(8151.81, 2070.1) * mm, "end": v(7340.6, 2070.1) * mm});
            skLineSegment(sketch, "E547.left", {"start": v(8151.81, 38.1) * mm, "end": v(8151.81, 2070.1) * mm});
            skLineSegment(sketch, "E547.right", {"start": v(7340.6, 38.1) * mm, "end": v(7340.6, 2070.1) * mm});
            skLineSegment(sketch, "E548.bottom", {"start": v(8154.99, 38.1) * mm, "end": v(8966.2, 38.1) * mm});
            skLineSegment(sketch, "E548.top", {"start": v(8154.99, 2070.1) * mm, "end": v(8966.2, 2070.1) * mm});
            skLineSegment(sketch, "E548.left", {"start": v(8154.99, 38.1) * mm, "end": v(8154.99, 2070.1) * mm});
            skLineSegment(sketch, "E548.right", {"start": v(8966.2, 38.1) * mm, "end": v(8966.2, 2070.1) * mm});
            skSolve(sketch);
        }
        {
            var Q0;
            Q0 = qSketchRegion(id + "F221", true);
            extrude(context, id + "F222", {"entities" : qUnion([Q0]), "operationType" : NewBodyOperationType.REMOVE, "oppositeDirection" : true, "depth" : 79.38 * mm, "offsetDistance" : 25.4 * mm});
        }
        {
            var Q0;
            Q0=makeQuery(id+"F220.opExtrude","CAP_FACE",FACE,{"disambiguationData":[OSD([sQuery(id+"F219.wireOp",EDGE,"E540.bottom"),sQuery(id+"F219.wireOp",EDGE,"E540.top"),sQuery(id+"F219.wireOp",EDGE,"E540.left"),sQuery(id+"F219.wireOp",EDGE,"E540.right"),sQuery(id+"F219.wireOp",EDGE,"E541"),sQuery(id+"F219.wireOp",EDGE,"E542"),sQuery(id+"F219.wireOp",EDGE,"E543"),sQuery(id+"F219.wireOp",EDGE,"E544.trimOffspring"),sQuery(id+"F219.wireOp",EDGE,"E545.top"),sQuery(id+"F219.wireOp",EDGE,"E545.left"),sQuery(id+"F219.wireOp",EDGE,"E545.right"),sQuery(id+"F219.wireOp",EDGE,"E546.trimOffspring")])],"isStart":false});
            var sketch = newSketch(context, id + "F223", { "sketchPlane" : qUnion([Q0])});
            skLineSegment(sketch, "E549.0.0", {"start": v(-7340.6, 2070.1) * mm, "end": v(-7340.6, 38.1) * mm});
            skLineSegment(sketch, "E549.0.1", {"start": v(-7340.6, 38.1) * mm, "end": v(-8151.81, 38.1) * mm});
            skLineSegment(sketch, "E549.0.2", {"start": v(-8151.81, 38.1) * mm, "end": v(-8151.81, 2070.1) * mm});
            skLineSegment(sketch, "E549.0.3", {"start": v(-8151.81, 2070.1) * mm, "end": v(-7340.6, 2070.1) * mm});
            skLineSegment(sketch, "E550.0.0", {"start": v(-8154.99, 38.1) * mm, "end": v(-8966.2, 38.1) * mm});
            skLineSegment(sketch, "E550.0.1", {"start": v(-8966.2, 38.1) * mm, "end": v(-8966.2, 2070.1) * mm});
            skLineSegment(sketch, "E550.0.2", {"start": v(-8966.2, 2070.1) * mm, "end": v(-8154.99, 2070.1) * mm});
            skLineSegment(sketch, "E550.0.3", {"start": v(-8154.99, 2070.1) * mm, "end": v(-8154.99, 38.1) * mm});
            skSolve(sketch);
        }
        {
            var Q0;
            Q0 = qSketchRegion(id + "F223", true);
            extrude(context, id + "F224", {"entities" : qUnion([Q0]), "operationType" : NewBodyOperationType.REMOVE, "oppositeDirection" : true, "depth" : 1.59 * mm, "offsetDistance" : 25.4 * mm});
        }
        {
            var Q0;
            Q0=makeQuery(id+"F224.boolean.opBoolean","COPY",FACE,{"derivedFrom":makeQuery(id+"F224.opExtrude","CAP_FACE",FACE,{"disambiguationData":[OSD([sQuery(id+"F223.wireOp",EDGE,"E549.0.0"),sQuery(id+"F223.wireOp",EDGE,"E549.0.1"),sQuery(id+"F223.wireOp",EDGE,"E549.0.2"),sQuery(id+"F223.wireOp",EDGE,"E549.0.3")])],"isStart":false})});
            var sketch = newSketch(context, id + "F225", { "sketchPlane" : qUnion([Q0])});
            skLineSegment(sketch, "E551.bottom", {"start": v(-8051.8, 1981.2) * mm, "end": v(-7759.7, 1981.2) * mm});
            skLineSegment(sketch, "E551.top", {"start": v(-8051.8, 1640.84) * mm, "end": v(-7759.7, 1640.84) * mm});
            skLineSegment(sketch, "E551.left", {"start": v(-8051.8, 1981.2) * mm, "end": v(-8051.8, 1640.84) * mm});
            skLineSegment(sketch, "E551.right", {"start": v(-7759.7, 1981.2) * mm, "end": v(-7759.7, 1640.84) * mm});
            skLineSegment(sketch, "E552.bottom", {"start": v(-7734.3, 1981.2) * mm, "end": v(-7442.2, 1981.2) * mm});
            skLineSegment(sketch, "E552.top", {"start": v(-7734.3, 1640.84) * mm, "end": v(-7442.2, 1640.84) * mm});
            skLineSegment(sketch, "E552.left", {"start": v(-7734.3, 1981.2) * mm, "end": v(-7734.3, 1640.84) * mm});
            skLineSegment(sketch, "E552.right", {"start": v(-7442.2, 1981.2) * mm, "end": v(-7442.2, 1640.84) * mm});
            skLineSegment(sketch, "E553.bottom", {"start": v(-7442.2, 1615.44) * mm, "end": v(-7734.3, 1615.44) * mm});
            skLineSegment(sketch, "E553.top", {"start": v(-7442.2, 1275.08) * mm, "end": v(-7734.3, 1275.08) * mm});
            skLineSegment(sketch, "E553.left", {"start": v(-7442.2, 1615.44) * mm, "end": v(-7442.2, 1275.08) * mm});
            skLineSegment(sketch, "E553.right", {"start": v(-7734.3, 1615.44) * mm, "end": v(-7734.3, 1275.08) * mm});
            skLineSegment(sketch, "E554.bottom", {"start": v(-7759.7, 1275.08) * mm, "end": v(-8051.8, 1275.08) * mm});
            skLineSegment(sketch, "E554.top", {"start": v(-7759.7, 1615.44) * mm, "end": v(-8051.8, 1615.44) * mm});
            skLineSegment(sketch, "E554.left", {"start": v(-7759.7, 1275.08) * mm, "end": v(-7759.7, 1615.44) * mm});
            skLineSegment(sketch, "E554.right", {"start": v(-8051.8, 1275.08) * mm, "end": v(-8051.8, 1615.44) * mm});
            skLineSegment(sketch, "E555.bottom", {"start": v(-8051.8, 1249.68) * mm, "end": v(-7759.7, 1249.68) * mm});
            skLineSegment(sketch, "E555.top", {"start": v(-8051.8, 909.32) * mm, "end": v(-7759.7, 909.32) * mm});
            skLineSegment(sketch, "E555.left", {"start": v(-8051.8, 1249.68) * mm, "end": v(-8051.8, 909.32) * mm});
            skLineSegment(sketch, "E555.right", {"start": v(-7759.7, 1249.68) * mm, "end": v(-7759.7, 909.32) * mm});
            skLineSegment(sketch, "E556.bottom", {"start": v(-7734.3, 1249.68) * mm, "end": v(-7442.2, 1249.68) * mm});
            skLineSegment(sketch, "E556.top", {"start": v(-7734.3, 909.32) * mm, "end": v(-7442.2, 909.32) * mm});
            skLineSegment(sketch, "E556.left", {"start": v(-7734.3, 1249.68) * mm, "end": v(-7734.3, 909.32) * mm});
            skLineSegment(sketch, "E556.right", {"start": v(-7442.2, 1249.68) * mm, "end": v(-7442.2, 909.32) * mm});
            skLineSegment(sketch, "E557.bottom", {"start": v(-7442.2, 883.92) * mm, "end": v(-7734.3, 883.92) * mm});
            skLineSegment(sketch, "E557.top", {"start": v(-7442.2, 543.56) * mm, "end": v(-7734.3, 543.56) * mm});
            skLineSegment(sketch, "E557.left", {"start": v(-7442.2, 883.92) * mm, "end": v(-7442.2, 543.56) * mm});
            skLineSegment(sketch, "E557.right", {"start": v(-7734.3, 883.92) * mm, "end": v(-7734.3, 543.56) * mm});
            skLineSegment(sketch, "E558.bottom", {"start": v(-7759.7, 543.56) * mm, "end": v(-8051.8, 543.56) * mm});
            skLineSegment(sketch, "E558.top", {"start": v(-7759.7, 883.92) * mm, "end": v(-8051.8, 883.92) * mm});
            skLineSegment(sketch, "E558.left", {"start": v(-7759.7, 543.56) * mm, "end": v(-7759.7, 883.92) * mm});
            skLineSegment(sketch, "E558.right", {"start": v(-8051.8, 543.56) * mm, "end": v(-8051.8, 883.92) * mm});
            skLineSegment(sketch, "E559.bottom", {"start": v(-8051.8, 518.16) * mm, "end": v(-7759.7, 518.16) * mm});
            skLineSegment(sketch, "E559.top", {"start": v(-8051.8, 177.8) * mm, "end": v(-7759.7, 177.8) * mm});
            skLineSegment(sketch, "E559.left", {"start": v(-8051.8, 518.16) * mm, "end": v(-8051.8, 177.8) * mm});
            skLineSegment(sketch, "E559.right", {"start": v(-7759.7, 518.16) * mm, "end": v(-7759.7, 177.8) * mm});
            skLineSegment(sketch, "E560.bottom", {"start": v(-7734.3, 177.8) * mm, "end": v(-7442.2, 177.8) * mm});
            skLineSegment(sketch, "E560.top", {"start": v(-7734.3, 518.16) * mm, "end": v(-7442.2, 518.16) * mm});
            skLineSegment(sketch, "E560.left", {"start": v(-7734.3, 177.8) * mm, "end": v(-7734.3, 518.16) * mm});
            skLineSegment(sketch, "E560.right", {"start": v(-7442.2, 177.8) * mm, "end": v(-7442.2, 518.16) * mm});
            skLineSegment(sketch, "E561.bottom", {"start": v(-8255, 1981.2) * mm, "end": v(-8547.1, 1981.2) * mm});
            skLineSegment(sketch, "E561.top", {"start": v(-8255, 1640.84) * mm, "end": v(-8547.1, 1640.84) * mm});
            skLineSegment(sketch, "E561.left", {"start": v(-8255, 1981.2) * mm, "end": v(-8255, 1640.84) * mm});
            skLineSegment(sketch, "E561.right", {"start": v(-8547.1, 1981.2) * mm, "end": v(-8547.1, 1640.84) * mm});
            skLineSegment(sketch, "E562.bottom", {"start": v(-8572.5, 1640.84) * mm, "end": v(-8864.6, 1640.84) * mm});
            skLineSegment(sketch, "E562.top", {"start": v(-8572.5, 1981.2) * mm, "end": v(-8864.6, 1981.2) * mm});
            skLineSegment(sketch, "E562.left", {"start": v(-8572.5, 1640.84) * mm, "end": v(-8572.5, 1981.2) * mm});
            skLineSegment(sketch, "E562.right", {"start": v(-8864.6, 1640.84) * mm, "end": v(-8864.6, 1981.2) * mm});
            skLineSegment(sketch, "E563.bottom", {"start": v(-8864.6, 1615.44) * mm, "end": v(-8572.5, 1615.44) * mm});
            skLineSegment(sketch, "E563.top", {"start": v(-8864.6, 1275.08) * mm, "end": v(-8572.5, 1275.08) * mm});
            skLineSegment(sketch, "E563.left", {"start": v(-8864.6, 1615.44) * mm, "end": v(-8864.6, 1275.08) * mm});
            skLineSegment(sketch, "E563.right", {"start": v(-8572.5, 1615.44) * mm, "end": v(-8572.5, 1275.08) * mm});
            skLineSegment(sketch, "E564.bottom", {"start": v(-8547.1, 1275.08) * mm, "end": v(-8255, 1275.08) * mm});
            skLineSegment(sketch, "E564.top", {"start": v(-8547.1, 1615.44) * mm, "end": v(-8255, 1615.44) * mm});
            skLineSegment(sketch, "E564.left", {"start": v(-8547.1, 1275.08) * mm, "end": v(-8547.1, 1615.44) * mm});
            skLineSegment(sketch, "E564.right", {"start": v(-8255, 1275.08) * mm, "end": v(-8255, 1615.44) * mm});
            skLineSegment(sketch, "E565.bottom", {"start": v(-8255, 1249.68) * mm, "end": v(-8547.1, 1249.68) * mm});
            skLineSegment(sketch, "E565.top", {"start": v(-8255, 909.32) * mm, "end": v(-8547.1, 909.32) * mm});
            skLineSegment(sketch, "E565.left", {"start": v(-8255, 1249.68) * mm, "end": v(-8255, 909.32) * mm});
            skLineSegment(sketch, "E565.right", {"start": v(-8547.1, 1249.68) * mm, "end": v(-8547.1, 909.32) * mm});
            skLineSegment(sketch, "E566.bottom", {"start": v(-8572.5, 909.32) * mm, "end": v(-8864.6, 909.32) * mm});
            skLineSegment(sketch, "E566.top", {"start": v(-8572.5, 1249.68) * mm, "end": v(-8864.6, 1249.68) * mm});
            skLineSegment(sketch, "E566.left", {"start": v(-8572.5, 909.32) * mm, "end": v(-8572.5, 1249.68) * mm});
            skLineSegment(sketch, "E566.right", {"start": v(-8864.6, 909.32) * mm, "end": v(-8864.6, 1249.68) * mm});
            skLineSegment(sketch, "E567.bottom", {"start": v(-8864.6, 883.92) * mm, "end": v(-8572.5, 883.92) * mm});
            skLineSegment(sketch, "E567.top", {"start": v(-8864.6, 543.56) * mm, "end": v(-8572.5, 543.56) * mm});
            skLineSegment(sketch, "E567.left", {"start": v(-8864.6, 883.92) * mm, "end": v(-8864.6, 543.56) * mm});
            skLineSegment(sketch, "E567.right", {"start": v(-8572.5, 883.92) * mm, "end": v(-8572.5, 543.56) * mm});
            skLineSegment(sketch, "E568.bottom", {"start": v(-8547.1, 543.56) * mm, "end": v(-8255, 543.56) * mm});
            skLineSegment(sketch, "E568.top", {"start": v(-8547.1, 883.92) * mm, "end": v(-8255, 883.92) * mm});
            skLineSegment(sketch, "E568.left", {"start": v(-8547.1, 543.56) * mm, "end": v(-8547.1, 883.92) * mm});
            skLineSegment(sketch, "E568.right", {"start": v(-8255, 543.56) * mm, "end": v(-8255, 883.92) * mm});
            skLineSegment(sketch, "E569.bottom", {"start": v(-8255, 518.16) * mm, "end": v(-8547.1, 518.16) * mm});
            skLineSegment(sketch, "E569.top", {"start": v(-8255, 177.8) * mm, "end": v(-8547.1, 177.8) * mm});
            skLineSegment(sketch, "E569.left", {"start": v(-8255, 518.16) * mm, "end": v(-8255, 177.8) * mm});
            skLineSegment(sketch, "E569.right", {"start": v(-8547.1, 518.16) * mm, "end": v(-8547.1, 177.8) * mm});
            skLineSegment(sketch, "E570.bottom", {"start": v(-8572.5, 177.8) * mm, "end": v(-8864.6, 177.8) * mm});
            skLineSegment(sketch, "E570.top", {"start": v(-8572.5, 518.16) * mm, "end": v(-8864.6, 518.16) * mm});
            skLineSegment(sketch, "E570.left", {"start": v(-8572.5, 177.8) * mm, "end": v(-8572.5, 518.16) * mm});
            skLineSegment(sketch, "E570.right", {"start": v(-8864.6, 177.8) * mm, "end": v(-8864.6, 518.16) * mm});
            skSolve(sketch);
        }
        {
            var Q0;
            Q0 = qSketchRegion(id + "F225", true);
            extrude(context, id + "F226", {"entities" : qUnion([Q0]), "operationType" : NewBodyOperationType.REMOVE, "oppositeDirection" : true, "depth" : 12.7 * mm, "offsetDistance" : 25.4 * mm});
        }
        {
            var Q0;
            Q0=makeQuery(id+"F222.boolean.opBoolean","COPY",FACE,{"derivedFrom":makeQuery(id+"F222.opExtrude","CAP_FACE",FACE,{"disambiguationData":[OSD([sQuery(id+"F221.wireOp",EDGE,"E547.bottom"),sQuery(id+"F221.wireOp",EDGE,"E547.top"),sQuery(id+"F221.wireOp",EDGE,"E547.left"),sQuery(id+"F221.wireOp",EDGE,"E547.right")])],"isStart":false})});
            var sketch = newSketch(context, id + "F227", { "sketchPlane" : qUnion([Q0])});
            skLineSegment(sketch, "E571.0.0", {"start": v(8572.5, 1640.84) * mm, "end": v(8572.5, 1981.2) * mm});
            skLineSegment(sketch, "E571.0.1", {"start": v(8572.5, 1981.2) * mm, "end": v(8864.6, 1981.2) * mm});
            skLineSegment(sketch, "E571.0.2", {"start": v(8864.6, 1981.2) * mm, "end": v(8864.6, 1640.84) * mm});
            skLineSegment(sketch, "E571.0.3", {"start": v(8864.6, 1640.84) * mm, "end": v(8572.5, 1640.84) * mm});
            skLineSegment(sketch, "E571.1.0", {"start": v(8547.1, 1640.84) * mm, "end": v(8255, 1640.84) * mm});
            skLineSegment(sketch, "E571.1.1", {"start": v(8255, 1640.84) * mm, "end": v(8255, 1981.2) * mm});
            skLineSegment(sketch, "E571.1.2", {"start": v(8255, 1981.2) * mm, "end": v(8547.1, 1981.2) * mm});
            skLineSegment(sketch, "E571.1.3", {"start": v(8547.1, 1981.2) * mm, "end": v(8547.1, 1640.84) * mm});
            skLineSegment(sketch, "E571.2.0", {"start": v(8864.6, 1615.44) * mm, "end": v(8864.6, 1275.08) * mm});
            skLineSegment(sketch, "E571.2.1", {"start": v(8864.6, 1275.08) * mm, "end": v(8572.5, 1275.08) * mm});
            skLineSegment(sketch, "E571.2.2", {"start": v(8572.5, 1275.08) * mm, "end": v(8572.5, 1615.44) * mm});
            skLineSegment(sketch, "E571.2.3", {"start": v(8572.5, 1615.44) * mm, "end": v(8864.6, 1615.44) * mm});
            skLineSegment(sketch, "E571.3.0", {"start": v(8255, 1615.44) * mm, "end": v(8547.1, 1615.44) * mm});
            skLineSegment(sketch, "E571.3.1", {"start": v(8547.1, 1615.44) * mm, "end": v(8547.1, 1275.08) * mm});
            skLineSegment(sketch, "E571.3.2", {"start": v(8547.1, 1275.08) * mm, "end": v(8255, 1275.08) * mm});
            skLineSegment(sketch, "E571.3.3", {"start": v(8255, 1275.08) * mm, "end": v(8255, 1615.44) * mm});
            skLineSegment(sketch, "E571.4.0", {"start": v(8572.5, 909.32) * mm, "end": v(8572.5, 1249.68) * mm});
            skLineSegment(sketch, "E571.4.1", {"start": v(8572.5, 1249.68) * mm, "end": v(8864.6, 1249.68) * mm});
            skLineSegment(sketch, "E571.4.2", {"start": v(8864.6, 1249.68) * mm, "end": v(8864.6, 909.32) * mm});
            skLineSegment(sketch, "E571.4.3", {"start": v(8864.6, 909.32) * mm, "end": v(8572.5, 909.32) * mm});
            skLineSegment(sketch, "E571.5.0", {"start": v(8547.1, 909.32) * mm, "end": v(8255, 909.32) * mm});
            skLineSegment(sketch, "E571.5.1", {"start": v(8255, 909.32) * mm, "end": v(8255, 1249.68) * mm});
            skLineSegment(sketch, "E571.5.2", {"start": v(8255, 1249.68) * mm, "end": v(8547.1, 1249.68) * mm});
            skLineSegment(sketch, "E571.5.3", {"start": v(8547.1, 1249.68) * mm, "end": v(8547.1, 909.32) * mm});
            skLineSegment(sketch, "E571.6.0", {"start": v(8864.6, 883.92) * mm, "end": v(8864.6, 543.56) * mm});
            skLineSegment(sketch, "E571.6.1", {"start": v(8864.6, 543.56) * mm, "end": v(8572.5, 543.56) * mm});
            skLineSegment(sketch, "E571.6.2", {"start": v(8572.5, 543.56) * mm, "end": v(8572.5, 883.92) * mm});
            skLineSegment(sketch, "E571.6.3", {"start": v(8572.5, 883.92) * mm, "end": v(8864.6, 883.92) * mm});
            skLineSegment(sketch, "E571.7.0", {"start": v(8255, 883.92) * mm, "end": v(8547.1, 883.92) * mm});
            skLineSegment(sketch, "E571.7.1", {"start": v(8547.1, 883.92) * mm, "end": v(8547.1, 543.56) * mm});
            skLineSegment(sketch, "E571.7.2", {"start": v(8547.1, 543.56) * mm, "end": v(8255, 543.56) * mm});
            skLineSegment(sketch, "E571.7.3", {"start": v(8255, 543.56) * mm, "end": v(8255, 883.92) * mm});
            skLineSegment(sketch, "E571.8.0", {"start": v(8572.5, 177.8) * mm, "end": v(8572.5, 518.16) * mm});
            skLineSegment(sketch, "E571.8.1", {"start": v(8572.5, 518.16) * mm, "end": v(8864.6, 518.16) * mm});
            skLineSegment(sketch, "E571.8.2", {"start": v(8864.6, 518.16) * mm, "end": v(8864.6, 177.8) * mm});
            skLineSegment(sketch, "E571.8.3", {"start": v(8864.6, 177.8) * mm, "end": v(8572.5, 177.8) * mm});
            skLineSegment(sketch, "E571.9.0", {"start": v(8547.1, 177.8) * mm, "end": v(8255, 177.8) * mm});
            skLineSegment(sketch, "E571.9.1", {"start": v(8255, 177.8) * mm, "end": v(8255, 518.16) * mm});
            skLineSegment(sketch, "E571.9.2", {"start": v(8255, 518.16) * mm, "end": v(8547.1, 518.16) * mm});
            skLineSegment(sketch, "E571.9.3", {"start": v(8547.1, 518.16) * mm, "end": v(8547.1, 177.8) * mm});
            skLineSegment(sketch, "E571.10.0", {"start": v(8051.8, 518.16) * mm, "end": v(8051.8, 177.8) * mm});
            skLineSegment(sketch, "E571.10.1", {"start": v(8051.8, 177.8) * mm, "end": v(7759.7, 177.8) * mm});
            skLineSegment(sketch, "E571.10.2", {"start": v(7759.7, 177.8) * mm, "end": v(7759.7, 518.16) * mm});
            skLineSegment(sketch, "E571.10.3", {"start": v(7759.7, 518.16) * mm, "end": v(8051.8, 518.16) * mm});
            skLineSegment(sketch, "E571.11.0", {"start": v(7442.2, 518.16) * mm, "end": v(7734.3, 518.16) * mm});
            skLineSegment(sketch, "E571.11.1", {"start": v(7734.3, 518.16) * mm, "end": v(7734.3, 177.8) * mm});
            skLineSegment(sketch, "E571.11.2", {"start": v(7734.3, 177.8) * mm, "end": v(7442.2, 177.8) * mm});
            skLineSegment(sketch, "E571.11.3", {"start": v(7442.2, 177.8) * mm, "end": v(7442.2, 518.16) * mm});
            skLineSegment(sketch, "E571.12.0", {"start": v(7734.3, 543.56) * mm, "end": v(7442.2, 543.56) * mm});
            skLineSegment(sketch, "E571.12.1", {"start": v(7442.2, 543.56) * mm, "end": v(7442.2, 883.92) * mm});
            skLineSegment(sketch, "E571.12.2", {"start": v(7442.2, 883.92) * mm, "end": v(7734.3, 883.92) * mm});
            skLineSegment(sketch, "E571.12.3", {"start": v(7734.3, 883.92) * mm, "end": v(7734.3, 543.56) * mm});
            skLineSegment(sketch, "E571.13.0", {"start": v(7759.7, 543.56) * mm, "end": v(7759.7, 883.92) * mm});
            skLineSegment(sketch, "E571.13.1", {"start": v(7759.7, 883.92) * mm, "end": v(8051.8, 883.92) * mm});
            skLineSegment(sketch, "E571.13.2", {"start": v(8051.8, 883.92) * mm, "end": v(8051.8, 543.56) * mm});
            skLineSegment(sketch, "E571.13.3", {"start": v(8051.8, 543.56) * mm, "end": v(7759.7, 543.56) * mm});
            skLineSegment(sketch, "E571.14.0", {"start": v(8051.8, 1249.68) * mm, "end": v(8051.8, 909.32) * mm});
            skLineSegment(sketch, "E571.14.1", {"start": v(8051.8, 909.32) * mm, "end": v(7759.7, 909.32) * mm});
            skLineSegment(sketch, "E571.14.2", {"start": v(7759.7, 909.32) * mm, "end": v(7759.7, 1249.68) * mm});
            skLineSegment(sketch, "E571.14.3", {"start": v(7759.7, 1249.68) * mm, "end": v(8051.8, 1249.68) * mm});
            skLineSegment(sketch, "E571.15.0", {"start": v(7734.3, 1249.68) * mm, "end": v(7734.3, 909.32) * mm});
            skLineSegment(sketch, "E571.15.1", {"start": v(7734.3, 909.32) * mm, "end": v(7442.2, 909.32) * mm});
            skLineSegment(sketch, "E571.15.2", {"start": v(7442.2, 909.32) * mm, "end": v(7442.2, 1249.68) * mm});
            skLineSegment(sketch, "E571.15.3", {"start": v(7442.2, 1249.68) * mm, "end": v(7734.3, 1249.68) * mm});
            skLineSegment(sketch, "E571.16.0", {"start": v(7734.3, 1275.08) * mm, "end": v(7442.2, 1275.08) * mm});
            skLineSegment(sketch, "E571.16.1", {"start": v(7442.2, 1275.08) * mm, "end": v(7442.2, 1615.44) * mm});
            skLineSegment(sketch, "E571.16.2", {"start": v(7442.2, 1615.44) * mm, "end": v(7734.3, 1615.44) * mm});
            skLineSegment(sketch, "E571.16.3", {"start": v(7734.3, 1615.44) * mm, "end": v(7734.3, 1275.08) * mm});
            skLineSegment(sketch, "E571.17.0", {"start": v(7759.7, 1275.08) * mm, "end": v(7759.7, 1615.44) * mm});
            skLineSegment(sketch, "E571.17.1", {"start": v(7759.7, 1615.44) * mm, "end": v(8051.8, 1615.44) * mm});
            skLineSegment(sketch, "E571.17.2", {"start": v(8051.8, 1615.44) * mm, "end": v(8051.8, 1275.08) * mm});
            skLineSegment(sketch, "E571.17.3", {"start": v(8051.8, 1275.08) * mm, "end": v(7759.7, 1275.08) * mm});
            skLineSegment(sketch, "E571.18.0", {"start": v(8051.8, 1981.2) * mm, "end": v(8051.8, 1640.84) * mm});
            skLineSegment(sketch, "E571.18.1", {"start": v(8051.8, 1640.84) * mm, "end": v(7759.7, 1640.84) * mm});
            skLineSegment(sketch, "E571.18.2", {"start": v(7759.7, 1640.84) * mm, "end": v(7759.7, 1981.2) * mm});
            skLineSegment(sketch, "E571.18.3", {"start": v(7759.7, 1981.2) * mm, "end": v(8051.8, 1981.2) * mm});
            skLineSegment(sketch, "E571.19.0", {"start": v(7734.3, 1981.2) * mm, "end": v(7734.3, 1640.84) * mm});
            skLineSegment(sketch, "E571.19.1", {"start": v(7734.3, 1640.84) * mm, "end": v(7442.2, 1640.84) * mm});
            skLineSegment(sketch, "E571.19.2", {"start": v(7442.2, 1640.84) * mm, "end": v(7442.2, 1981.2) * mm});
            skLineSegment(sketch, "E571.19.3", {"start": v(7442.2, 1981.2) * mm, "end": v(7734.3, 1981.2) * mm});
            skSolve(sketch);
        }
        {
            var Q0;
            Q0 = qSketchRegion(id + "F227", true);
            extrude(context, id + "F228", {"entities" : qUnion([Q0]), "operationType" : NewBodyOperationType.REMOVE, "oppositeDirection" : true, "depth" : 12.7 * mm, "offsetDistance" : 25.4 * mm});
        }
        {
            var Q0;
            Q0=qCreatedBy(makeId("Top.planeOp"),FACE);
            var sketch = newSketch(context, id + "F229", { "sketchPlane" : qUnion([Q0])});
            skLineSegment(sketch, "E572.bottom", {"start": v(7315.2, 9029.7) * mm, "end": v(7340.6, 9029.7) * mm});
            skLineSegment(sketch, "E572.top", {"start": v(7315.2, 9144) * mm, "end": v(7340.6, 9144) * mm});
            skLineSegment(sketch, "E572.left", {"start": v(7315.2, 9029.7) * mm, "end": v(7315.2, 9144) * mm});
            skLineSegment(sketch, "E572.right", {"start": v(7340.6, 9029.7) * mm, "end": v(7340.6, 9109.08) * mm});
            skLineSegment(sketch, "E573.bottom", {"start": v(8991.6, 9029.7) * mm, "end": v(8966.2, 9029.7) * mm});
            skLineSegment(sketch, "E573.top", {"start": v(8991.6, 9144) * mm, "end": v(8966.2, 9144) * mm});
            skLineSegment(sketch, "E573.left", {"start": v(8991.6, 9029.7) * mm, "end": v(8991.6, 9144) * mm});
            skLineSegment(sketch, "E573.right", {"start": v(8966.2, 9029.7) * mm, "end": v(8966.2, 9109.07) * mm});
            skLineSegment(sketch, "E574", {"start": v(8966.2, 9144) * mm, "end": v(8259.54, 9551.99) * mm});
            skLineSegment(sketch, "E575", {"start": v(8948.74, 9113.75) * mm, "end": v(8966.17, 9143.96) * mm});
            skLineSegment(sketch, "E576", {"start": v(7340.6, 9144) * mm, "end": v(8047.26, 9551.99) * mm});
            skLineSegment(sketch, "E577", {"start": v(7358.06, 9113.75) * mm, "end": v(7340.63, 9143.96) * mm});
            skLineSegment(sketch, "E578", {"start": v(7340.6, 9109.08) * mm, "end": v(7340.63, 9109.08) * mm});
            skLineSegment(sketch, "E579", {"start": v(7340.63, 9109.08) * mm, "end": v(7340.63, 9143.96) * mm});
            skLineSegment(sketch, "E580", {"start": v(8966.2, 9109.08) * mm, "end": v(8966.17, 9109.08) * mm});
            skLineSegment(sketch, "E581", {"start": v(8966.17, 9109.08) * mm, "end": v(8966.17, 9143.96) * mm});
            skArc(sketch, "E582", {"start": v(8047.26, 9551.99) * mm, "mid": v(8118.69, 9389.75) * mm, "end": v(8153.4, 9215.91) * mm});
            skArc(sketch, "E583", {"start": v(8259.54, 9551.99) * mm, "mid": v(8188.11, 9389.75) * mm, "end": v(8153.4, 9215.91) * mm});
            skArc(sketch, "E584.0", {"start": v(8061.32, 9519.78) * mm, "mid": v(8130.04, 9337.45) * mm, "end": v(8153.4, 9144) * mm});
            skArc(sketch, "E585.0", {"start": v(8245.48, 9519.78) * mm, "mid": v(8176.76, 9337.45) * mm, "end": v(8153.4, 9144) * mm});
            skLineSegment(sketch, "E586", {"start": v(7358.06, 9113.75) * mm, "end": v(8061.32, 9519.78) * mm});
            skLineSegment(sketch, "E587", {"start": v(8948.74, 9113.75) * mm, "end": v(8245.48, 9519.78) * mm});
            skSolve(sketch);
        }
        {
            var Q0;
            Q0 = qSketchRegion(id + "F229", true);
            extrude(context, id + "F230", {"entities" : qUnion([Q0]), "depth" : 25.4 * mm, "offsetDistance" : 25.4 * mm});
        }
        {
            var Q0;
            Q0=qCreatedBy(id+"F74.planeOp",FACE);
            var sketch = newSketch(context, id + "F231", { "sketchPlane" : qUnion([Q0])});
            skLineSegment(sketch, "E588", {"start": v(7315.2, 0) * mm, "end": v(7315.2, 2095.5) * mm});
            skLineSegment(sketch, "E589", {"start": v(7315.2, 2095.5) * mm, "end": v(7950.2, 2095.5) * mm});
            skLineSegment(sketch, "E590", {"start": v(7950.2, 2095.5) * mm, "end": v(7950.2, 0) * mm});
            skLineSegment(sketch, "E591", {"start": v(7950.2, 0) * mm, "end": v(7937.5, 0) * mm});
            skLineSegment(sketch, "E592", {"start": v(7937.5, 0) * mm, "end": v(7937.5, 38.1) * mm});
            skLineSegment(sketch, "E593", {"start": v(7937.5, 38.1) * mm, "end": v(7632.76, 38.1) * mm});
            skLineSegment(sketch, "E594", {"start": v(7327.9, 38.1) * mm, "end": v(7327.9, 0) * mm});
            skLineSegment(sketch, "E595", {"start": v(7327.9, 0) * mm, "end": v(7315.2, 0) * mm});
            skLineSegment(sketch, "E596", {"start": v(7632.64, 38.1) * mm, "end": v(7632.64, 2070.1) * mm});
            skLineSegment(sketch, "E597", {"start": v(7632.64, 2070.1) * mm, "end": v(7632.76, 2070.1) * mm});
            skLineSegment(sketch, "E598", {"start": v(7632.76, 2070.1) * mm, "end": v(7632.76, 38.1) * mm});
            skLineSegment(sketch, "E599.trimOffspring", {"start": v(7632.64, 38.1) * mm, "end": v(7327.9, 38.1) * mm});
            skSolve(sketch);
        }
        {
            var Q0;
            Q0 = qSketchRegion(id + "F231", true);
            extrude(context, id + "F232", {"entities" : qUnion([Q0]), "oppositeDirection" : true, "depth" : 114.3 * mm, "offsetDistance" : 25.4 * mm});
        }
        {
            var Q0;
            Q0=makeQuery(id+"F232.opExtrude","CAP_FACE",FACE,{"disambiguationData":[OSD([sQuery(id+"F231.wireOp",EDGE,"E588"),sQuery(id+"F231.wireOp",EDGE,"E589"),sQuery(id+"F231.wireOp",EDGE,"E590"),sQuery(id+"F231.wireOp",EDGE,"E591"),sQuery(id+"F231.wireOp",EDGE,"E592"),sQuery(id+"F231.wireOp",EDGE,"E593"),sQuery(id+"F231.wireOp",EDGE,"E594"),sQuery(id+"F231.wireOp",EDGE,"E595"),sQuery(id+"F231.wireOp",EDGE,"E596"),sQuery(id+"F231.wireOp",EDGE,"E597"),sQuery(id+"F231.wireOp",EDGE,"E598"),sQuery(id+"F231.wireOp",EDGE,"E599.trimOffspring")])],"isStart":true});
            var sketch = newSketch(context, id + "F233", { "sketchPlane" : qUnion([Q0])});
            skLineSegment(sketch, "E600.bottom", {"start": v(7327.9, 38.1) * mm, "end": v(7937.5, 38.1) * mm});
            skLineSegment(sketch, "E600.top", {"start": v(7327.9, 2070.1) * mm, "end": v(7937.5, 2070.1) * mm});
            skLineSegment(sketch, "E600.left", {"start": v(7327.9, 38.1) * mm, "end": v(7327.9, 2070.1) * mm});
            skLineSegment(sketch, "E600.right", {"start": v(7937.5, 38.1) * mm, "end": v(7937.5, 2070.1) * mm});
            skSolve(sketch);
        }
        {
            var Q0;
            Q0 = qSketchRegion(id + "F233", true);
            extrude(context, id + "F234", {"entities" : qUnion([Q0]), "operationType" : NewBodyOperationType.REMOVE, "oppositeDirection" : true, "depth" : 25.4 * mm, "offsetDistance" : 25.4 * mm});
        }
        {
            var Q0;
            Q0=makeQuery(id+"F232.opExtrude","CAP_FACE",FACE,{"disambiguationData":[OSD([sQuery(id+"F231.wireOp",EDGE,"E588"),sQuery(id+"F231.wireOp",EDGE,"E589"),sQuery(id+"F231.wireOp",EDGE,"E590"),sQuery(id+"F231.wireOp",EDGE,"E591"),sQuery(id+"F231.wireOp",EDGE,"E592"),sQuery(id+"F231.wireOp",EDGE,"E593"),sQuery(id+"F231.wireOp",EDGE,"E594"),sQuery(id+"F231.wireOp",EDGE,"E595"),sQuery(id+"F231.wireOp",EDGE,"E596"),sQuery(id+"F231.wireOp",EDGE,"E597"),sQuery(id+"F231.wireOp",EDGE,"E598"),sQuery(id+"F231.wireOp",EDGE,"E599.trimOffspring")])],"isStart":false});
            var sketch = newSketch(context, id + "F235", { "sketchPlane" : qUnion([Q0])});
            skLineSegment(sketch, "E601.bottom", {"start": v(-7937.5, 38.1) * mm, "end": v(-7327.9, 38.1) * mm});
            skLineSegment(sketch, "E601.top", {"start": v(-7937.5, 2070.1) * mm, "end": v(-7327.9, 2070.1) * mm});
            skLineSegment(sketch, "E601.left", {"start": v(-7937.5, 38.1) * mm, "end": v(-7937.5, 2070.1) * mm});
            skLineSegment(sketch, "E601.right", {"start": v(-7327.9, 38.1) * mm, "end": v(-7327.9, 2070.1) * mm});
            skSolve(sketch);
        }
        {
            var Q0;
            Q0 = qSketchRegion(id + "F235", true);
            extrude(context, id + "F236", {"entities" : qUnion([Q0]), "operationType" : NewBodyOperationType.REMOVE, "oppositeDirection" : true, "depth" : 57.15 * mm, "offsetDistance" : 25.4 * mm});
        }
        {
            var Q0;
            Q0=qCreatedBy(makeId("Top.planeOp"),FACE);
            var sketch = newSketch(context, id + "F237", { "sketchPlane" : qUnion([Q0])});
            skLineSegment(sketch, "E602", {"start": v(7950.2, 11468.1) * mm, "end": v(7950.2, 11582.4) * mm});
            skLineSegment(sketch, "E603", {"start": v(7950.2, 11582.4) * mm, "end": v(7937.5, 11582.4) * mm});
            skLineSegment(sketch, "E604", {"start": v(7937.5, 11582.4) * mm, "end": v(7937.5, 11525.25) * mm});
            skLineSegment(sketch, "E605", {"start": v(7937.5, 11525.25) * mm, "end": v(7327.9, 11525.25) * mm, "construction": true});
            skLineSegment(sketch, "E606", {"start": v(7327.9, 11525.25) * mm, "end": v(7327.9, 11582.4) * mm});
            skLineSegment(sketch, "E607", {"start": v(7327.9, 11582.4) * mm, "end": v(7315.2, 11582.4) * mm});
            skLineSegment(sketch, "E608", {"start": v(7315.2, 11582.4) * mm, "end": v(7315.2, 11468.1) * mm});
            skLineSegment(sketch, "E609", {"start": v(7315.2, 11468.1) * mm, "end": v(7327.9, 11468.1) * mm});
            skLineSegment(sketch, "E610", {"start": v(7327.9, 11468.1) * mm, "end": v(7327.9, 11493.5) * mm});
            skLineSegment(sketch, "E611", {"start": v(7327.9, 11493.5) * mm, "end": v(7346.77, 11493.5) * mm});
            skLineSegment(sketch, "E612", {"start": v(7937.5, 11468.1) * mm, "end": v(7950.2, 11468.1) * mm});
            skLineSegment(sketch, "E613", {"start": v(7937.5, 11525.25) * mm, "end": v(7937.5, 11493.53) * mm});
            skLineSegment(sketch, "E614", {"start": v(7327.9, 11525.25) * mm, "end": v(7327.9, 11493.53) * mm});
            skLineSegment(sketch, "E615", {"start": v(7327.9, 11509.37) * mm, "end": v(7937.5, 11509.37) * mm, "construction": true});
            skLineSegment(sketch, "E616.trimOffspring", {"start": v(7937.5, 11493.53) * mm, "end": v(7681.54, 11493.53) * mm});
            skLineSegment(sketch, "E617", {"start": v(7361.75, 11531.06) * mm, "end": v(7334.25, 11515.19) * mm});
            skLineSegment(sketch, "E618", {"start": v(7334.25, 11515.19) * mm, "end": v(7346.76, 11493.53) * mm});
            skLineSegment(sketch, "E619", {"start": v(7486.65, 11251.22) * mm, "end": v(7512.77, 11266.3) * mm});
            skLineSegment(sketch, "E620", {"start": v(7513.35, 11268.47) * mm, "end": v(7383.43, 11493.5) * mm});
            skLineSegment(sketch, "E621", {"start": v(7514.94, 11268.47) * mm, "end": v(7644.86, 11493.5) * mm});
            skLineSegment(sketch, "E622", {"start": v(7666.55, 11531.06) * mm, "end": v(7694.04, 11515.19) * mm});
            skLineSegment(sketch, "E623", {"start": v(7694.04, 11515.19) * mm, "end": v(7681.54, 11493.53) * mm});
            skLineSegment(sketch, "E624", {"start": v(7541.64, 11251.22) * mm, "end": v(7515.52, 11266.3) * mm});
            skLineSegment(sketch, "E625.trimOffspring", {"start": v(7681.52, 11493.5) * mm, "end": v(7541.64, 11251.22) * mm});
            skLineSegment(sketch, "E626.trimOffspring", {"start": v(7644.88, 11493.53) * mm, "end": v(7383.42, 11493.53) * mm});
            skLineSegment(sketch, "E627.trimOffspring", {"start": v(7681.52, 11493.5) * mm, "end": v(7937.5, 11493.5) * mm});
            skLineSegment(sketch, "E628.trimOffspring", {"start": v(7644.88, 11493.53) * mm, "end": v(7666.55, 11531.06) * mm});
            skLineSegment(sketch, "E629.trimOffspring", {"start": v(7383.42, 11493.53) * mm, "end": v(7361.75, 11531.06) * mm});
            skLineSegment(sketch, "E630.trimOffspring", {"start": v(7346.76, 11493.53) * mm, "end": v(7327.9, 11493.53) * mm});
            skLineSegment(sketch, "E631.trimOffspring", {"start": v(7383.43, 11493.5) * mm, "end": v(7644.86, 11493.5) * mm});
            skLineSegment(sketch, "E632.trimOffspring", {"start": v(7346.77, 11493.5) * mm, "end": v(7486.65, 11251.22) * mm});
            skArc(sketch, "E633", {"start": v(7514.94, 11268.47) * mm, "mid": v(7514.15, 11268.68) * mm, "end": v(7513.35, 11268.47) * mm});
            skArc(sketch, "E634.trimOffspring", {"start": v(7512.77, 11266.3) * mm, "mid": v(7514.15, 11265.5) * mm, "end": v(7515.52, 11266.3) * mm});
            skLineSegment(sketch, "E635", {"start": v(7348, 11523.12) * mm, "end": v(7355.94, 11509.37) * mm, "construction": true});
            skLineSegment(sketch, "E636.trimOffspring", {"start": v(7937.5, 11493.5) * mm, "end": v(7937.5, 11468.1) * mm});
            skSolve(sketch);
        }
        {
            var Q0;
            Q0 = qSketchRegion(id + "F237", true);
            extrude(context, id + "F238", {"entities" : qUnion([Q0]), "depth" : 25.4 * mm, "offsetDistance" : 25.4 * mm});
        }
        {
            var Q0;
            Q0=qCreatedBy(id+"F91.planeOp",FACE);
            var sketch = newSketch(context, id + "F239", { "sketchPlane" : qUnion([Q0])});
            skLineSegment(sketch, "E637", {"start": v(7315.2, 0) * mm, "end": v(7315.2, 2076.45) * mm});
            skLineSegment(sketch, "E638", {"start": v(7315.2, 2076.45) * mm, "end": v(8102.6, 2076.45) * mm});
            skLineSegment(sketch, "E639", {"start": v(8102.6, 2076.45) * mm, "end": v(8102.6, 0) * mm});
            skLineSegment(sketch, "E640", {"start": v(8102.6, 0) * mm, "end": v(8089.9, 0) * mm});
            skLineSegment(sketch, "E641", {"start": v(8089.9, 0) * mm, "end": v(8089.9, 31.75) * mm});
            skLineSegment(sketch, "E642", {"start": v(8089.9, 31.75) * mm, "end": v(7708.96, 31.75) * mm});
            skLineSegment(sketch, "E643", {"start": v(7708.96, 31.75) * mm, "end": v(7708.96, 2063.75) * mm});
            skLineSegment(sketch, "E644", {"start": v(7708.96, 2063.75) * mm, "end": v(7708.84, 2063.75) * mm});
            skLineSegment(sketch, "E645", {"start": v(7708.84, 2063.75) * mm, "end": v(7708.84, 31.75) * mm});
            skLineSegment(sketch, "E646", {"start": v(7708.84, 31.75) * mm, "end": v(7327.9, 31.75) * mm});
            skLineSegment(sketch, "E647", {"start": v(7327.9, 31.75) * mm, "end": v(7327.9, 0) * mm});
            skLineSegment(sketch, "E648", {"start": v(7327.9, 0) * mm, "end": v(7315.2, 0) * mm});
            skSolve(sketch);
        }
        {
            var Q0;
            Q0 = qSketchRegion(id + "F239", true);
            extrude(context, id + "F240", {"entities" : qUnion([Q0]), "oppositeDirection" : true, "depth" : 114.3 * mm, "offsetDistance" : 25.4 * mm});
        }
        {
            var Q0;
            Q0=makeQuery(id+"F240.opExtrude","CAP_FACE",FACE,{"disambiguationData":[OSD([sQuery(id+"F239.wireOp",EDGE,"E637"),sQuery(id+"F239.wireOp",EDGE,"E638"),sQuery(id+"F239.wireOp",EDGE,"E639"),sQuery(id+"F239.wireOp",EDGE,"E640"),sQuery(id+"F239.wireOp",EDGE,"E641"),sQuery(id+"F239.wireOp",EDGE,"E642"),sQuery(id+"F239.wireOp",EDGE,"E643"),sQuery(id+"F239.wireOp",EDGE,"E644"),sQuery(id+"F239.wireOp",EDGE,"E645"),sQuery(id+"F239.wireOp",EDGE,"E646"),sQuery(id+"F239.wireOp",EDGE,"E647"),sQuery(id+"F239.wireOp",EDGE,"E648")])],"isStart":true});
            var sketch = newSketch(context, id + "F241", { "sketchPlane" : qUnion([Q0])});
            skLineSegment(sketch, "E649.bottom", {"start": v(7327.9, 31.75) * mm, "end": v(8089.9, 31.75) * mm});
            skLineSegment(sketch, "E649.top", {"start": v(7327.9, 2063.75) * mm, "end": v(8089.9, 2063.75) * mm});
            skLineSegment(sketch, "E649.left", {"start": v(7327.9, 31.75) * mm, "end": v(7327.9, 2063.75) * mm});
            skLineSegment(sketch, "E649.right", {"start": v(8089.9, 31.75) * mm, "end": v(8089.9, 2063.75) * mm});
            skSolve(sketch);
        }
        {
            var Q0;
            Q0 = qSketchRegion(id + "F241", true);
            extrude(context, id + "F242", {"entities" : qUnion([Q0]), "operationType" : NewBodyOperationType.REMOVE, "oppositeDirection" : true, "depth" : 25.4 * mm, "offsetDistance" : 25.4 * mm});
        }
        {
            var Q0;
            Q0=makeQuery(id+"F240.opExtrude","CAP_FACE",FACE,{"disambiguationData":[OSD([sQuery(id+"F239.wireOp",EDGE,"E637"),sQuery(id+"F239.wireOp",EDGE,"E638"),sQuery(id+"F239.wireOp",EDGE,"E639"),sQuery(id+"F239.wireOp",EDGE,"E640"),sQuery(id+"F239.wireOp",EDGE,"E641"),sQuery(id+"F239.wireOp",EDGE,"E642"),sQuery(id+"F239.wireOp",EDGE,"E643"),sQuery(id+"F239.wireOp",EDGE,"E644"),sQuery(id+"F239.wireOp",EDGE,"E645"),sQuery(id+"F239.wireOp",EDGE,"E646"),sQuery(id+"F239.wireOp",EDGE,"E647"),sQuery(id+"F239.wireOp",EDGE,"E648")])],"isStart":false});
            var sketch = newSketch(context, id + "F243", { "sketchPlane" : qUnion([Q0])});
            skLineSegment(sketch, "E650.bottom", {"start": v(-7327.9, 31.75) * mm, "end": v(-8089.9, 31.75) * mm});
            skLineSegment(sketch, "E650.top", {"start": v(-7327.9, 2063.75) * mm, "end": v(-8089.9, 2063.75) * mm});
            skLineSegment(sketch, "E650.left", {"start": v(-7327.9, 31.75) * mm, "end": v(-7327.9, 2063.75) * mm});
            skLineSegment(sketch, "E650.right", {"start": v(-8089.9, 31.75) * mm, "end": v(-8089.9, 2063.75) * mm});
            skSolve(sketch);
        }
        {
            var Q0;
            Q0 = qSketchRegion(id + "F243", true);
            extrude(context, id + "F244", {"entities" : qUnion([Q0]), "operationType" : NewBodyOperationType.REMOVE, "oppositeDirection" : true, "depth" : 57.15 * mm, "offsetDistance" : 25.4 * mm});
        }
        {
            var Q0;
            Q0=qCreatedBy(makeId("Top.planeOp"),FACE);
            var sketch = newSketch(context, id + "F245", { "sketchPlane" : qUnion([Q0])});
            skLineSegment(sketch, "E651", {"start": v(8102.6, 13906.5) * mm, "end": v(8102.6, 14020.8) * mm});
            skLineSegment(sketch, "E652", {"start": v(8102.6, 14020.8) * mm, "end": v(8089.9, 14020.8) * mm});
            skLineSegment(sketch, "E653", {"start": v(8089.9, 14020.8) * mm, "end": v(8089.9, 13963.65) * mm});
            skLineSegment(sketch, "E654", {"start": v(8089.9, 13963.65) * mm, "end": v(7327.9, 13963.65) * mm, "construction": true});
            skLineSegment(sketch, "E655", {"start": v(7327.9, 13963.65) * mm, "end": v(7327.9, 14020.8) * mm});
            skLineSegment(sketch, "E656", {"start": v(7327.9, 14020.8) * mm, "end": v(7315.2, 14020.8) * mm});
            skLineSegment(sketch, "E657", {"start": v(7315.2, 14020.8) * mm, "end": v(7315.2, 13906.5) * mm});
            skLineSegment(sketch, "E658", {"start": v(7315.2, 13906.5) * mm, "end": v(7327.9, 13906.5) * mm});
            skLineSegment(sketch, "E659", {"start": v(7327.9, 13906.5) * mm, "end": v(7327.9, 13931.9) * mm});
            skLineSegment(sketch, "E660", {"start": v(7327.9, 13931.9) * mm, "end": v(7346.77, 13931.9) * mm});
            skLineSegment(sketch, "E661", {"start": v(8089.9, 13906.5) * mm, "end": v(8102.6, 13906.5) * mm});
            skLineSegment(sketch, "E662", {"start": v(8089.9, 13963.65) * mm, "end": v(8089.9, 13931.93) * mm});
            skLineSegment(sketch, "E663", {"start": v(7327.9, 13963.65) * mm, "end": v(7327.9, 13931.93) * mm});
            skLineSegment(sketch, "E664", {"start": v(7327.9, 13947.77) * mm, "end": v(8089.9, 13947.77) * mm, "construction": true});
            skLineSegment(sketch, "E665.trimOffspring", {"start": v(8089.9, 13931.93) * mm, "end": v(7757.74, 13931.93) * mm});
            skLineSegment(sketch, "E666", {"start": v(7361.75, 13969.46) * mm, "end": v(7334.25, 13953.59) * mm});
            skLineSegment(sketch, "E667", {"start": v(7334.25, 13953.59) * mm, "end": v(7346.76, 13931.93) * mm});
            skLineSegment(sketch, "E668", {"start": v(7524.75, 13623.63) * mm, "end": v(7550.87, 13638.71) * mm});
            skLineSegment(sketch, "E669", {"start": v(7551.45, 13640.88) * mm, "end": v(7383.43, 13931.9) * mm});
            skLineSegment(sketch, "E670", {"start": v(7553.04, 13640.88) * mm, "end": v(7721.06, 13931.9) * mm});
            skLineSegment(sketch, "E671", {"start": v(7742.75, 13969.46) * mm, "end": v(7770.24, 13953.59) * mm});
            skLineSegment(sketch, "E672", {"start": v(7770.24, 13953.59) * mm, "end": v(7757.74, 13931.93) * mm});
            skLineSegment(sketch, "E673", {"start": v(7579.74, 13623.63) * mm, "end": v(7553.62, 13638.71) * mm});
            skLineSegment(sketch, "E674.trimOffspring", {"start": v(7757.72, 13931.9) * mm, "end": v(7579.74, 13623.63) * mm});
            skLineSegment(sketch, "E675.trimOffspring", {"start": v(7721.08, 13931.93) * mm, "end": v(7383.42, 13931.93) * mm});
            skLineSegment(sketch, "E676.trimOffspring", {"start": v(7757.72, 13931.9) * mm, "end": v(8089.9, 13931.9) * mm});
            skLineSegment(sketch, "E677.trimOffspring", {"start": v(7721.08, 13931.93) * mm, "end": v(7742.75, 13969.46) * mm});
            skLineSegment(sketch, "E678.trimOffspring", {"start": v(7383.42, 13931.93) * mm, "end": v(7361.75, 13969.46) * mm});
            skLineSegment(sketch, "E679.trimOffspring", {"start": v(7346.76, 13931.93) * mm, "end": v(7327.9, 13931.93) * mm});
            skLineSegment(sketch, "E680.trimOffspring", {"start": v(7383.43, 13931.9) * mm, "end": v(7721.06, 13931.9) * mm});
            skLineSegment(sketch, "E681.trimOffspring", {"start": v(7346.77, 13931.9) * mm, "end": v(7524.75, 13623.63) * mm});
            skArc(sketch, "E682", {"start": v(7553.04, 13640.88) * mm, "mid": v(7552.25, 13641.1) * mm, "end": v(7551.45, 13640.88) * mm});
            skArc(sketch, "E683.trimOffspring", {"start": v(7550.87, 13638.71) * mm, "mid": v(7552.25, 13637.92) * mm, "end": v(7553.62, 13638.71) * mm});
            skLineSegment(sketch, "E684", {"start": v(7348, 13961.52) * mm, "end": v(7355.94, 13947.77) * mm, "construction": true});
            skLineSegment(sketch, "E685.trimOffspring", {"start": v(8089.9, 13931.9) * mm, "end": v(8089.9, 13906.5) * mm});
            skSolve(sketch);
        }
        {
            var Q0;
            Q0 = qSketchRegion(id + "F245", true);
            extrude(context, id + "F246", {"entities" : qUnion([Q0]), "depth" : 25.4 * mm, "offsetDistance" : 25.4 * mm});
        }
        {
            var Q0;
            Q0=qCreatedBy(id+"F164.planeOp",FACE);
            var sketch = newSketch(context, id + "F247", { "sketchPlane" : qUnion([Q0])});
            skLineSegment(sketch, "E686", {"start": v(7315.2, 0) * mm, "end": v(7315.2, 2076.45) * mm});
            skLineSegment(sketch, "E687", {"start": v(7315.2, 2076.45) * mm, "end": v(8255, 2076.45) * mm});
            skLineSegment(sketch, "E688", {"start": v(8255, 2076.45) * mm, "end": v(8255, 0) * mm});
            skLineSegment(sketch, "E689", {"start": v(8255, 0) * mm, "end": v(8242.3, 0) * mm});
            skLineSegment(sketch, "E690", {"start": v(8242.3, 0) * mm, "end": v(8242.3, 25.4) * mm});
            skLineSegment(sketch, "E691", {"start": v(8242.3, 25.4) * mm, "end": v(7785.16, 25.4) * mm});
            skLineSegment(sketch, "E692", {"start": v(7785.16, 25.4) * mm, "end": v(7785.16, 2057.4) * mm});
            skLineSegment(sketch, "E693", {"start": v(7785.16, 2057.4) * mm, "end": v(7785.04, 2057.4) * mm});
            skLineSegment(sketch, "E694", {"start": v(7785.04, 2057.4) * mm, "end": v(7785.04, 25.4) * mm});
            skLineSegment(sketch, "E695", {"start": v(7785.04, 25.4) * mm, "end": v(7327.9, 25.4) * mm});
            skLineSegment(sketch, "E696", {"start": v(7327.9, 25.4) * mm, "end": v(7327.9, 0) * mm});
            skLineSegment(sketch, "E697", {"start": v(7327.9, 0) * mm, "end": v(7315.2, 0) * mm});
            skSolve(sketch);
        }
        {
            var Q0;
            Q0 = qSketchRegion(id + "F247", true);
            extrude(context, id + "F248", {"entities" : qUnion([Q0]), "oppositeDirection" : true, "depth" : 114.3 * mm, "offsetDistance" : 25.4 * mm});
        }
        {
            var Q0;
            Q0=makeQuery(id+"F248.opExtrude","CAP_FACE",FACE,{"disambiguationData":[OSD([sQuery(id+"F247.wireOp",EDGE,"E686"),sQuery(id+"F247.wireOp",EDGE,"E687"),sQuery(id+"F247.wireOp",EDGE,"E688"),sQuery(id+"F247.wireOp",EDGE,"E689"),sQuery(id+"F247.wireOp",EDGE,"E690"),sQuery(id+"F247.wireOp",EDGE,"E691"),sQuery(id+"F247.wireOp",EDGE,"E692"),sQuery(id+"F247.wireOp",EDGE,"E693"),sQuery(id+"F247.wireOp",EDGE,"E694"),sQuery(id+"F247.wireOp",EDGE,"E695"),sQuery(id+"F247.wireOp",EDGE,"E696"),sQuery(id+"F247.wireOp",EDGE,"E697")])],"isStart":true});
            var sketch = newSketch(context, id + "F249", { "sketchPlane" : qUnion([Q0])});
            skLineSegment(sketch, "E698.bottom", {"start": v(7327.9, 25.4) * mm, "end": v(8242.3, 25.4) * mm});
            skLineSegment(sketch, "E698.top", {"start": v(7327.9, 2057.4) * mm, "end": v(8242.3, 2057.4) * mm});
            skLineSegment(sketch, "E698.left", {"start": v(7327.9, 25.4) * mm, "end": v(7327.9, 2057.4) * mm});
            skLineSegment(sketch, "E698.right", {"start": v(8242.3, 25.4) * mm, "end": v(8242.3, 2057.4) * mm});
            skSolve(sketch);
        }
        {
            var Q0;
            Q0 = qSketchRegion(id + "F249", true);
            extrude(context, id + "F250", {"entities" : qUnion([Q0]), "operationType" : NewBodyOperationType.REMOVE, "oppositeDirection" : true, "depth" : 25.4 * mm, "offsetDistance" : 25.4 * mm});
        }
        {
            var Q0;
            Q0=makeQuery(id+"F248.opExtrude","CAP_FACE",FACE,{"disambiguationData":[OSD([sQuery(id+"F247.wireOp",EDGE,"E686"),sQuery(id+"F247.wireOp",EDGE,"E687"),sQuery(id+"F247.wireOp",EDGE,"E688"),sQuery(id+"F247.wireOp",EDGE,"E689"),sQuery(id+"F247.wireOp",EDGE,"E690"),sQuery(id+"F247.wireOp",EDGE,"E691"),sQuery(id+"F247.wireOp",EDGE,"E692"),sQuery(id+"F247.wireOp",EDGE,"E693"),sQuery(id+"F247.wireOp",EDGE,"E694"),sQuery(id+"F247.wireOp",EDGE,"E695"),sQuery(id+"F247.wireOp",EDGE,"E696"),sQuery(id+"F247.wireOp",EDGE,"E697")])],"isStart":false});
            var sketch = newSketch(context, id + "F251", { "sketchPlane" : qUnion([Q0])});
            skLineSegment(sketch, "E699.bottom", {"start": v(-7327.9, 25.4) * mm, "end": v(-8242.3, 25.4) * mm});
            skLineSegment(sketch, "E699.top", {"start": v(-7327.9, 2057.4) * mm, "end": v(-8242.3, 2057.4) * mm});
            skLineSegment(sketch, "E699.left", {"start": v(-7327.9, 25.4) * mm, "end": v(-7327.9, 2057.4) * mm});
            skLineSegment(sketch, "E699.right", {"start": v(-8242.3, 25.4) * mm, "end": v(-8242.3, 2057.4) * mm});
            skSolve(sketch);
        }
        {
            var Q0;
            Q0 = qSketchRegion(id + "F251", true);
            extrude(context, id + "F252", {"entities" : qUnion([Q0]), "operationType" : NewBodyOperationType.REMOVE, "oppositeDirection" : true, "depth" : 57.15 * mm, "offsetDistance" : 25.4 * mm});
        }
        {
            var Q0;
            Q0=qCreatedBy(makeId("Top.planeOp"),FACE);
            var sketch = newSketch(context, id + "F253", { "sketchPlane" : qUnion([Q0])});
            skLineSegment(sketch, "E700", {"start": v(8255, 16344.9) * mm, "end": v(8255, 16459.2) * mm});
            skLineSegment(sketch, "E701", {"start": v(8255, 16459.2) * mm, "end": v(8242.3, 16459.2) * mm});
            skLineSegment(sketch, "E702", {"start": v(8242.3, 16459.2) * mm, "end": v(8242.3, 16402.05) * mm});
            skLineSegment(sketch, "E703", {"start": v(8242.3, 16402.05) * mm, "end": v(7327.9, 16402.05) * mm, "construction": true});
            skLineSegment(sketch, "E704", {"start": v(7327.9, 16402.05) * mm, "end": v(7327.9, 16459.2) * mm});
            skLineSegment(sketch, "E705", {"start": v(7327.9, 16459.2) * mm, "end": v(7315.2, 16459.2) * mm});
            skLineSegment(sketch, "E706", {"start": v(7315.2, 16459.2) * mm, "end": v(7315.2, 16344.9) * mm});
            skLineSegment(sketch, "E707", {"start": v(7315.2, 16344.9) * mm, "end": v(7327.9, 16344.9) * mm});
            skLineSegment(sketch, "E708", {"start": v(7327.9, 16344.9) * mm, "end": v(7327.9, 16370.3) * mm});
            skLineSegment(sketch, "E709", {"start": v(7327.9, 16370.3) * mm, "end": v(7346.77, 16370.3) * mm});
            skLineSegment(sketch, "E710", {"start": v(8242.3, 16344.9) * mm, "end": v(8255, 16344.9) * mm});
            skLineSegment(sketch, "E711", {"start": v(8242.3, 16402.05) * mm, "end": v(8242.3, 16370.33) * mm});
            skLineSegment(sketch, "E712", {"start": v(7327.9, 16402.05) * mm, "end": v(7327.9, 16370.33) * mm});
            skLineSegment(sketch, "E713", {"start": v(7327.9, 16386.18) * mm, "end": v(8242.3, 16386.18) * mm, "construction": true});
            skLineSegment(sketch, "E714.trimOffspring", {"start": v(8242.3, 16370.33) * mm, "end": v(7833.94, 16370.33) * mm});
            skLineSegment(sketch, "E715", {"start": v(7361.75, 16407.86) * mm, "end": v(7334.25, 16391.99) * mm});
            skLineSegment(sketch, "E716", {"start": v(7334.25, 16391.99) * mm, "end": v(7346.76, 16370.33) * mm});
            skLineSegment(sketch, "E717", {"start": v(7562.85, 15996.04) * mm, "end": v(7588.97, 16011.12) * mm});
            skLineSegment(sketch, "E718", {"start": v(7589.55, 16013.29) * mm, "end": v(7383.43, 16370.3) * mm});
            skLineSegment(sketch, "E719", {"start": v(7591.14, 16013.29) * mm, "end": v(7797.26, 16370.3) * mm});
            skLineSegment(sketch, "E720", {"start": v(7818.95, 16407.86) * mm, "end": v(7846.44, 16391.99) * mm});
            skLineSegment(sketch, "E721", {"start": v(7846.44, 16391.99) * mm, "end": v(7833.94, 16370.33) * mm});
            skLineSegment(sketch, "E722", {"start": v(7617.84, 15996.04) * mm, "end": v(7591.72, 16011.12) * mm});
            skLineSegment(sketch, "E723.trimOffspring", {"start": v(7833.92, 16370.3) * mm, "end": v(7617.84, 15996.04) * mm});
            skLineSegment(sketch, "E724.trimOffspring", {"start": v(7797.28, 16370.33) * mm, "end": v(7383.42, 16370.33) * mm});
            skLineSegment(sketch, "E725.trimOffspring", {"start": v(7833.92, 16370.3) * mm, "end": v(8242.3, 16370.3) * mm});
            skLineSegment(sketch, "E726.trimOffspring", {"start": v(7797.28, 16370.33) * mm, "end": v(7818.95, 16407.86) * mm});
            skLineSegment(sketch, "E727.trimOffspring", {"start": v(7383.42, 16370.33) * mm, "end": v(7361.75, 16407.86) * mm});
            skLineSegment(sketch, "E728.trimOffspring", {"start": v(7346.76, 16370.33) * mm, "end": v(7327.9, 16370.33) * mm});
            skLineSegment(sketch, "E729.trimOffspring", {"start": v(7383.43, 16370.3) * mm, "end": v(7797.26, 16370.3) * mm});
            skLineSegment(sketch, "E730.trimOffspring", {"start": v(7346.77, 16370.3) * mm, "end": v(7562.85, 15996.04) * mm});
            skArc(sketch, "E731", {"start": v(7591.14, 16013.29) * mm, "mid": v(7590.35, 16013.5) * mm, "end": v(7589.55, 16013.29) * mm});
            skArc(sketch, "E732.trimOffspring", {"start": v(7588.97, 16011.12) * mm, "mid": v(7590.35, 16010.33) * mm, "end": v(7591.72, 16011.12) * mm});
            skLineSegment(sketch, "E733", {"start": v(7348, 16399.92) * mm, "end": v(7355.94, 16386.18) * mm, "construction": true});
            skLineSegment(sketch, "E734.trimOffspring", {"start": v(8242.3, 16370.3) * mm, "end": v(8242.3, 16344.9) * mm});
            skSolve(sketch);
        }
        {
            var Q0;
            Q0 = qSketchRegion(id + "F253", true);
            extrude(context, id + "F254", {"entities" : qUnion([Q0]), "depth" : 25.4 * mm, "offsetDistance" : 25.4 * mm});
        }
    });
